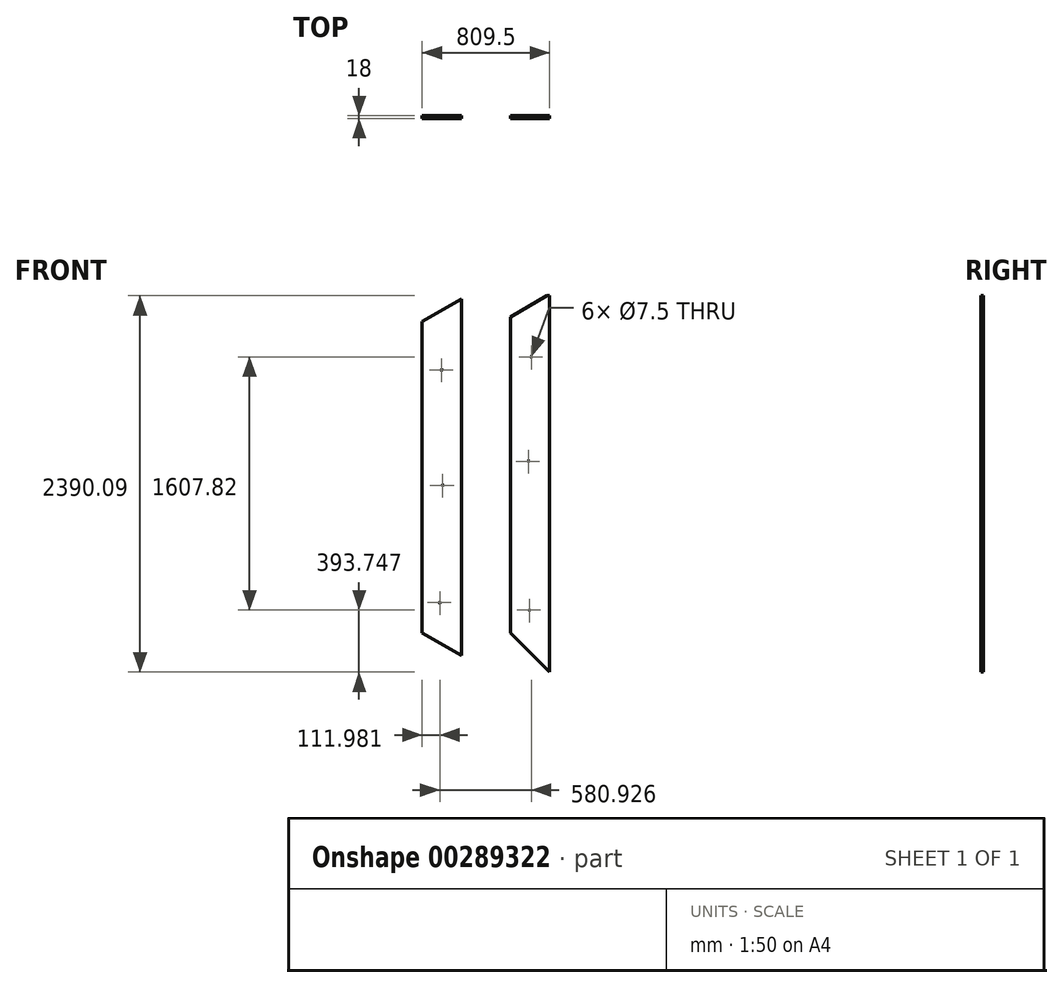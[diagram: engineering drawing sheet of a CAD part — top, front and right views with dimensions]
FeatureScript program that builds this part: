
annotation { "Feature Type Name" : "Feature", "Feature Type Description" : "" }
export const myFeature = defineFeature(function(context is Context, id is Id, definition is map)
    precondition{}
    {
        {
            var Q0;
            Q0=qCreatedBy(makeId("Front.planeOp"),FACE);
            var sketch = newSketch(context, id + "F0", { "sketchPlane" : qUnion([Q0])});
            skLineSegment(sketch, "E0", {"start": v(-600, -1204.44) * mm, "end": v(600, -1204.44) * mm});
            skLineSegment(sketch, "E1", {"start": v(600, -1204.44) * mm, "end": v(600, 1195.56) * mm});
            skLineSegment(sketch, "E2", {"start": v(600, 1195.56) * mm, "end": v(-600, 1195.56) * mm});
            skLineSegment(sketch, "E3", {"start": v(-600, 1195.56) * mm, "end": v(-600, -1204.44) * mm});
            skLineSegment(sketch, "E4", {"start": v(547.42, 1204.44) * mm, "end": v(297.92, 954.93) * mm});
            skLineSegment(sketch, "E5", {"start": v(297.92, 954.93) * mm, "end": v(297.92, -1050.48) * mm});
            skLineSegment(sketch, "E6", {"start": v(297.92, -1050.48) * mm, "end": v(547.41, -1194.53) * mm});
            skLineSegment(sketch, "E7", {"start": v(547.41, -1194.53) * mm, "end": v(547.42, 1204.44) * mm});
            skLineSegment(sketch, "E8", {"start": v(17.92, 1060.4) * mm, "end": v(17.92, -945.02) * mm});
            skLineSegment(sketch, "E9", {"start": v(17.92, -945.02) * mm, "end": v(267.42, -1194.53) * mm});
            skLineSegment(sketch, "E10", {"start": v(267.42, -1194.53) * mm, "end": v(267.41, 1204.44) * mm});
            skLineSegment(sketch, "E11", {"start": v(267.41, 1204.44) * mm, "end": v(17.92, 1060.4) * mm});
            skLineSegment(sketch, "E12", {"start": v(-262.08, -945.11) * mm, "end": v(-12.58, -1089.16) * mm});
            skLineSegment(sketch, "E13", {"start": v(-12.58, -1089.16) * mm, "end": v(-12.58, 1174.44) * mm});
            skLineSegment(sketch, "E14", {"start": v(-12.58, 1174.44) * mm, "end": v(-262.07, 1030.39) * mm});
            skLineSegment(sketch, "E15", {"start": v(-262.07, 1030.39) * mm, "end": v(-262.08, -945.11) * mm});
            skLineSegment(sketch, "E16", {"start": v(-292.58, 1174.44) * mm, "end": v(-542.07, 1030.39) * mm});
            skLineSegment(sketch, "E17", {"start": v(-542.07, 1030.39) * mm, "end": v(-542.08, -945.11) * mm});
            skLineSegment(sketch, "E18", {"start": v(-542.08, -945.11) * mm, "end": v(-292.58, -1089.16) * mm});
            skLineSegment(sketch, "E19", {"start": v(-292.58, -1089.16) * mm, "end": v(-292.58, 1174.44) * mm});
            skLineSegment(sketch, "E20", {"start": v(479.4, 17.48) * mm, "end": v(479.24, 17.93) * mm});
            skLineSegment(sketch, "E21", {"start": v(479.24, 17.93) * mm, "end": v(479.08, 18.37) * mm});
            skLineSegment(sketch, "E22", {"start": v(479.08, 18.37) * mm, "end": v(478.9, 18.8) * mm});
            skLineSegment(sketch, "E23", {"start": v(478.9, 18.8) * mm, "end": v(478.7, 19.24) * mm});
            skLineSegment(sketch, "E24", {"start": v(478.7, 19.24) * mm, "end": v(478.5, 19.66) * mm});
            skLineSegment(sketch, "E25", {"start": v(478.5, 19.66) * mm, "end": v(478.29, 20.08) * mm});
            skLineSegment(sketch, "E26", {"start": v(478.29, 20.08) * mm, "end": v(478.05, 20.49) * mm});
            skLineSegment(sketch, "E27", {"start": v(478.05, 20.49) * mm, "end": v(477.8, 20.9) * mm});
            skLineSegment(sketch, "E28", {"start": v(477.8, 20.9) * mm, "end": v(477.55, 21.28) * mm});
            skLineSegment(sketch, "E29", {"start": v(477.55, 21.28) * mm, "end": v(477.28, 21.67) * mm});
            skLineSegment(sketch, "E30", {"start": v(477.28, 21.67) * mm, "end": v(477, 22.05) * mm});
            skLineSegment(sketch, "E31", {"start": v(477, 22.05) * mm, "end": v(476.7, 22.42) * mm});
            skLineSegment(sketch, "E32", {"start": v(476.7, 22.42) * mm, "end": v(476.4, 22.78) * mm});
            skLineSegment(sketch, "E33", {"start": v(476.4, 22.78) * mm, "end": v(476.09, 23.13) * mm});
            skLineSegment(sketch, "E34", {"start": v(476.09, 23.13) * mm, "end": v(475.76, 23.47) * mm});
            skLineSegment(sketch, "E35", {"start": v(475.76, 23.47) * mm, "end": v(475.42, 23.8) * mm});
            skLineSegment(sketch, "E36", {"start": v(475.42, 23.8) * mm, "end": v(475.14, 24.06) * mm});
            skLineSegment(sketch, "E37", {"start": v(475.14, 24.06) * mm, "end": v(474.85, 24.31) * mm});
            skLineSegment(sketch, "E38", {"start": v(474.85, 24.31) * mm, "end": v(474.56, 24.56) * mm});
            skLineSegment(sketch, "E39", {"start": v(474.56, 24.56) * mm, "end": v(474.26, 24.8) * mm});
            skLineSegment(sketch, "E40", {"start": v(474.26, 24.8) * mm, "end": v(473.95, 25.03) * mm});
            skLineSegment(sketch, "E41", {"start": v(473.95, 25.03) * mm, "end": v(473.64, 25.25) * mm});
            skLineSegment(sketch, "E42", {"start": v(473.64, 25.25) * mm, "end": v(473.33, 25.47) * mm});
            skLineSegment(sketch, "E43", {"start": v(473.33, 25.47) * mm, "end": v(473, 25.67) * mm});
            skLineSegment(sketch, "E44", {"start": v(473, 25.67) * mm, "end": v(472.68, 25.87) * mm});
            skLineSegment(sketch, "E45", {"start": v(472.68, 25.87) * mm, "end": v(472.35, 26.06) * mm});
            skLineSegment(sketch, "E46", {"start": v(472.35, 26.06) * mm, "end": v(472.01, 26.24) * mm});
            skLineSegment(sketch, "E47", {"start": v(472.01, 26.24) * mm, "end": v(471.68, 26.4) * mm});
            skLineSegment(sketch, "E48", {"start": v(471.68, 26.4) * mm, "end": v(471.33, 26.57) * mm});
            skLineSegment(sketch, "E49", {"start": v(471.33, 26.57) * mm, "end": v(470.99, 26.72) * mm});
            skLineSegment(sketch, "E50", {"start": v(470.99, 26.72) * mm, "end": v(470.63, 26.87) * mm});
            skLineSegment(sketch, "E51", {"start": v(470.63, 26.87) * mm, "end": v(470.28, 27) * mm});
            skLineSegment(sketch, "E52", {"start": v(470.28, 27) * mm, "end": v(469.92, 27.13) * mm});
            skLineSegment(sketch, "E53", {"start": v(469.92, 27.13) * mm, "end": v(469.56, 27.25) * mm});
            skLineSegment(sketch, "E54", {"start": v(469.56, 27.25) * mm, "end": v(469.2, 27.36) * mm});
            skLineSegment(sketch, "E55", {"start": v(469.2, 27.36) * mm, "end": v(468.83, 27.45) * mm});
            skLineSegment(sketch, "E56", {"start": v(468.83, 27.45) * mm, "end": v(468.46, 27.54) * mm});
            skLineSegment(sketch, "E57", {"start": v(468.46, 27.54) * mm, "end": v(468.1, 27.62) * mm});
            skLineSegment(sketch, "E58", {"start": v(468.1, 27.62) * mm, "end": v(467.72, 27.7) * mm});
            skLineSegment(sketch, "E59", {"start": v(467.72, 27.7) * mm, "end": v(467.34, 27.76) * mm});
            skLineSegment(sketch, "E60", {"start": v(467.34, 27.76) * mm, "end": v(466.97, 27.8) * mm});
            skLineSegment(sketch, "E61", {"start": v(466.97, 27.8) * mm, "end": v(466.59, 27.85) * mm});
            skLineSegment(sketch, "E62", {"start": v(466.59, 27.85) * mm, "end": v(466.2, 27.88) * mm});
            skLineSegment(sketch, "E63", {"start": v(466.2, 27.88) * mm, "end": v(465.83, 27.9) * mm});
            skLineSegment(sketch, "E64", {"start": v(465.83, 27.9) * mm, "end": v(465.44, 27.92) * mm});
            skLineSegment(sketch, "E65", {"start": v(465.44, 27.92) * mm, "end": v(465.06, 27.92) * mm});
            skLineSegment(sketch, "E66", {"start": v(465.06, 27.92) * mm, "end": v(464.67, 27.92) * mm});
            skLineSegment(sketch, "E67", {"start": v(464.67, 27.92) * mm, "end": v(464.29, 27.9) * mm});
            skLineSegment(sketch, "E68", {"start": v(464.29, 27.9) * mm, "end": v(463.94, 27.9) * mm});
            skLineSegment(sketch, "E69", {"start": v(463.94, 27.9) * mm, "end": v(463.58, 27.91) * mm});
            skLineSegment(sketch, "E70", {"start": v(463.58, 27.91) * mm, "end": v(463.23, 27.9) * mm});
            skLineSegment(sketch, "E71", {"start": v(463.23, 27.9) * mm, "end": v(462.88, 27.89) * mm});
            skLineSegment(sketch, "E72", {"start": v(462.88, 27.89) * mm, "end": v(462.53, 27.86) * mm});
            skLineSegment(sketch, "E73", {"start": v(462.53, 27.86) * mm, "end": v(462.18, 27.82) * mm});
            skLineSegment(sketch, "E74", {"start": v(462.18, 27.82) * mm, "end": v(461.83, 27.78) * mm});
            skLineSegment(sketch, "E75", {"start": v(461.83, 27.78) * mm, "end": v(461.48, 27.73) * mm});
            skLineSegment(sketch, "E76", {"start": v(461.48, 27.73) * mm, "end": v(461.14, 27.67) * mm});
            skLineSegment(sketch, "E77", {"start": v(461.14, 27.67) * mm, "end": v(460.8, 27.6) * mm});
            skLineSegment(sketch, "E78", {"start": v(460.8, 27.6) * mm, "end": v(460.46, 27.52) * mm});
            skLineSegment(sketch, "E79", {"start": v(460.46, 27.52) * mm, "end": v(460.12, 27.43) * mm});
            skLineSegment(sketch, "E80", {"start": v(460.12, 27.43) * mm, "end": v(459.79, 27.33) * mm});
            skLineSegment(sketch, "E81", {"start": v(459.79, 27.33) * mm, "end": v(459.45, 27.23) * mm});
            skLineSegment(sketch, "E82", {"start": v(459.45, 27.23) * mm, "end": v(459.12, 27.12) * mm});
            skLineSegment(sketch, "E83", {"start": v(459.12, 27.12) * mm, "end": v(458.8, 27) * mm});
            skLineSegment(sketch, "E84", {"start": v(458.8, 27) * mm, "end": v(458.47, 26.86) * mm});
            skLineSegment(sketch, "E85", {"start": v(458.47, 26.86) * mm, "end": v(458.15, 26.73) * mm});
            skLineSegment(sketch, "E86", {"start": v(458.15, 26.73) * mm, "end": v(457.84, 26.58) * mm});
            skLineSegment(sketch, "E87", {"start": v(457.84, 26.58) * mm, "end": v(457.52, 26.43) * mm});
            skLineSegment(sketch, "E88", {"start": v(457.52, 26.43) * mm, "end": v(457.21, 26.26) * mm});
            skLineSegment(sketch, "E89", {"start": v(457.21, 26.26) * mm, "end": v(456.9, 26.1) * mm});
            skLineSegment(sketch, "E90", {"start": v(456.9, 26.1) * mm, "end": v(456.6, 25.92) * mm});
            skLineSegment(sketch, "E91", {"start": v(456.6, 25.92) * mm, "end": v(456.31, 25.73) * mm});
            skLineSegment(sketch, "E92", {"start": v(456.31, 25.73) * mm, "end": v(456.02, 25.54) * mm});
            skLineSegment(sketch, "E93", {"start": v(456.02, 25.54) * mm, "end": v(455.73, 25.34) * mm});
            skLineSegment(sketch, "E94", {"start": v(455.73, 25.34) * mm, "end": v(455.45, 25.13) * mm});
            skLineSegment(sketch, "E95", {"start": v(455.45, 25.13) * mm, "end": v(455.18, 24.91) * mm});
            skLineSegment(sketch, "E96", {"start": v(455.18, 24.91) * mm, "end": v(454.9, 24.69) * mm});
            skLineSegment(sketch, "E97", {"start": v(454.9, 24.69) * mm, "end": v(454.64, 24.46) * mm});
            skLineSegment(sketch, "E98", {"start": v(454.64, 24.46) * mm, "end": v(454.38, 24.22) * mm});
            skLineSegment(sketch, "E99", {"start": v(454.38, 24.22) * mm, "end": v(454.12, 23.97) * mm});
            skLineSegment(sketch, "E100", {"start": v(454.12, 23.97) * mm, "end": v(453.78, 23.63) * mm});
            skLineSegment(sketch, "E101", {"start": v(453.78, 23.63) * mm, "end": v(453.45, 23.28) * mm});
            skLineSegment(sketch, "E102", {"start": v(453.45, 23.28) * mm, "end": v(453.14, 22.9) * mm});
            skLineSegment(sketch, "E103", {"start": v(453.14, 22.9) * mm, "end": v(452.86, 22.53) * mm});
            skLineSegment(sketch, "E104", {"start": v(452.86, 22.53) * mm, "end": v(452.6, 22.14) * mm});
            skLineSegment(sketch, "E105", {"start": v(452.6, 22.14) * mm, "end": v(452.34, 21.74) * mm});
            skLineSegment(sketch, "E106", {"start": v(452.34, 21.74) * mm, "end": v(452.12, 21.34) * mm});
            skLineSegment(sketch, "E107", {"start": v(452.12, 21.34) * mm, "end": v(451.91, 20.92) * mm});
            skLineSegment(sketch, "E108", {"start": v(451.91, 20.92) * mm, "end": v(451.73, 20.5) * mm});
            skLineSegment(sketch, "E109", {"start": v(451.73, 20.5) * mm, "end": v(451.56, 20.06) * mm});
            skLineSegment(sketch, "E110", {"start": v(451.56, 20.06) * mm, "end": v(451.41, 19.63) * mm});
            skLineSegment(sketch, "E111", {"start": v(451.41, 19.63) * mm, "end": v(451.29, 19.18) * mm});
            skLineSegment(sketch, "E112", {"start": v(451.29, 19.18) * mm, "end": v(451.18, 18.74) * mm});
            skLineSegment(sketch, "E113", {"start": v(451.18, 18.74) * mm, "end": v(451.1, 18.29) * mm});
            skLineSegment(sketch, "E114", {"start": v(451.1, 18.29) * mm, "end": v(451.04, 17.83) * mm});
            skLineSegment(sketch, "E115", {"start": v(451.04, 17.83) * mm, "end": v(451, 17.38) * mm});
            skLineSegment(sketch, "E116", {"start": v(451, 17.38) * mm, "end": v(450.97, 16.92) * mm});
            skLineSegment(sketch, "E117", {"start": v(450.97, 16.92) * mm, "end": v(450.97, 16.46) * mm});
            skLineSegment(sketch, "E118", {"start": v(450.97, 16.46) * mm, "end": v(450.99, 16) * mm});
            skLineSegment(sketch, "E119", {"start": v(450.99, 16) * mm, "end": v(451.03, 15.55) * mm});
            skLineSegment(sketch, "E120", {"start": v(451.03, 15.55) * mm, "end": v(451.09, 15.1) * mm});
            skLineSegment(sketch, "E121", {"start": v(451.09, 15.1) * mm, "end": v(451.17, 14.64) * mm});
            skLineSegment(sketch, "E122", {"start": v(451.17, 14.64) * mm, "end": v(451.27, 14.19) * mm});
            skLineSegment(sketch, "E123", {"start": v(451.27, 14.19) * mm, "end": v(451.4, 13.74) * mm});
            skLineSegment(sketch, "E124", {"start": v(451.4, 13.74) * mm, "end": v(451.54, 13.3) * mm});
            skLineSegment(sketch, "E125", {"start": v(451.54, 13.3) * mm, "end": v(451.7, 12.86) * mm});
            skLineSegment(sketch, "E126", {"start": v(451.7, 12.86) * mm, "end": v(451.89, 12.43) * mm});
            skLineSegment(sketch, "E127", {"start": v(451.89, 12.43) * mm, "end": v(452.1, 12) * mm});
            skLineSegment(sketch, "E128", {"start": v(452.1, 12) * mm, "end": v(452.32, 11.6) * mm});
            skLineSegment(sketch, "E129", {"start": v(452.32, 11.6) * mm, "end": v(452.57, 11.19) * mm});
            skLineSegment(sketch, "E130", {"start": v(452.57, 11.19) * mm, "end": v(452.84, 10.79) * mm});
            skLineSegment(sketch, "E131", {"start": v(452.84, 10.79) * mm, "end": v(453.14, 10.4) * mm});
            skLineSegment(sketch, "E132", {"start": v(453.14, 10.4) * mm, "end": v(453.43, 10.1) * mm});
            skLineSegment(sketch, "E133", {"start": v(453.43, 10.1) * mm, "end": v(453.74, 9.8) * mm});
            skLineSegment(sketch, "E134", {"start": v(453.74, 9.8) * mm, "end": v(454.04, 9.53) * mm});
            skLineSegment(sketch, "E135", {"start": v(454.04, 9.53) * mm, "end": v(454.36, 9.25) * mm});
            skLineSegment(sketch, "E136", {"start": v(454.36, 9.25) * mm, "end": v(454.69, 8.99) * mm});
            skLineSegment(sketch, "E137", {"start": v(454.69, 8.99) * mm, "end": v(455.01, 8.73) * mm});
            skLineSegment(sketch, "E138", {"start": v(455.01, 8.73) * mm, "end": v(455.35, 8.49) * mm});
            skLineSegment(sketch, "E139", {"start": v(455.35, 8.49) * mm, "end": v(455.7, 8.25) * mm});
            skLineSegment(sketch, "E140", {"start": v(455.7, 8.25) * mm, "end": v(456.04, 8.03) * mm});
            skLineSegment(sketch, "E141", {"start": v(456.04, 8.03) * mm, "end": v(456.4, 7.8) * mm});
            skLineSegment(sketch, "E142", {"start": v(456.4, 7.8) * mm, "end": v(456.75, 7.6) * mm});
            skLineSegment(sketch, "E143", {"start": v(456.75, 7.6) * mm, "end": v(457.12, 7.4) * mm});
            skLineSegment(sketch, "E144", {"start": v(457.12, 7.4) * mm, "end": v(457.49, 7.22) * mm});
            skLineSegment(sketch, "E145", {"start": v(457.49, 7.22) * mm, "end": v(457.86, 7.04) * mm});
            skLineSegment(sketch, "E146", {"start": v(457.86, 7.04) * mm, "end": v(458.24, 6.87) * mm});
            skLineSegment(sketch, "E147", {"start": v(458.24, 6.87) * mm, "end": v(458.62, 6.72) * mm});
            skLineSegment(sketch, "E148", {"start": v(458.62, 6.72) * mm, "end": v(459, 6.57) * mm});
            skLineSegment(sketch, "E149", {"start": v(459, 6.57) * mm, "end": v(459.4, 6.43) * mm});
            skLineSegment(sketch, "E150", {"start": v(459.4, 6.43) * mm, "end": v(459.8, 6.3) * mm});
            skLineSegment(sketch, "E151", {"start": v(459.8, 6.3) * mm, "end": v(460.19, 6.19) * mm});
            skLineSegment(sketch, "E152", {"start": v(460.19, 6.19) * mm, "end": v(460.59, 6.08) * mm});
            skLineSegment(sketch, "E153", {"start": v(460.59, 6.08) * mm, "end": v(461, 5.99) * mm});
            skLineSegment(sketch, "E154", {"start": v(461, 5.99) * mm, "end": v(461.4, 5.9) * mm});
            skLineSegment(sketch, "E155", {"start": v(461.4, 5.9) * mm, "end": v(461.8, 5.83) * mm});
            skLineSegment(sketch, "E156", {"start": v(461.8, 5.83) * mm, "end": v(462.22, 5.77) * mm});
            skLineSegment(sketch, "E157", {"start": v(462.22, 5.77) * mm, "end": v(462.63, 5.72) * mm});
            skLineSegment(sketch, "E158", {"start": v(462.63, 5.72) * mm, "end": v(463.05, 5.68) * mm});
            skLineSegment(sketch, "E159", {"start": v(463.05, 5.68) * mm, "end": v(463.46, 5.65) * mm});
            skLineSegment(sketch, "E160", {"start": v(463.46, 5.65) * mm, "end": v(463.88, 5.63) * mm});
            skLineSegment(sketch, "E161", {"start": v(463.88, 5.63) * mm, "end": v(464.3, 5.63) * mm});
            skLineSegment(sketch, "E162", {"start": v(464.3, 5.63) * mm, "end": v(464.72, 5.63) * mm});
            skLineSegment(sketch, "E163", {"start": v(464.72, 5.63) * mm, "end": v(465.14, 5.65) * mm});
            skLineSegment(sketch, "E164", {"start": v(465.14, 5.65) * mm, "end": v(465.7, 5.71) * mm});
            skLineSegment(sketch, "E165", {"start": v(465.7, 5.71) * mm, "end": v(466.26, 5.75) * mm});
            skLineSegment(sketch, "E166", {"start": v(466.26, 5.75) * mm, "end": v(466.81, 5.76) * mm});
            skLineSegment(sketch, "E167", {"start": v(466.81, 5.76) * mm, "end": v(467.36, 5.74) * mm});
            skLineSegment(sketch, "E168", {"start": v(467.36, 5.74) * mm, "end": v(467.9, 5.7) * mm});
            skLineSegment(sketch, "E169", {"start": v(467.9, 5.7) * mm, "end": v(468.45, 5.62) * mm});
            skLineSegment(sketch, "E170", {"start": v(468.45, 5.62) * mm, "end": v(468.98, 5.53) * mm});
            skLineSegment(sketch, "E171", {"start": v(468.98, 5.53) * mm, "end": v(469.5, 5.4) * mm});
            skLineSegment(sketch, "E172", {"start": v(469.5, 5.4) * mm, "end": v(470.02, 5.26) * mm});
            skLineSegment(sketch, "E173", {"start": v(470.02, 5.26) * mm, "end": v(470.53, 5.1) * mm});
            skLineSegment(sketch, "E174", {"start": v(470.53, 5.1) * mm, "end": v(471.03, 4.9) * mm});
            skLineSegment(sketch, "E175", {"start": v(471.03, 4.9) * mm, "end": v(471.52, 4.69) * mm});
            skLineSegment(sketch, "E176", {"start": v(471.52, 4.69) * mm, "end": v(472, 4.45) * mm});
            skLineSegment(sketch, "E177", {"start": v(472, 4.45) * mm, "end": v(472.46, 4.2) * mm});
            skLineSegment(sketch, "E178", {"start": v(472.46, 4.2) * mm, "end": v(472.91, 3.91) * mm});
            skLineSegment(sketch, "E179", {"start": v(472.91, 3.91) * mm, "end": v(473.35, 3.61) * mm});
            skLineSegment(sketch, "E180", {"start": v(473.35, 3.61) * mm, "end": v(473.77, 3.3) * mm});
            skLineSegment(sketch, "E181", {"start": v(473.77, 3.3) * mm, "end": v(474.18, 2.96) * mm});
            skLineSegment(sketch, "E182", {"start": v(474.18, 2.96) * mm, "end": v(474.58, 2.6) * mm});
            skLineSegment(sketch, "E183", {"start": v(474.58, 2.6) * mm, "end": v(474.95, 2.22) * mm});
            skLineSegment(sketch, "E184", {"start": v(474.95, 2.22) * mm, "end": v(475.31, 1.83) * mm});
            skLineSegment(sketch, "E185", {"start": v(475.31, 1.83) * mm, "end": v(475.66, 1.42) * mm});
            skLineSegment(sketch, "E186", {"start": v(475.66, 1.42) * mm, "end": v(475.98, 1) * mm});
            skLineSegment(sketch, "E187", {"start": v(475.98, 1) * mm, "end": v(476.28, 0.55) * mm});
            skLineSegment(sketch, "E188", {"start": v(476.28, 0.55) * mm, "end": v(476.57, 0.1) * mm});
            skLineSegment(sketch, "E189", {"start": v(476.57, 0.1) * mm, "end": v(476.83, -0.38) * mm});
            skLineSegment(sketch, "E190", {"start": v(476.83, -0.38) * mm, "end": v(477.07, -0.87) * mm});
            skLineSegment(sketch, "E191", {"start": v(477.07, -0.87) * mm, "end": v(477.29, -1.37) * mm});
            skLineSegment(sketch, "E192", {"start": v(477.29, -1.37) * mm, "end": v(477.48, -1.88) * mm});
            skLineSegment(sketch, "E193", {"start": v(477.48, -1.88) * mm, "end": v(477.65, -2.41) * mm});
            skLineSegment(sketch, "E194", {"start": v(477.65, -2.41) * mm, "end": v(477.8, -2.95) * mm});
            skLineSegment(sketch, "E195", {"start": v(477.8, -2.95) * mm, "end": v(477.92, -3.5) * mm});
            skLineSegment(sketch, "E196", {"start": v(477.92, -3.5) * mm, "end": v(477.92, -3.96) * mm});
            skLineSegment(sketch, "E197", {"start": v(477.92, -3.96) * mm, "end": v(477.9, -4.41) * mm});
            skLineSegment(sketch, "E198", {"start": v(477.9, -4.41) * mm, "end": v(477.84, -4.86) * mm});
            skLineSegment(sketch, "E199", {"start": v(477.84, -4.86) * mm, "end": v(477.76, -5.3) * mm});
            skLineSegment(sketch, "E200", {"start": v(477.76, -5.3) * mm, "end": v(477.66, -5.75) * mm});
            skLineSegment(sketch, "E201", {"start": v(477.66, -5.75) * mm, "end": v(477.54, -6.18) * mm});
            skLineSegment(sketch, "E202", {"start": v(477.54, -6.18) * mm, "end": v(477.39, -6.6) * mm});
            skLineSegment(sketch, "E203", {"start": v(477.39, -6.6) * mm, "end": v(477.22, -7.02) * mm});
            skLineSegment(sketch, "E204", {"start": v(477.22, -7.02) * mm, "end": v(477.02, -7.42) * mm});
            skLineSegment(sketch, "E205", {"start": v(477.02, -7.42) * mm, "end": v(476.8, -7.81) * mm});
            skLineSegment(sketch, "E206", {"start": v(476.8, -7.81) * mm, "end": v(476.57, -8.2) * mm});
            skLineSegment(sketch, "E207", {"start": v(476.57, -8.2) * mm, "end": v(476.3, -8.56) * mm});
            skLineSegment(sketch, "E208", {"start": v(476.3, -8.56) * mm, "end": v(476.03, -8.91) * mm});
            skLineSegment(sketch, "E209", {"start": v(476.03, -8.91) * mm, "end": v(475.72, -9.25) * mm});
            skLineSegment(sketch, "E210", {"start": v(475.72, -9.25) * mm, "end": v(475.4, -9.57) * mm});
            skLineSegment(sketch, "E211", {"start": v(475.4, -9.57) * mm, "end": v(475.06, -9.88) * mm});
            skLineSegment(sketch, "E212", {"start": v(475.06, -9.88) * mm, "end": v(474.78, -10.13) * mm});
            skLineSegment(sketch, "E213", {"start": v(474.78, -10.13) * mm, "end": v(474.5, -10.37) * mm});
            skLineSegment(sketch, "E214", {"start": v(474.5, -10.37) * mm, "end": v(474.2, -10.6) * mm});
            skLineSegment(sketch, "E215", {"start": v(474.2, -10.6) * mm, "end": v(473.91, -10.82) * mm});
            skLineSegment(sketch, "E216", {"start": v(473.91, -10.82) * mm, "end": v(473.61, -11.04) * mm});
            skLineSegment(sketch, "E217", {"start": v(473.61, -11.04) * mm, "end": v(473.3, -11.25) * mm});
            skLineSegment(sketch, "E218", {"start": v(473.3, -11.25) * mm, "end": v(473, -11.45) * mm});
            skLineSegment(sketch, "E219", {"start": v(473, -11.45) * mm, "end": v(472.68, -11.65) * mm});
            skLineSegment(sketch, "E220", {"start": v(472.68, -11.65) * mm, "end": v(472.36, -11.83) * mm});
            skLineSegment(sketch, "E221", {"start": v(472.36, -11.83) * mm, "end": v(472.04, -12) * mm});
            skLineSegment(sketch, "E222", {"start": v(472.04, -12) * mm, "end": v(471.7, -12.18) * mm});
            skLineSegment(sketch, "E223", {"start": v(471.7, -12.18) * mm, "end": v(471.38, -12.34) * mm});
            skLineSegment(sketch, "E224", {"start": v(471.38, -12.34) * mm, "end": v(471.04, -12.49) * mm});
            skLineSegment(sketch, "E225", {"start": v(471.04, -12.49) * mm, "end": v(470.7, -12.63) * mm});
            skLineSegment(sketch, "E226", {"start": v(470.7, -12.63) * mm, "end": v(470.36, -12.77) * mm});
            skLineSegment(sketch, "E227", {"start": v(470.36, -12.77) * mm, "end": v(470.01, -12.9) * mm});
            skLineSegment(sketch, "E228", {"start": v(470.01, -12.9) * mm, "end": v(469.67, -13) * mm});
            skLineSegment(sketch, "E229", {"start": v(469.67, -13) * mm, "end": v(469.31, -13.12) * mm});
            skLineSegment(sketch, "E230", {"start": v(469.31, -13.12) * mm, "end": v(468.96, -13.22) * mm});
            skLineSegment(sketch, "E231", {"start": v(468.96, -13.22) * mm, "end": v(468.6, -13.3) * mm});
            skLineSegment(sketch, "E232", {"start": v(468.6, -13.3) * mm, "end": v(468.24, -13.4) * mm});
            skLineSegment(sketch, "E233", {"start": v(468.24, -13.4) * mm, "end": v(467.88, -13.46) * mm});
            skLineSegment(sketch, "E234", {"start": v(467.88, -13.46) * mm, "end": v(467.52, -13.53) * mm});
            skLineSegment(sketch, "E235", {"start": v(467.52, -13.53) * mm, "end": v(467.15, -13.58) * mm});
            skLineSegment(sketch, "E236", {"start": v(467.15, -13.58) * mm, "end": v(466.79, -13.63) * mm});
            skLineSegment(sketch, "E237", {"start": v(466.79, -13.63) * mm, "end": v(466.42, -13.67) * mm});
            skLineSegment(sketch, "E238", {"start": v(466.42, -13.67) * mm, "end": v(466.05, -13.7) * mm});
            skLineSegment(sketch, "E239", {"start": v(466.05, -13.7) * mm, "end": v(465.68, -13.71) * mm});
            skLineSegment(sketch, "E240", {"start": v(465.68, -13.71) * mm, "end": v(465.3, -13.72) * mm});
            skLineSegment(sketch, "E241", {"start": v(465.3, -13.72) * mm, "end": v(464.94, -13.72) * mm});
            skLineSegment(sketch, "E242", {"start": v(464.94, -13.72) * mm, "end": v(464.56, -13.71) * mm});
            skLineSegment(sketch, "E243", {"start": v(464.56, -13.71) * mm, "end": v(464.2, -13.7) * mm});
            skLineSegment(sketch, "E244", {"start": v(464.2, -13.7) * mm, "end": v(463.86, -13.7) * mm});
            skLineSegment(sketch, "E245", {"start": v(463.86, -13.7) * mm, "end": v(463.53, -13.7) * mm});
            skLineSegment(sketch, "E246", {"start": v(463.53, -13.7) * mm, "end": v(463.2, -13.68) * mm});
            skLineSegment(sketch, "E247", {"start": v(463.2, -13.68) * mm, "end": v(462.88, -13.66) * mm});
            skLineSegment(sketch, "E248", {"start": v(462.88, -13.66) * mm, "end": v(462.56, -13.63) * mm});
            skLineSegment(sketch, "E249", {"start": v(462.56, -13.63) * mm, "end": v(462.23, -13.6) * mm});
            skLineSegment(sketch, "E250", {"start": v(462.23, -13.6) * mm, "end": v(461.9, -13.56) * mm});
            skLineSegment(sketch, "E251", {"start": v(461.9, -13.56) * mm, "end": v(461.59, -13.5) * mm});
            skLineSegment(sketch, "E252", {"start": v(461.59, -13.5) * mm, "end": v(461.27, -13.45) * mm});
            skLineSegment(sketch, "E253", {"start": v(461.27, -13.45) * mm, "end": v(460.95, -13.38) * mm});
            skLineSegment(sketch, "E254", {"start": v(460.95, -13.38) * mm, "end": v(460.63, -13.3) * mm});
            skLineSegment(sketch, "E255", {"start": v(460.63, -13.3) * mm, "end": v(460.32, -13.22) * mm});
            skLineSegment(sketch, "E256", {"start": v(460.32, -13.22) * mm, "end": v(460, -13.14) * mm});
            skLineSegment(sketch, "E257", {"start": v(460, -13.14) * mm, "end": v(459.7, -13.04) * mm});
            skLineSegment(sketch, "E258", {"start": v(459.7, -13.04) * mm, "end": v(459.4, -12.94) * mm});
            skLineSegment(sketch, "E259", {"start": v(459.4, -12.94) * mm, "end": v(459.09, -12.82) * mm});
            skLineSegment(sketch, "E260", {"start": v(459.09, -12.82) * mm, "end": v(458.78, -12.7) * mm});
            skLineSegment(sketch, "E261", {"start": v(458.78, -12.7) * mm, "end": v(458.49, -12.58) * mm});
            skLineSegment(sketch, "E262", {"start": v(458.49, -12.58) * mm, "end": v(458.19, -12.45) * mm});
            skLineSegment(sketch, "E263", {"start": v(458.19, -12.45) * mm, "end": v(457.9, -12.3) * mm});
            skLineSegment(sketch, "E264", {"start": v(457.9, -12.3) * mm, "end": v(457.6, -12.16) * mm});
            skLineSegment(sketch, "E265", {"start": v(457.6, -12.16) * mm, "end": v(457.32, -12) * mm});
            skLineSegment(sketch, "E266", {"start": v(457.32, -12) * mm, "end": v(457.04, -11.85) * mm});
            skLineSegment(sketch, "E267", {"start": v(457.04, -11.85) * mm, "end": v(456.76, -11.68) * mm});
            skLineSegment(sketch, "E268", {"start": v(456.76, -11.68) * mm, "end": v(456.48, -11.5) * mm});
            skLineSegment(sketch, "E269", {"start": v(456.48, -11.5) * mm, "end": v(456.21, -11.33) * mm});
            skLineSegment(sketch, "E270", {"start": v(456.21, -11.33) * mm, "end": v(455.95, -11.14) * mm});
            skLineSegment(sketch, "E271", {"start": v(455.95, -11.14) * mm, "end": v(455.68, -10.94) * mm});
            skLineSegment(sketch, "E272", {"start": v(455.68, -10.94) * mm, "end": v(455.43, -10.74) * mm});
            skLineSegment(sketch, "E273", {"start": v(455.43, -10.74) * mm, "end": v(455.17, -10.54) * mm});
            skLineSegment(sketch, "E274", {"start": v(455.17, -10.54) * mm, "end": v(454.93, -10.32) * mm});
            skLineSegment(sketch, "E275", {"start": v(454.93, -10.32) * mm, "end": v(454.68, -10.1) * mm});
            skLineSegment(sketch, "E276", {"start": v(454.68, -10.1) * mm, "end": v(454.38, -9.77) * mm});
            skLineSegment(sketch, "E277", {"start": v(454.38, -9.77) * mm, "end": v(454.1, -9.44) * mm});
            skLineSegment(sketch, "E278", {"start": v(454.1, -9.44) * mm, "end": v(453.82, -9.1) * mm});
            skLineSegment(sketch, "E279", {"start": v(453.82, -9.1) * mm, "end": v(453.56, -8.74) * mm});
            skLineSegment(sketch, "E280", {"start": v(453.56, -8.74) * mm, "end": v(453.31, -8.37) * mm});
            skLineSegment(sketch, "E281", {"start": v(453.31, -8.37) * mm, "end": v(453.08, -8) * mm});
            skLineSegment(sketch, "E282", {"start": v(453.08, -8) * mm, "end": v(452.85, -7.62) * mm});
            skLineSegment(sketch, "E283", {"start": v(452.85, -7.62) * mm, "end": v(452.64, -7.23) * mm});
            skLineSegment(sketch, "E284", {"start": v(452.64, -7.23) * mm, "end": v(452.45, -6.84) * mm});
            skLineSegment(sketch, "E285", {"start": v(452.45, -6.84) * mm, "end": v(452.26, -6.44) * mm});
            skLineSegment(sketch, "E286", {"start": v(452.26, -6.44) * mm, "end": v(452.1, -6.03) * mm});
            skLineSegment(sketch, "E287", {"start": v(452.1, -6.03) * mm, "end": v(451.94, -5.62) * mm});
            skLineSegment(sketch, "E288", {"start": v(451.94, -5.62) * mm, "end": v(451.8, -5.2) * mm});
            skLineSegment(sketch, "E289", {"start": v(451.8, -5.2) * mm, "end": v(451.68, -4.78) * mm});
            skLineSegment(sketch, "E290", {"start": v(451.68, -4.78) * mm, "end": v(451.56, -4.35) * mm});
            skLineSegment(sketch, "E291", {"start": v(451.56, -4.35) * mm, "end": v(451.47, -3.92) * mm});
            skLineSegment(sketch, "E292", {"start": v(442, 27.07) * mm, "end": v(442, -12.88) * mm});
            skLineSegment(sketch, "E293", {"start": v(433.2, 27.07) * mm, "end": v(433.2, -12.9) * mm});
            skLineSegment(sketch, "E294", {"start": v(433.2, -12.9) * mm, "end": v(418.54, -12.9) * mm});
            skLineSegment(sketch, "E295", {"start": v(418.54, -12.9) * mm, "end": v(418.2, -12.88) * mm});
            skLineSegment(sketch, "E296", {"start": v(418.2, -12.88) * mm, "end": v(417.85, -12.86) * mm});
            skLineSegment(sketch, "E297", {"start": v(417.85, -12.86) * mm, "end": v(417.5, -12.83) * mm});
            skLineSegment(sketch, "E298", {"start": v(417.5, -12.83) * mm, "end": v(417.16, -12.78) * mm});
            skLineSegment(sketch, "E299", {"start": v(417.16, -12.78) * mm, "end": v(416.82, -12.73) * mm});
            skLineSegment(sketch, "E300", {"start": v(416.82, -12.73) * mm, "end": v(416.48, -12.67) * mm});
            skLineSegment(sketch, "E301", {"start": v(416.48, -12.67) * mm, "end": v(416.14, -12.6) * mm});
            skLineSegment(sketch, "E302", {"start": v(416.14, -12.6) * mm, "end": v(415.8, -12.53) * mm});
            skLineSegment(sketch, "E303", {"start": v(415.8, -12.53) * mm, "end": v(415.47, -12.44) * mm});
            skLineSegment(sketch, "E304", {"start": v(415.47, -12.44) * mm, "end": v(415.14, -12.35) * mm});
            skLineSegment(sketch, "E305", {"start": v(415.14, -12.35) * mm, "end": v(414.82, -12.25) * mm});
            skLineSegment(sketch, "E306", {"start": v(414.82, -12.25) * mm, "end": v(414.5, -12.14) * mm});
            skLineSegment(sketch, "E307", {"start": v(414.5, -12.14) * mm, "end": v(414.17, -12.02) * mm});
            skLineSegment(sketch, "E308", {"start": v(414.17, -12.02) * mm, "end": v(413.85, -11.9) * mm});
            skLineSegment(sketch, "E309", {"start": v(413.85, -11.9) * mm, "end": v(413.54, -11.76) * mm});
            skLineSegment(sketch, "E310", {"start": v(413.54, -11.76) * mm, "end": v(413.22, -11.62) * mm});
            skLineSegment(sketch, "E311", {"start": v(413.22, -11.62) * mm, "end": v(412.92, -11.47) * mm});
            skLineSegment(sketch, "E312", {"start": v(412.92, -11.47) * mm, "end": v(412.61, -11.31) * mm});
            skLineSegment(sketch, "E313", {"start": v(412.61, -11.31) * mm, "end": v(412.31, -11.15) * mm});
            skLineSegment(sketch, "E314", {"start": v(412.31, -11.15) * mm, "end": v(412.01, -10.98) * mm});
            skLineSegment(sketch, "E315", {"start": v(412.01, -10.98) * mm, "end": v(411.72, -10.8) * mm});
            skLineSegment(sketch, "E316", {"start": v(411.72, -10.8) * mm, "end": v(411.43, -10.61) * mm});
            skLineSegment(sketch, "E317", {"start": v(411.43, -10.61) * mm, "end": v(411.15, -10.42) * mm});
            skLineSegment(sketch, "E318", {"start": v(411.15, -10.42) * mm, "end": v(410.87, -10.21) * mm});
            skLineSegment(sketch, "E319", {"start": v(410.87, -10.21) * mm, "end": v(410.6, -10) * mm});
            skLineSegment(sketch, "E320", {"start": v(410.6, -10) * mm, "end": v(410.33, -9.8) * mm});
            skLineSegment(sketch, "E321", {"start": v(410.33, -9.8) * mm, "end": v(410.07, -9.57) * mm});
            skLineSegment(sketch, "E322", {"start": v(410.07, -9.57) * mm, "end": v(409.8, -9.34) * mm});
            skLineSegment(sketch, "E323", {"start": v(409.8, -9.34) * mm, "end": v(409.56, -9.1) * mm});
            skLineSegment(sketch, "E324", {"start": v(409.56, -9.1) * mm, "end": v(409.3, -8.86) * mm});
            skLineSegment(sketch, "E325", {"start": v(409.3, -8.86) * mm, "end": v(409.07, -8.61) * mm});
            skLineSegment(sketch, "E326", {"start": v(409.07, -8.61) * mm, "end": v(408.83, -8.35) * mm});
            skLineSegment(sketch, "E327", {"start": v(408.83, -8.35) * mm, "end": v(408.43, -7.94) * mm});
            skLineSegment(sketch, "E328", {"start": v(408.43, -7.94) * mm, "end": v(408.04, -7.52) * mm});
            skLineSegment(sketch, "E329", {"start": v(408.04, -7.52) * mm, "end": v(407.67, -7.1) * mm});
            skLineSegment(sketch, "E330", {"start": v(407.67, -7.1) * mm, "end": v(407.3, -6.65) * mm});
            skLineSegment(sketch, "E331", {"start": v(407.3, -6.65) * mm, "end": v(406.94, -6.2) * mm});
            skLineSegment(sketch, "E332", {"start": v(406.94, -6.2) * mm, "end": v(406.6, -5.75) * mm});
            skLineSegment(sketch, "E333", {"start": v(406.6, -5.75) * mm, "end": v(406.27, -5.28) * mm});
            skLineSegment(sketch, "E334", {"start": v(406.27, -5.28) * mm, "end": v(405.95, -4.81) * mm});
            skLineSegment(sketch, "E335", {"start": v(405.95, -4.81) * mm, "end": v(405.65, -4.33) * mm});
            skLineSegment(sketch, "E336", {"start": v(405.65, -4.33) * mm, "end": v(405.35, -3.85) * mm});
            skLineSegment(sketch, "E337", {"start": v(405.35, -3.85) * mm, "end": v(405.07, -3.36) * mm});
            skLineSegment(sketch, "E338", {"start": v(405.07, -3.36) * mm, "end": v(404.8, -2.86) * mm});
            skLineSegment(sketch, "E339", {"start": v(404.8, -2.86) * mm, "end": v(404.55, -2.35) * mm});
            skLineSegment(sketch, "E340", {"start": v(404.55, -2.35) * mm, "end": v(404.3, -1.84) * mm});
            skLineSegment(sketch, "E341", {"start": v(404.3, -1.84) * mm, "end": v(404.07, -1.32) * mm});
            skLineSegment(sketch, "E342", {"start": v(404.07, -1.32) * mm, "end": v(403.85, -0.8) * mm});
            skLineSegment(sketch, "E343", {"start": v(403.85, -0.8) * mm, "end": v(403.65, -0.27) * mm});
            skLineSegment(sketch, "E344", {"start": v(403.65, -0.27) * mm, "end": v(403.46, 0.26) * mm});
            skLineSegment(sketch, "E345", {"start": v(403.46, 0.26) * mm, "end": v(403.28, 0.8) * mm});
            skLineSegment(sketch, "E346", {"start": v(403.28, 0.8) * mm, "end": v(403.11, 1.34) * mm});
            skLineSegment(sketch, "E347", {"start": v(403.11, 1.34) * mm, "end": v(402.96, 1.89) * mm});
            skLineSegment(sketch, "E348", {"start": v(402.96, 1.89) * mm, "end": v(402.83, 2.44) * mm});
            skLineSegment(sketch, "E349", {"start": v(402.83, 2.44) * mm, "end": v(402.7, 3) * mm});
            skLineSegment(sketch, "E350", {"start": v(402.7, 3) * mm, "end": v(402.6, 3.55) * mm});
            skLineSegment(sketch, "E351", {"start": v(402.6, 3.55) * mm, "end": v(402.5, 4.11) * mm});
            skLineSegment(sketch, "E352", {"start": v(402.5, 4.11) * mm, "end": v(402.41, 4.67) * mm});
            skLineSegment(sketch, "E353", {"start": v(402.41, 4.67) * mm, "end": v(402.34, 5.24) * mm});
            skLineSegment(sketch, "E354", {"start": v(402.34, 5.24) * mm, "end": v(402.29, 5.8) * mm});
            skLineSegment(sketch, "E355", {"start": v(402.29, 5.8) * mm, "end": v(402.25, 6.38) * mm});
            skLineSegment(sketch, "E356", {"start": v(402.25, 6.38) * mm, "end": v(402.22, 6.95) * mm});
            skLineSegment(sketch, "E357", {"start": v(402.22, 6.95) * mm, "end": v(402.21, 7.53) * mm});
            skLineSegment(sketch, "E358", {"start": v(402.21, 7.53) * mm, "end": v(402.22, 8.1) * mm});
            skLineSegment(sketch, "E359", {"start": v(402.22, 8.1) * mm, "end": v(402.2, 8.58) * mm});
            skLineSegment(sketch, "E360", {"start": v(402.2, 8.58) * mm, "end": v(402.2, 9.06) * mm});
            skLineSegment(sketch, "E361", {"start": v(402.2, 9.06) * mm, "end": v(402.22, 9.54) * mm});
            skLineSegment(sketch, "E362", {"start": v(402.22, 9.54) * mm, "end": v(402.24, 10.02) * mm});
            skLineSegment(sketch, "E363", {"start": v(402.24, 10.02) * mm, "end": v(402.28, 10.5) * mm});
            skLineSegment(sketch, "E364", {"start": v(402.28, 10.5) * mm, "end": v(402.33, 10.98) * mm});
            skLineSegment(sketch, "E365", {"start": v(402.33, 10.98) * mm, "end": v(402.39, 11.45) * mm});
            skLineSegment(sketch, "E366", {"start": v(402.39, 11.45) * mm, "end": v(402.46, 11.92) * mm});
            skLineSegment(sketch, "E367", {"start": v(402.46, 11.92) * mm, "end": v(402.54, 12.4) * mm});
            skLineSegment(sketch, "E368", {"start": v(402.54, 12.4) * mm, "end": v(402.63, 12.86) * mm});
            skLineSegment(sketch, "E369", {"start": v(402.63, 12.86) * mm, "end": v(402.74, 13.32) * mm});
            skLineSegment(sketch, "E370", {"start": v(402.74, 13.32) * mm, "end": v(402.86, 13.78) * mm});
            skLineSegment(sketch, "E371", {"start": v(402.86, 13.78) * mm, "end": v(402.98, 14.24) * mm});
            skLineSegment(sketch, "E372", {"start": v(402.98, 14.24) * mm, "end": v(403.12, 14.7) * mm});
            skLineSegment(sketch, "E373", {"start": v(403.12, 14.7) * mm, "end": v(403.27, 15.15) * mm});
            skLineSegment(sketch, "E374", {"start": v(403.27, 15.15) * mm, "end": v(403.43, 15.6) * mm});
            skLineSegment(sketch, "E375", {"start": v(403.43, 15.6) * mm, "end": v(403.6, 16.04) * mm});
            skLineSegment(sketch, "E376", {"start": v(403.6, 16.04) * mm, "end": v(403.79, 16.48) * mm});
            skLineSegment(sketch, "E377", {"start": v(403.79, 16.48) * mm, "end": v(403.98, 16.9) * mm});
            skLineSegment(sketch, "E378", {"start": v(403.98, 16.9) * mm, "end": v(404.18, 17.34) * mm});
            skLineSegment(sketch, "E379", {"start": v(404.18, 17.34) * mm, "end": v(404.4, 17.76) * mm});
            skLineSegment(sketch, "E380", {"start": v(404.4, 17.76) * mm, "end": v(404.62, 18.18) * mm});
            skLineSegment(sketch, "E381", {"start": v(404.62, 18.18) * mm, "end": v(404.86, 18.6) * mm});
            skLineSegment(sketch, "E382", {"start": v(404.86, 18.6) * mm, "end": v(405.1, 19) * mm});
            skLineSegment(sketch, "E383", {"start": v(405.1, 19) * mm, "end": v(405.36, 19.4) * mm});
            skLineSegment(sketch, "E384", {"start": v(405.36, 19.4) * mm, "end": v(405.62, 19.8) * mm});
            skLineSegment(sketch, "E385", {"start": v(405.62, 19.8) * mm, "end": v(405.9, 20.2) * mm});
            skLineSegment(sketch, "E386", {"start": v(405.9, 20.2) * mm, "end": v(406.19, 20.58) * mm});
            skLineSegment(sketch, "E387", {"start": v(406.19, 20.58) * mm, "end": v(406.48, 20.96) * mm});
            skLineSegment(sketch, "E388", {"start": v(406.48, 20.96) * mm, "end": v(406.79, 21.33) * mm});
            skLineSegment(sketch, "E389", {"start": v(406.79, 21.33) * mm, "end": v(407.1, 21.7) * mm});
            skLineSegment(sketch, "E390", {"start": v(407.1, 21.7) * mm, "end": v(407.43, 22.05) * mm});
            skLineSegment(sketch, "E391", {"start": v(407.43, 22.05) * mm, "end": v(407.7, 22.33) * mm});
            skLineSegment(sketch, "E392", {"start": v(407.7, 22.33) * mm, "end": v(407.98, 22.6) * mm});
            skLineSegment(sketch, "E393", {"start": v(407.98, 22.6) * mm, "end": v(408.27, 22.88) * mm});
            skLineSegment(sketch, "E394", {"start": v(408.27, 22.88) * mm, "end": v(408.56, 23.14) * mm});
            skLineSegment(sketch, "E395", {"start": v(408.56, 23.14) * mm, "end": v(408.86, 23.4) * mm});
            skLineSegment(sketch, "E396", {"start": v(408.86, 23.4) * mm, "end": v(409.16, 23.64) * mm});
            skLineSegment(sketch, "E397", {"start": v(409.16, 23.64) * mm, "end": v(409.47, 23.88) * mm});
            skLineSegment(sketch, "E398", {"start": v(409.47, 23.88) * mm, "end": v(409.79, 24.1) * mm});
            skLineSegment(sketch, "E399", {"start": v(409.79, 24.1) * mm, "end": v(410.11, 24.33) * mm});
            skLineSegment(sketch, "E400", {"start": v(410.11, 24.33) * mm, "end": v(410.44, 24.55) * mm});
            skLineSegment(sketch, "E401", {"start": v(410.44, 24.55) * mm, "end": v(410.77, 24.75) * mm});
            skLineSegment(sketch, "E402", {"start": v(410.77, 24.75) * mm, "end": v(411.1, 24.95) * mm});
            skLineSegment(sketch, "E403", {"start": v(411.1, 24.95) * mm, "end": v(411.44, 25.14) * mm});
            skLineSegment(sketch, "E404", {"start": v(411.44, 25.14) * mm, "end": v(411.79, 25.32) * mm});
            skLineSegment(sketch, "E405", {"start": v(411.79, 25.32) * mm, "end": v(412.13, 25.5) * mm});
            skLineSegment(sketch, "E406", {"start": v(412.13, 25.5) * mm, "end": v(412.49, 25.66) * mm});
            skLineSegment(sketch, "E407", {"start": v(412.49, 25.66) * mm, "end": v(412.84, 25.82) * mm});
            skLineSegment(sketch, "E408", {"start": v(412.84, 25.82) * mm, "end": v(413.2, 25.96) * mm});
            skLineSegment(sketch, "E409", {"start": v(413.2, 25.96) * mm, "end": v(413.57, 26.1) * mm});
            skLineSegment(sketch, "E410", {"start": v(413.57, 26.1) * mm, "end": v(413.94, 26.23) * mm});
            skLineSegment(sketch, "E411", {"start": v(413.94, 26.23) * mm, "end": v(414.3, 26.35) * mm});
            skLineSegment(sketch, "E412", {"start": v(414.3, 26.35) * mm, "end": v(414.68, 26.47) * mm});
            skLineSegment(sketch, "E413", {"start": v(414.68, 26.47) * mm, "end": v(415.06, 26.57) * mm});
            skLineSegment(sketch, "E414", {"start": v(415.06, 26.57) * mm, "end": v(415.43, 26.66) * mm});
            skLineSegment(sketch, "E415", {"start": v(415.43, 26.66) * mm, "end": v(415.82, 26.75) * mm});
            skLineSegment(sketch, "E416", {"start": v(415.82, 26.75) * mm, "end": v(416.2, 26.82) * mm});
            skLineSegment(sketch, "E417", {"start": v(416.2, 26.82) * mm, "end": v(416.59, 26.89) * mm});
            skLineSegment(sketch, "E418", {"start": v(416.59, 26.89) * mm, "end": v(416.97, 26.94) * mm});
            skLineSegment(sketch, "E419", {"start": v(416.97, 26.94) * mm, "end": v(417.36, 27) * mm});
            skLineSegment(sketch, "E420", {"start": v(417.36, 27) * mm, "end": v(417.76, 27.03) * mm});
            skLineSegment(sketch, "E421", {"start": v(417.76, 27.03) * mm, "end": v(418.15, 27.06) * mm});
            skLineSegment(sketch, "E422", {"start": v(418.15, 27.06) * mm, "end": v(418.54, 27.07) * mm});
            skLineSegment(sketch, "E423", {"start": v(418.54, 27.07) * mm, "end": v(433.2, 27.07) * mm});
            skLineSegment(sketch, "E424", {"start": v(366.88, 27.07) * mm, "end": v(393.2, 27.07) * mm});
            skLineSegment(sketch, "E425", {"start": v(393.2, 27.07) * mm, "end": v(393.2, -12.89) * mm});
            skLineSegment(sketch, "E426", {"start": v(393.2, -12.89) * mm, "end": v(366.88, -12.89) * mm});
            skLineSegment(sketch, "E427", {"start": v(393.2, 6.37) * mm, "end": v(370.18, 6.37) * mm});
            skLineSegment(sketch, "E428", {"start": v(85.97, -7.57) * mm, "end": v(86.12, -8.02) * mm});
            skLineSegment(sketch, "E429", {"start": v(86.12, -8.02) * mm, "end": v(86.28, -8.46) * mm});
            skLineSegment(sketch, "E430", {"start": v(86.28, -8.46) * mm, "end": v(86.46, -8.9) * mm});
            skLineSegment(sketch, "E431", {"start": v(86.46, -8.9) * mm, "end": v(86.65, -9.33) * mm});
            skLineSegment(sketch, "E432", {"start": v(86.65, -9.33) * mm, "end": v(86.86, -9.75) * mm});
            skLineSegment(sketch, "E433", {"start": v(86.86, -9.75) * mm, "end": v(87.08, -10.17) * mm});
            skLineSegment(sketch, "E434", {"start": v(87.08, -10.17) * mm, "end": v(87.3, -10.58) * mm});
            skLineSegment(sketch, "E435", {"start": v(87.3, -10.58) * mm, "end": v(87.55, -10.98) * mm});
            skLineSegment(sketch, "E436", {"start": v(87.55, -10.98) * mm, "end": v(87.8, -11.38) * mm});
            skLineSegment(sketch, "E437", {"start": v(87.8, -11.38) * mm, "end": v(88.08, -11.76) * mm});
            skLineSegment(sketch, "E438", {"start": v(88.08, -11.76) * mm, "end": v(88.36, -12.14) * mm});
            skLineSegment(sketch, "E439", {"start": v(88.36, -12.14) * mm, "end": v(88.65, -12.5) * mm});
            skLineSegment(sketch, "E440", {"start": v(88.65, -12.5) * mm, "end": v(88.96, -12.87) * mm});
            skLineSegment(sketch, "E441", {"start": v(88.96, -12.87) * mm, "end": v(89.27, -13.22) * mm});
            skLineSegment(sketch, "E442", {"start": v(89.27, -13.22) * mm, "end": v(89.6, -13.56) * mm});
            skLineSegment(sketch, "E443", {"start": v(89.6, -13.56) * mm, "end": v(89.94, -13.89) * mm});
            skLineSegment(sketch, "E444", {"start": v(89.94, -13.89) * mm, "end": v(90.22, -14.15) * mm});
            skLineSegment(sketch, "E445", {"start": v(90.22, -14.15) * mm, "end": v(90.51, -14.4) * mm});
            skLineSegment(sketch, "E446", {"start": v(90.51, -14.4) * mm, "end": v(90.8, -14.65) * mm});
            skLineSegment(sketch, "E447", {"start": v(90.8, -14.65) * mm, "end": v(91.1, -14.9) * mm});
            skLineSegment(sketch, "E448", {"start": v(91.1, -14.9) * mm, "end": v(91.4, -15.12) * mm});
            skLineSegment(sketch, "E449", {"start": v(91.4, -15.12) * mm, "end": v(91.72, -15.34) * mm});
            skLineSegment(sketch, "E450", {"start": v(91.72, -15.34) * mm, "end": v(92.04, -15.56) * mm});
            skLineSegment(sketch, "E451", {"start": v(92.04, -15.56) * mm, "end": v(92.36, -15.76) * mm});
            skLineSegment(sketch, "E452", {"start": v(92.36, -15.76) * mm, "end": v(92.68, -15.96) * mm});
            skLineSegment(sketch, "E453", {"start": v(92.68, -15.96) * mm, "end": v(93.01, -16.15) * mm});
            skLineSegment(sketch, "E454", {"start": v(93.01, -16.15) * mm, "end": v(93.35, -16.33) * mm});
            skLineSegment(sketch, "E455", {"start": v(93.35, -16.33) * mm, "end": v(93.69, -16.5) * mm});
            skLineSegment(sketch, "E456", {"start": v(93.69, -16.5) * mm, "end": v(94.03, -16.66) * mm});
            skLineSegment(sketch, "E457", {"start": v(94.03, -16.66) * mm, "end": v(94.38, -16.81) * mm});
            skLineSegment(sketch, "E458", {"start": v(94.38, -16.81) * mm, "end": v(94.73, -16.96) * mm});
            skLineSegment(sketch, "E459", {"start": v(94.73, -16.96) * mm, "end": v(95.08, -17.1) * mm});
            skLineSegment(sketch, "E460", {"start": v(95.08, -17.1) * mm, "end": v(95.44, -17.22) * mm});
            skLineSegment(sketch, "E461", {"start": v(95.44, -17.22) * mm, "end": v(95.8, -17.34) * mm});
            skLineSegment(sketch, "E462", {"start": v(95.8, -17.34) * mm, "end": v(96.16, -17.45) * mm});
            skLineSegment(sketch, "E463", {"start": v(96.16, -17.45) * mm, "end": v(96.53, -17.54) * mm});
            skLineSegment(sketch, "E464", {"start": v(96.53, -17.54) * mm, "end": v(96.9, -17.63) * mm});
            skLineSegment(sketch, "E465", {"start": v(96.9, -17.63) * mm, "end": v(97.27, -17.71) * mm});
            skLineSegment(sketch, "E466", {"start": v(97.27, -17.71) * mm, "end": v(97.64, -17.79) * mm});
            skLineSegment(sketch, "E467", {"start": v(97.64, -17.79) * mm, "end": v(98.02, -17.85) * mm});
            skLineSegment(sketch, "E468", {"start": v(98.02, -17.85) * mm, "end": v(98.4, -17.9) * mm});
            skLineSegment(sketch, "E469", {"start": v(98.4, -17.9) * mm, "end": v(98.77, -17.94) * mm});
            skLineSegment(sketch, "E470", {"start": v(98.77, -17.94) * mm, "end": v(99.15, -17.97) * mm});
            skLineSegment(sketch, "E471", {"start": v(99.15, -17.97) * mm, "end": v(99.54, -18) * mm});
            skLineSegment(sketch, "E472", {"start": v(99.54, -18) * mm, "end": v(99.92, -18) * mm});
            skLineSegment(sketch, "E473", {"start": v(99.92, -18) * mm, "end": v(100.3, -18.01) * mm});
            skLineSegment(sketch, "E474", {"start": v(100.3, -18.01) * mm, "end": v(100.69, -18) * mm});
            skLineSegment(sketch, "E475", {"start": v(100.69, -18) * mm, "end": v(101.07, -17.99) * mm});
            skLineSegment(sketch, "E476", {"start": v(101.07, -17.99) * mm, "end": v(101.43, -18) * mm});
            skLineSegment(sketch, "E477", {"start": v(101.43, -18) * mm, "end": v(101.78, -18) * mm});
            skLineSegment(sketch, "E478", {"start": v(101.78, -18) * mm, "end": v(102.13, -18) * mm});
            skLineSegment(sketch, "E479", {"start": v(102.13, -18) * mm, "end": v(102.48, -17.98) * mm});
            skLineSegment(sketch, "E480", {"start": v(102.48, -17.98) * mm, "end": v(102.83, -17.95) * mm});
            skLineSegment(sketch, "E481", {"start": v(102.83, -17.95) * mm, "end": v(103.18, -17.91) * mm});
            skLineSegment(sketch, "E482", {"start": v(103.18, -17.91) * mm, "end": v(103.53, -17.87) * mm});
            skLineSegment(sketch, "E483", {"start": v(103.53, -17.87) * mm, "end": v(103.88, -17.82) * mm});
            skLineSegment(sketch, "E484", {"start": v(103.88, -17.82) * mm, "end": v(104.22, -17.76) * mm});
            skLineSegment(sketch, "E485", {"start": v(104.22, -17.76) * mm, "end": v(104.56, -17.69) * mm});
            skLineSegment(sketch, "E486", {"start": v(104.56, -17.69) * mm, "end": v(104.9, -17.6) * mm});
            skLineSegment(sketch, "E487", {"start": v(104.9, -17.6) * mm, "end": v(105.24, -17.52) * mm});
            skLineSegment(sketch, "E488", {"start": v(105.24, -17.52) * mm, "end": v(105.58, -17.42) * mm});
            skLineSegment(sketch, "E489", {"start": v(105.58, -17.42) * mm, "end": v(105.9, -17.32) * mm});
            skLineSegment(sketch, "E490", {"start": v(105.9, -17.32) * mm, "end": v(106.24, -17.2) * mm});
            skLineSegment(sketch, "E491", {"start": v(106.24, -17.2) * mm, "end": v(106.56, -17.08) * mm});
            skLineSegment(sketch, "E492", {"start": v(106.56, -17.08) * mm, "end": v(106.89, -16.95) * mm});
            skLineSegment(sketch, "E493", {"start": v(106.89, -16.95) * mm, "end": v(107.2, -16.82) * mm});
            skLineSegment(sketch, "E494", {"start": v(107.2, -16.82) * mm, "end": v(107.52, -16.67) * mm});
            skLineSegment(sketch, "E495", {"start": v(107.52, -16.67) * mm, "end": v(107.84, -16.52) * mm});
            skLineSegment(sketch, "E496", {"start": v(107.84, -16.52) * mm, "end": v(108.15, -16.35) * mm});
            skLineSegment(sketch, "E497", {"start": v(108.15, -16.35) * mm, "end": v(108.45, -16.18) * mm});
            skLineSegment(sketch, "E498", {"start": v(108.45, -16.18) * mm, "end": v(108.75, -16) * mm});
            skLineSegment(sketch, "E499", {"start": v(108.75, -16) * mm, "end": v(109.05, -15.82) * mm});
            skLineSegment(sketch, "E500", {"start": v(109.05, -15.82) * mm, "end": v(109.34, -15.63) * mm});
            skLineSegment(sketch, "E501", {"start": v(109.34, -15.63) * mm, "end": v(109.63, -15.43) * mm});
            skLineSegment(sketch, "E502", {"start": v(109.63, -15.43) * mm, "end": v(109.9, -15.22) * mm});
            skLineSegment(sketch, "E503", {"start": v(109.9, -15.22) * mm, "end": v(110.19, -15) * mm});
            skLineSegment(sketch, "E504", {"start": v(110.19, -15) * mm, "end": v(110.46, -14.78) * mm});
            skLineSegment(sketch, "E505", {"start": v(110.46, -14.78) * mm, "end": v(110.72, -14.55) * mm});
            skLineSegment(sketch, "E506", {"start": v(110.72, -14.55) * mm, "end": v(110.98, -14.3) * mm});
            skLineSegment(sketch, "E507", {"start": v(110.98, -14.3) * mm, "end": v(111.24, -14.06) * mm});
            skLineSegment(sketch, "E508", {"start": v(111.24, -14.06) * mm, "end": v(111.59, -13.72) * mm});
            skLineSegment(sketch, "E509", {"start": v(111.59, -13.72) * mm, "end": v(111.91, -13.37) * mm});
            skLineSegment(sketch, "E510", {"start": v(111.91, -13.37) * mm, "end": v(112.22, -13) * mm});
            skLineSegment(sketch, "E511", {"start": v(112.22, -13) * mm, "end": v(112.5, -12.62) * mm});
            skLineSegment(sketch, "E512", {"start": v(112.5, -12.62) * mm, "end": v(112.77, -12.23) * mm});
            skLineSegment(sketch, "E513", {"start": v(112.77, -12.23) * mm, "end": v(113.02, -11.83) * mm});
            skLineSegment(sketch, "E514", {"start": v(113.02, -11.83) * mm, "end": v(113.24, -11.43) * mm});
            skLineSegment(sketch, "E515", {"start": v(113.24, -11.43) * mm, "end": v(113.45, -11) * mm});
            skLineSegment(sketch, "E516", {"start": v(113.45, -11) * mm, "end": v(113.64, -10.59) * mm});
            skLineSegment(sketch, "E517", {"start": v(113.64, -10.59) * mm, "end": v(113.8, -10.15) * mm});
            skLineSegment(sketch, "E518", {"start": v(113.8, -10.15) * mm, "end": v(113.95, -9.72) * mm});
            skLineSegment(sketch, "E519", {"start": v(113.95, -9.72) * mm, "end": v(114.07, -9.27) * mm});
            skLineSegment(sketch, "E520", {"start": v(114.07, -9.27) * mm, "end": v(114.18, -8.83) * mm});
            skLineSegment(sketch, "E521", {"start": v(114.18, -8.83) * mm, "end": v(114.26, -8.38) * mm});
            skLineSegment(sketch, "E522", {"start": v(114.26, -8.38) * mm, "end": v(114.33, -7.92) * mm});
            skLineSegment(sketch, "E523", {"start": v(114.33, -7.92) * mm, "end": v(114.37, -7.47) * mm});
            skLineSegment(sketch, "E524", {"start": v(114.37, -7.47) * mm, "end": v(114.4, -7.01) * mm});
            skLineSegment(sketch, "E525", {"start": v(114.4, -7.01) * mm, "end": v(114.4, -6.55) * mm});
            skLineSegment(sketch, "E526", {"start": v(114.4, -6.55) * mm, "end": v(114.37, -6.1) * mm});
            skLineSegment(sketch, "E527", {"start": v(114.37, -6.1) * mm, "end": v(114.34, -5.64) * mm});
            skLineSegment(sketch, "E528", {"start": v(114.34, -5.64) * mm, "end": v(114.28, -5.18) * mm});
            skLineSegment(sketch, "E529", {"start": v(114.28, -5.18) * mm, "end": v(114.2, -4.73) * mm});
            skLineSegment(sketch, "E530", {"start": v(114.2, -4.73) * mm, "end": v(114.1, -4.28) * mm});
            skLineSegment(sketch, "E531", {"start": v(114.1, -4.28) * mm, "end": v(113.97, -3.83) * mm});
            skLineSegment(sketch, "E532", {"start": v(113.97, -3.83) * mm, "end": v(113.83, -3.39) * mm});
            skLineSegment(sketch, "E533", {"start": v(113.83, -3.39) * mm, "end": v(113.66, -2.95) * mm});
            skLineSegment(sketch, "E534", {"start": v(113.66, -2.95) * mm, "end": v(113.47, -2.52) * mm});
            skLineSegment(sketch, "E535", {"start": v(113.47, -2.52) * mm, "end": v(113.27, -2.1) * mm});
            skLineSegment(sketch, "E536", {"start": v(113.27, -2.1) * mm, "end": v(113.04, -1.68) * mm});
            skLineSegment(sketch, "E537", {"start": v(113.04, -1.68) * mm, "end": v(112.79, -1.28) * mm});
            skLineSegment(sketch, "E538", {"start": v(112.79, -1.28) * mm, "end": v(112.52, -0.88) * mm});
            skLineSegment(sketch, "E539", {"start": v(112.52, -0.88) * mm, "end": v(112.22, -0.5) * mm});
            skLineSegment(sketch, "E540", {"start": v(112.22, -0.5) * mm, "end": v(111.93, -0.19) * mm});
            skLineSegment(sketch, "E541", {"start": v(111.93, -0.19) * mm, "end": v(111.63, 0.1) * mm});
            skLineSegment(sketch, "E542", {"start": v(111.63, 0.1) * mm, "end": v(111.32, 0.38) * mm});
            skLineSegment(sketch, "E543", {"start": v(111.32, 0.38) * mm, "end": v(111, 0.66) * mm});
            skLineSegment(sketch, "E544", {"start": v(111, 0.66) * mm, "end": v(110.68, 0.92) * mm});
            skLineSegment(sketch, "E545", {"start": v(110.68, 0.92) * mm, "end": v(110.35, 1.18) * mm});
            skLineSegment(sketch, "E546", {"start": v(110.35, 1.18) * mm, "end": v(110, 1.42) * mm});
            skLineSegment(sketch, "E547", {"start": v(110, 1.42) * mm, "end": v(109.67, 1.66) * mm});
            skLineSegment(sketch, "E548", {"start": v(109.67, 1.66) * mm, "end": v(109.32, 1.88) * mm});
            skLineSegment(sketch, "E549", {"start": v(109.32, 1.88) * mm, "end": v(108.97, 2.1) * mm});
            skLineSegment(sketch, "E550", {"start": v(108.97, 2.1) * mm, "end": v(108.6, 2.3) * mm});
            skLineSegment(sketch, "E551", {"start": v(108.6, 2.3) * mm, "end": v(108.24, 2.5) * mm});
            skLineSegment(sketch, "E552", {"start": v(108.24, 2.5) * mm, "end": v(107.87, 2.7) * mm});
            skLineSegment(sketch, "E553", {"start": v(107.87, 2.7) * mm, "end": v(107.5, 2.87) * mm});
            skLineSegment(sketch, "E554", {"start": v(107.5, 2.87) * mm, "end": v(107.12, 3.04) * mm});
            skLineSegment(sketch, "E555", {"start": v(107.12, 3.04) * mm, "end": v(106.74, 3.2) * mm});
            skLineSegment(sketch, "E556", {"start": v(106.74, 3.2) * mm, "end": v(106.35, 3.34) * mm});
            skLineSegment(sketch, "E557", {"start": v(106.35, 3.34) * mm, "end": v(105.96, 3.48) * mm});
            skLineSegment(sketch, "E558", {"start": v(105.96, 3.48) * mm, "end": v(105.57, 3.6) * mm});
            skLineSegment(sketch, "E559", {"start": v(105.57, 3.6) * mm, "end": v(105.17, 3.72) * mm});
            skLineSegment(sketch, "E560", {"start": v(105.17, 3.72) * mm, "end": v(104.77, 3.83) * mm});
            skLineSegment(sketch, "E561", {"start": v(104.77, 3.83) * mm, "end": v(104.37, 3.92) * mm});
            skLineSegment(sketch, "E562", {"start": v(104.37, 3.92) * mm, "end": v(103.96, 4) * mm});
            skLineSegment(sketch, "E563", {"start": v(103.96, 4) * mm, "end": v(103.55, 4.08) * mm});
            skLineSegment(sketch, "E564", {"start": v(103.55, 4.08) * mm, "end": v(103.14, 4.14) * mm});
            skLineSegment(sketch, "E565", {"start": v(103.14, 4.14) * mm, "end": v(102.73, 4.19) * mm});
            skLineSegment(sketch, "E566", {"start": v(102.73, 4.19) * mm, "end": v(102.31, 4.23) * mm});
            skLineSegment(sketch, "E567", {"start": v(102.31, 4.23) * mm, "end": v(101.9, 4.26) * mm});
            skLineSegment(sketch, "E568", {"start": v(101.9, 4.26) * mm, "end": v(101.48, 4.28) * mm});
            skLineSegment(sketch, "E569", {"start": v(101.48, 4.28) * mm, "end": v(101.06, 4.28) * mm});
            skLineSegment(sketch, "E570", {"start": v(101.06, 4.28) * mm, "end": v(100.64, 4.28) * mm});
            skLineSegment(sketch, "E571", {"start": v(100.64, 4.28) * mm, "end": v(100.22, 4.26) * mm});
            skLineSegment(sketch, "E572", {"start": v(100.22, 4.26) * mm, "end": v(99.66, 4.2) * mm});
            skLineSegment(sketch, "E573", {"start": v(99.66, 4.2) * mm, "end": v(99.1, 4.16) * mm});
            skLineSegment(sketch, "E574", {"start": v(99.1, 4.16) * mm, "end": v(98.55, 4.15) * mm});
            skLineSegment(sketch, "E575", {"start": v(98.55, 4.15) * mm, "end": v(98, 4.17) * mm});
            skLineSegment(sketch, "E576", {"start": v(98, 4.17) * mm, "end": v(97.45, 4.22) * mm});
            skLineSegment(sketch, "E577", {"start": v(97.45, 4.22) * mm, "end": v(96.91, 4.29) * mm});
            skLineSegment(sketch, "E578", {"start": v(96.91, 4.29) * mm, "end": v(96.38, 4.38) * mm});
            skLineSegment(sketch, "E579", {"start": v(96.38, 4.38) * mm, "end": v(95.85, 4.5) * mm});
            skLineSegment(sketch, "E580", {"start": v(95.85, 4.5) * mm, "end": v(95.34, 4.65) * mm});
            skLineSegment(sketch, "E581", {"start": v(95.34, 4.65) * mm, "end": v(94.83, 4.82) * mm});
            skLineSegment(sketch, "E582", {"start": v(94.83, 4.82) * mm, "end": v(94.33, 5.01) * mm});
            skLineSegment(sketch, "E583", {"start": v(94.33, 5.01) * mm, "end": v(93.84, 5.22) * mm});
            skLineSegment(sketch, "E584", {"start": v(93.84, 5.22) * mm, "end": v(93.37, 5.46) * mm});
            skLineSegment(sketch, "E585", {"start": v(93.37, 5.46) * mm, "end": v(92.9, 5.72) * mm});
            skLineSegment(sketch, "E586", {"start": v(92.9, 5.72) * mm, "end": v(92.45, 6) * mm});
            skLineSegment(sketch, "E587", {"start": v(92.45, 6) * mm, "end": v(92.01, 6.3) * mm});
            skLineSegment(sketch, "E588", {"start": v(92.01, 6.3) * mm, "end": v(91.59, 6.62) * mm});
            skLineSegment(sketch, "E589", {"start": v(91.59, 6.62) * mm, "end": v(91.18, 6.95) * mm});
            skLineSegment(sketch, "E590", {"start": v(91.18, 6.95) * mm, "end": v(90.78, 7.31) * mm});
            skLineSegment(sketch, "E591", {"start": v(90.78, 7.31) * mm, "end": v(90.4, 7.69) * mm});
            skLineSegment(sketch, "E592", {"start": v(90.4, 7.69) * mm, "end": v(90.05, 8.08) * mm});
            skLineSegment(sketch, "E593", {"start": v(90.05, 8.08) * mm, "end": v(89.7, 8.49) * mm});
            skLineSegment(sketch, "E594", {"start": v(89.7, 8.49) * mm, "end": v(89.38, 8.92) * mm});
            skLineSegment(sketch, "E595", {"start": v(89.38, 8.92) * mm, "end": v(89.08, 9.36) * mm});
            skLineSegment(sketch, "E596", {"start": v(89.08, 9.36) * mm, "end": v(88.8, 9.82) * mm});
            skLineSegment(sketch, "E597", {"start": v(88.8, 9.82) * mm, "end": v(88.53, 10.29) * mm});
            skLineSegment(sketch, "E598", {"start": v(88.53, 10.29) * mm, "end": v(88.3, 10.78) * mm});
            skLineSegment(sketch, "E599", {"start": v(88.3, 10.78) * mm, "end": v(88.07, 11.28) * mm});
            skLineSegment(sketch, "E600", {"start": v(88.07, 11.28) * mm, "end": v(87.88, 11.8) * mm});
            skLineSegment(sketch, "E601", {"start": v(87.88, 11.8) * mm, "end": v(87.7, 12.32) * mm});
            skLineSegment(sketch, "E602", {"start": v(87.7, 12.32) * mm, "end": v(87.56, 12.86) * mm});
            skLineSegment(sketch, "E603", {"start": v(87.56, 12.86) * mm, "end": v(87.44, 13.41) * mm});
            skLineSegment(sketch, "E604", {"start": v(87.44, 13.41) * mm, "end": v(87.44, 13.87) * mm});
            skLineSegment(sketch, "E605", {"start": v(87.44, 13.87) * mm, "end": v(87.47, 14.32) * mm});
            skLineSegment(sketch, "E606", {"start": v(87.47, 14.32) * mm, "end": v(87.52, 14.77) * mm});
            skLineSegment(sketch, "E607", {"start": v(87.52, 14.77) * mm, "end": v(87.6, 15.22) * mm});
            skLineSegment(sketch, "E608", {"start": v(87.6, 15.22) * mm, "end": v(87.7, 15.66) * mm});
            skLineSegment(sketch, "E609", {"start": v(87.7, 15.66) * mm, "end": v(87.82, 16.09) * mm});
            skLineSegment(sketch, "E610", {"start": v(87.82, 16.09) * mm, "end": v(87.97, 16.51) * mm});
            skLineSegment(sketch, "E611", {"start": v(87.97, 16.51) * mm, "end": v(88.14, 16.93) * mm});
            skLineSegment(sketch, "E612", {"start": v(88.14, 16.93) * mm, "end": v(88.34, 17.33) * mm});
            skLineSegment(sketch, "E613", {"start": v(88.34, 17.33) * mm, "end": v(88.56, 17.72) * mm});
            skLineSegment(sketch, "E614", {"start": v(88.56, 17.72) * mm, "end": v(88.8, 18.1) * mm});
            skLineSegment(sketch, "E615", {"start": v(88.8, 18.1) * mm, "end": v(89.05, 18.47) * mm});
            skLineSegment(sketch, "E616", {"start": v(89.05, 18.47) * mm, "end": v(89.34, 18.82) * mm});
            skLineSegment(sketch, "E617", {"start": v(89.34, 18.82) * mm, "end": v(89.64, 19.16) * mm});
            skLineSegment(sketch, "E618", {"start": v(89.64, 19.16) * mm, "end": v(89.96, 19.48) * mm});
            skLineSegment(sketch, "E619", {"start": v(89.96, 19.48) * mm, "end": v(90.3, 19.79) * mm});
            skLineSegment(sketch, "E620", {"start": v(90.3, 19.79) * mm, "end": v(90.58, 20.04) * mm});
            skLineSegment(sketch, "E621", {"start": v(90.58, 20.04) * mm, "end": v(90.86, 20.28) * mm});
            skLineSegment(sketch, "E622", {"start": v(90.86, 20.28) * mm, "end": v(91.15, 20.5) * mm});
            skLineSegment(sketch, "E623", {"start": v(91.15, 20.5) * mm, "end": v(91.45, 20.73) * mm});
            skLineSegment(sketch, "E624", {"start": v(91.45, 20.73) * mm, "end": v(91.75, 20.95) * mm});
            skLineSegment(sketch, "E625", {"start": v(91.75, 20.95) * mm, "end": v(92.05, 21.16) * mm});
            skLineSegment(sketch, "E626", {"start": v(92.05, 21.16) * mm, "end": v(92.36, 21.36) * mm});
            skLineSegment(sketch, "E627", {"start": v(92.36, 21.36) * mm, "end": v(92.68, 21.55) * mm});
            skLineSegment(sketch, "E628", {"start": v(92.68, 21.55) * mm, "end": v(93, 21.74) * mm});
            skLineSegment(sketch, "E629", {"start": v(93, 21.74) * mm, "end": v(93.32, 21.92) * mm});
            skLineSegment(sketch, "E630", {"start": v(93.32, 21.92) * mm, "end": v(93.65, 22.09) * mm});
            skLineSegment(sketch, "E631", {"start": v(93.65, 22.09) * mm, "end": v(93.98, 22.25) * mm});
            skLineSegment(sketch, "E632", {"start": v(93.98, 22.25) * mm, "end": v(94.32, 22.4) * mm});
            skLineSegment(sketch, "E633", {"start": v(94.32, 22.4) * mm, "end": v(94.66, 22.54) * mm});
            skLineSegment(sketch, "E634", {"start": v(94.66, 22.54) * mm, "end": v(95, 22.68) * mm});
            skLineSegment(sketch, "E635", {"start": v(95, 22.68) * mm, "end": v(95.35, 22.8) * mm});
            skLineSegment(sketch, "E636", {"start": v(95.35, 22.8) * mm, "end": v(95.7, 22.92) * mm});
            skLineSegment(sketch, "E637", {"start": v(95.7, 22.92) * mm, "end": v(96.05, 23.03) * mm});
            skLineSegment(sketch, "E638", {"start": v(96.05, 23.03) * mm, "end": v(96.4, 23.13) * mm});
            skLineSegment(sketch, "E639", {"start": v(96.4, 23.13) * mm, "end": v(96.76, 23.22) * mm});
            skLineSegment(sketch, "E640", {"start": v(96.76, 23.22) * mm, "end": v(97.12, 23.3) * mm});
            skLineSegment(sketch, "E641", {"start": v(97.12, 23.3) * mm, "end": v(97.48, 23.37) * mm});
            skLineSegment(sketch, "E642", {"start": v(97.48, 23.37) * mm, "end": v(97.84, 23.44) * mm});
            skLineSegment(sketch, "E643", {"start": v(97.84, 23.44) * mm, "end": v(98.2, 23.5) * mm});
            skLineSegment(sketch, "E644", {"start": v(98.2, 23.5) * mm, "end": v(98.57, 23.54) * mm});
            skLineSegment(sketch, "E645", {"start": v(98.57, 23.54) * mm, "end": v(98.94, 23.58) * mm});
            skLineSegment(sketch, "E646", {"start": v(98.94, 23.58) * mm, "end": v(99.31, 23.6) * mm});
            skLineSegment(sketch, "E647", {"start": v(99.31, 23.6) * mm, "end": v(99.68, 23.62) * mm});
            skLineSegment(sketch, "E648", {"start": v(99.68, 23.62) * mm, "end": v(100.05, 23.63) * mm});
            skLineSegment(sketch, "E649", {"start": v(100.05, 23.63) * mm, "end": v(100.42, 23.63) * mm});
            skLineSegment(sketch, "E650", {"start": v(100.42, 23.63) * mm, "end": v(100.8, 23.62) * mm});
            skLineSegment(sketch, "E651", {"start": v(100.8, 23.62) * mm, "end": v(101.17, 23.6) * mm});
            skLineSegment(sketch, "E652", {"start": v(101.17, 23.6) * mm, "end": v(101.5, 23.6) * mm});
            skLineSegment(sketch, "E653", {"start": v(101.5, 23.6) * mm, "end": v(101.83, 23.6) * mm});
            skLineSegment(sketch, "E654", {"start": v(101.83, 23.6) * mm, "end": v(102.15, 23.6) * mm});
            skLineSegment(sketch, "E655", {"start": v(102.15, 23.6) * mm, "end": v(102.48, 23.57) * mm});
            skLineSegment(sketch, "E656", {"start": v(102.48, 23.57) * mm, "end": v(102.8, 23.54) * mm});
            skLineSegment(sketch, "E657", {"start": v(102.8, 23.54) * mm, "end": v(103.13, 23.5) * mm});
            skLineSegment(sketch, "E658", {"start": v(103.13, 23.5) * mm, "end": v(103.45, 23.47) * mm});
            skLineSegment(sketch, "E659", {"start": v(103.45, 23.47) * mm, "end": v(103.77, 23.41) * mm});
            skLineSegment(sketch, "E660", {"start": v(103.77, 23.41) * mm, "end": v(104.1, 23.36) * mm});
            skLineSegment(sketch, "E661", {"start": v(104.1, 23.36) * mm, "end": v(104.41, 23.29) * mm});
            skLineSegment(sketch, "E662", {"start": v(104.41, 23.29) * mm, "end": v(104.73, 23.22) * mm});
            skLineSegment(sketch, "E663", {"start": v(104.73, 23.22) * mm, "end": v(105.04, 23.13) * mm});
            skLineSegment(sketch, "E664", {"start": v(105.04, 23.13) * mm, "end": v(105.35, 23.05) * mm});
            skLineSegment(sketch, "E665", {"start": v(105.35, 23.05) * mm, "end": v(105.66, 22.95) * mm});
            skLineSegment(sketch, "E666", {"start": v(105.66, 22.95) * mm, "end": v(105.97, 22.85) * mm});
            skLineSegment(sketch, "E667", {"start": v(105.97, 22.85) * mm, "end": v(106.27, 22.73) * mm});
            skLineSegment(sketch, "E668", {"start": v(106.27, 22.73) * mm, "end": v(106.58, 22.62) * mm});
            skLineSegment(sketch, "E669", {"start": v(106.58, 22.62) * mm, "end": v(106.88, 22.5) * mm});
            skLineSegment(sketch, "E670", {"start": v(106.88, 22.5) * mm, "end": v(107.17, 22.36) * mm});
            skLineSegment(sketch, "E671", {"start": v(107.17, 22.36) * mm, "end": v(107.46, 22.22) * mm});
            skLineSegment(sketch, "E672", {"start": v(107.46, 22.22) * mm, "end": v(107.75, 22.07) * mm});
            skLineSegment(sketch, "E673", {"start": v(107.75, 22.07) * mm, "end": v(108.04, 21.92) * mm});
            skLineSegment(sketch, "E674", {"start": v(108.04, 21.92) * mm, "end": v(108.32, 21.76) * mm});
            skLineSegment(sketch, "E675", {"start": v(108.32, 21.76) * mm, "end": v(108.6, 21.6) * mm});
            skLineSegment(sketch, "E676", {"start": v(108.6, 21.6) * mm, "end": v(108.88, 21.42) * mm});
            skLineSegment(sketch, "E677", {"start": v(108.88, 21.42) * mm, "end": v(109.15, 21.24) * mm});
            skLineSegment(sketch, "E678", {"start": v(109.15, 21.24) * mm, "end": v(109.41, 21.05) * mm});
            skLineSegment(sketch, "E679", {"start": v(109.41, 21.05) * mm, "end": v(109.68, 20.85) * mm});
            skLineSegment(sketch, "E680", {"start": v(109.68, 20.85) * mm, "end": v(109.93, 20.65) * mm});
            skLineSegment(sketch, "E681", {"start": v(109.93, 20.65) * mm, "end": v(110.19, 20.45) * mm});
            skLineSegment(sketch, "E682", {"start": v(110.19, 20.45) * mm, "end": v(110.44, 20.23) * mm});
            skLineSegment(sketch, "E683", {"start": v(110.44, 20.23) * mm, "end": v(110.68, 20.01) * mm});
            skLineSegment(sketch, "E684", {"start": v(110.68, 20.01) * mm, "end": v(110.98, 19.68) * mm});
            skLineSegment(sketch, "E685", {"start": v(110.98, 19.68) * mm, "end": v(111.26, 19.35) * mm});
            skLineSegment(sketch, "E686", {"start": v(111.26, 19.35) * mm, "end": v(111.54, 19) * mm});
            skLineSegment(sketch, "E687", {"start": v(111.54, 19) * mm, "end": v(111.8, 18.65) * mm});
            skLineSegment(sketch, "E688", {"start": v(111.8, 18.65) * mm, "end": v(112.05, 18.28) * mm});
            skLineSegment(sketch, "E689", {"start": v(112.05, 18.28) * mm, "end": v(112.29, 17.91) * mm});
            skLineSegment(sketch, "E690", {"start": v(112.29, 17.91) * mm, "end": v(112.5, 17.53) * mm});
            skLineSegment(sketch, "E691", {"start": v(112.5, 17.53) * mm, "end": v(112.72, 17.14) * mm});
            skLineSegment(sketch, "E692", {"start": v(112.72, 17.14) * mm, "end": v(112.91, 16.75) * mm});
            skLineSegment(sketch, "E693", {"start": v(112.91, 16.75) * mm, "end": v(113.1, 16.35) * mm});
            skLineSegment(sketch, "E694", {"start": v(113.1, 16.35) * mm, "end": v(113.27, 15.94) * mm});
            skLineSegment(sketch, "E695", {"start": v(113.27, 15.94) * mm, "end": v(113.42, 15.53) * mm});
            skLineSegment(sketch, "E696", {"start": v(113.42, 15.53) * mm, "end": v(113.56, 15.11) * mm});
            skLineSegment(sketch, "E697", {"start": v(113.56, 15.11) * mm, "end": v(113.69, 14.69) * mm});
            skLineSegment(sketch, "E698", {"start": v(113.69, 14.69) * mm, "end": v(113.8, 14.26) * mm});
            skLineSegment(sketch, "E699", {"start": v(113.8, 14.26) * mm, "end": v(113.9, 13.83) * mm});
            skLineSegment(sketch, "E700", {"start": v(123.36, -17.16) * mm, "end": v(123.36, 22.79) * mm});
            skLineSegment(sketch, "E701", {"start": v(132.16, -17.16) * mm, "end": v(132.16, 22.81) * mm});
            skLineSegment(sketch, "E702", {"start": v(132.16, 22.81) * mm, "end": v(146.82, 22.81) * mm});
            skLineSegment(sketch, "E703", {"start": v(146.82, 22.81) * mm, "end": v(147.17, 22.8) * mm});
            skLineSegment(sketch, "E704", {"start": v(147.17, 22.8) * mm, "end": v(147.51, 22.77) * mm});
            skLineSegment(sketch, "E705", {"start": v(147.51, 22.77) * mm, "end": v(147.86, 22.74) * mm});
            skLineSegment(sketch, "E706", {"start": v(147.86, 22.74) * mm, "end": v(148.2, 22.7) * mm});
            skLineSegment(sketch, "E707", {"start": v(148.2, 22.7) * mm, "end": v(148.54, 22.64) * mm});
            skLineSegment(sketch, "E708", {"start": v(148.54, 22.64) * mm, "end": v(148.88, 22.58) * mm});
            skLineSegment(sketch, "E709", {"start": v(148.88, 22.58) * mm, "end": v(149.22, 22.51) * mm});
            skLineSegment(sketch, "E710", {"start": v(149.22, 22.51) * mm, "end": v(149.55, 22.44) * mm});
            skLineSegment(sketch, "E711", {"start": v(149.55, 22.44) * mm, "end": v(149.89, 22.35) * mm});
            skLineSegment(sketch, "E712", {"start": v(149.89, 22.35) * mm, "end": v(150.22, 22.26) * mm});
            skLineSegment(sketch, "E713", {"start": v(150.22, 22.26) * mm, "end": v(150.54, 22.16) * mm});
            skLineSegment(sketch, "E714", {"start": v(150.54, 22.16) * mm, "end": v(150.87, 22.05) * mm});
            skLineSegment(sketch, "E715", {"start": v(150.87, 22.05) * mm, "end": v(151.2, 21.93) * mm});
            skLineSegment(sketch, "E716", {"start": v(151.2, 21.93) * mm, "end": v(151.5, 21.8) * mm});
            skLineSegment(sketch, "E717", {"start": v(151.5, 21.8) * mm, "end": v(151.82, 21.67) * mm});
            skLineSegment(sketch, "E718", {"start": v(151.82, 21.67) * mm, "end": v(152.14, 21.53) * mm});
            skLineSegment(sketch, "E719", {"start": v(152.14, 21.53) * mm, "end": v(152.45, 21.38) * mm});
            skLineSegment(sketch, "E720", {"start": v(152.45, 21.38) * mm, "end": v(152.75, 21.22) * mm});
            skLineSegment(sketch, "E721", {"start": v(152.75, 21.22) * mm, "end": v(153.05, 21.06) * mm});
            skLineSegment(sketch, "E722", {"start": v(153.05, 21.06) * mm, "end": v(153.35, 20.89) * mm});
            skLineSegment(sketch, "E723", {"start": v(153.35, 20.89) * mm, "end": v(153.64, 20.7) * mm});
            skLineSegment(sketch, "E724", {"start": v(153.64, 20.7) * mm, "end": v(153.93, 20.52) * mm});
            skLineSegment(sketch, "E725", {"start": v(153.93, 20.52) * mm, "end": v(154.2, 20.33) * mm});
            skLineSegment(sketch, "E726", {"start": v(154.2, 20.33) * mm, "end": v(154.49, 20.12) * mm});
            skLineSegment(sketch, "E727", {"start": v(154.49, 20.12) * mm, "end": v(154.76, 19.92) * mm});
            skLineSegment(sketch, "E728", {"start": v(154.76, 19.92) * mm, "end": v(155.03, 19.7) * mm});
            skLineSegment(sketch, "E729", {"start": v(155.03, 19.7) * mm, "end": v(155.3, 19.48) * mm});
            skLineSegment(sketch, "E730", {"start": v(155.3, 19.48) * mm, "end": v(155.55, 19.25) * mm});
            skLineSegment(sketch, "E731", {"start": v(155.55, 19.25) * mm, "end": v(155.8, 19.01) * mm});
            skLineSegment(sketch, "E732", {"start": v(155.8, 19.01) * mm, "end": v(156.05, 18.77) * mm});
            skLineSegment(sketch, "E733", {"start": v(156.05, 18.77) * mm, "end": v(156.3, 18.52) * mm});
            skLineSegment(sketch, "E734", {"start": v(156.3, 18.52) * mm, "end": v(156.53, 18.26) * mm});
            skLineSegment(sketch, "E735", {"start": v(156.53, 18.26) * mm, "end": v(156.93, 17.85) * mm});
            skLineSegment(sketch, "E736", {"start": v(156.93, 17.85) * mm, "end": v(157.32, 17.43) * mm});
            skLineSegment(sketch, "E737", {"start": v(157.32, 17.43) * mm, "end": v(157.7, 17) * mm});
            skLineSegment(sketch, "E738", {"start": v(157.7, 17) * mm, "end": v(158.06, 16.56) * mm});
            skLineSegment(sketch, "E739", {"start": v(158.06, 16.56) * mm, "end": v(158.42, 16.11) * mm});
            skLineSegment(sketch, "E740", {"start": v(158.42, 16.11) * mm, "end": v(158.76, 15.66) * mm});
            skLineSegment(sketch, "E741", {"start": v(158.76, 15.66) * mm, "end": v(159.09, 15.2) * mm});
            skLineSegment(sketch, "E742", {"start": v(159.09, 15.2) * mm, "end": v(159.4, 14.72) * mm});
            skLineSegment(sketch, "E743", {"start": v(159.4, 14.72) * mm, "end": v(159.71, 14.24) * mm});
            skLineSegment(sketch, "E744", {"start": v(159.71, 14.24) * mm, "end": v(160, 13.76) * mm});
            skLineSegment(sketch, "E745", {"start": v(160, 13.76) * mm, "end": v(160.29, 13.26) * mm});
            skLineSegment(sketch, "E746", {"start": v(160.29, 13.26) * mm, "end": v(160.56, 12.77) * mm});
            skLineSegment(sketch, "E747", {"start": v(160.56, 12.77) * mm, "end": v(160.81, 12.26) * mm});
            skLineSegment(sketch, "E748", {"start": v(160.81, 12.26) * mm, "end": v(161.06, 11.75) * mm});
            skLineSegment(sketch, "E749", {"start": v(161.06, 11.75) * mm, "end": v(161.29, 11.23) * mm});
            skLineSegment(sketch, "E750", {"start": v(161.29, 11.23) * mm, "end": v(161.5, 10.7) * mm});
            skLineSegment(sketch, "E751", {"start": v(161.5, 10.7) * mm, "end": v(161.71, 10.18) * mm});
            skLineSegment(sketch, "E752", {"start": v(161.71, 10.18) * mm, "end": v(161.9, 9.65) * mm});
            skLineSegment(sketch, "E753", {"start": v(161.9, 9.65) * mm, "end": v(162.08, 9.1) * mm});
            skLineSegment(sketch, "E754", {"start": v(162.08, 9.1) * mm, "end": v(162.25, 8.57) * mm});
            skLineSegment(sketch, "E755", {"start": v(162.25, 8.57) * mm, "end": v(162.4, 8.02) * mm});
            skLineSegment(sketch, "E756", {"start": v(162.4, 8.02) * mm, "end": v(162.54, 7.47) * mm});
            skLineSegment(sketch, "E757", {"start": v(162.54, 7.47) * mm, "end": v(162.66, 6.92) * mm});
            skLineSegment(sketch, "E758", {"start": v(162.66, 6.92) * mm, "end": v(162.77, 6.36) * mm});
            skLineSegment(sketch, "E759", {"start": v(162.77, 6.36) * mm, "end": v(162.87, 5.8) * mm});
            skLineSegment(sketch, "E760", {"start": v(162.87, 5.8) * mm, "end": v(162.95, 5.23) * mm});
            skLineSegment(sketch, "E761", {"start": v(162.95, 5.23) * mm, "end": v(163.02, 4.67) * mm});
            skLineSegment(sketch, "E762", {"start": v(163.02, 4.67) * mm, "end": v(163.07, 4.1) * mm});
            skLineSegment(sketch, "E763", {"start": v(163.07, 4.1) * mm, "end": v(163.11, 3.53) * mm});
            skLineSegment(sketch, "E764", {"start": v(163.11, 3.53) * mm, "end": v(163.14, 2.96) * mm});
            skLineSegment(sketch, "E765", {"start": v(163.14, 2.96) * mm, "end": v(163.15, 2.38) * mm});
            skLineSegment(sketch, "E766", {"start": v(163.15, 2.38) * mm, "end": v(163.14, 1.8) * mm});
            skLineSegment(sketch, "E767", {"start": v(163.14, 1.8) * mm, "end": v(163.16, 1.33) * mm});
            skLineSegment(sketch, "E768", {"start": v(163.16, 1.33) * mm, "end": v(163.15, 0.85) * mm});
            skLineSegment(sketch, "E769", {"start": v(163.15, 0.85) * mm, "end": v(163.14, 0.37) * mm});
            skLineSegment(sketch, "E770", {"start": v(163.14, 0.37) * mm, "end": v(163.12, -0.11) * mm});
            skLineSegment(sketch, "E771", {"start": v(163.12, -0.11) * mm, "end": v(163.08, -0.6) * mm});
            skLineSegment(sketch, "E772", {"start": v(163.08, -0.6) * mm, "end": v(163.03, -1.07) * mm});
            skLineSegment(sketch, "E773", {"start": v(163.03, -1.07) * mm, "end": v(162.97, -1.54) * mm});
            skLineSegment(sketch, "E774", {"start": v(162.97, -1.54) * mm, "end": v(162.9, -2.01) * mm});
            skLineSegment(sketch, "E775", {"start": v(162.9, -2.01) * mm, "end": v(162.82, -2.48) * mm});
            skLineSegment(sketch, "E776", {"start": v(162.82, -2.48) * mm, "end": v(162.73, -2.95) * mm});
            skLineSegment(sketch, "E777", {"start": v(162.73, -2.95) * mm, "end": v(162.62, -3.41) * mm});
            skLineSegment(sketch, "E778", {"start": v(162.62, -3.41) * mm, "end": v(162.5, -3.87) * mm});
            skLineSegment(sketch, "E779", {"start": v(162.5, -3.87) * mm, "end": v(162.38, -4.33) * mm});
            skLineSegment(sketch, "E780", {"start": v(162.38, -4.33) * mm, "end": v(162.24, -4.79) * mm});
            skLineSegment(sketch, "E781", {"start": v(162.24, -4.79) * mm, "end": v(162.09, -5.24) * mm});
            skLineSegment(sketch, "E782", {"start": v(162.09, -5.24) * mm, "end": v(161.93, -5.68) * mm});
            skLineSegment(sketch, "E783", {"start": v(161.93, -5.68) * mm, "end": v(161.76, -6.13) * mm});
            skLineSegment(sketch, "E784", {"start": v(161.76, -6.13) * mm, "end": v(161.57, -6.57) * mm});
            skLineSegment(sketch, "E785", {"start": v(161.57, -6.57) * mm, "end": v(161.38, -7) * mm});
            skLineSegment(sketch, "E786", {"start": v(161.38, -7) * mm, "end": v(161.18, -7.43) * mm});
            skLineSegment(sketch, "E787", {"start": v(161.18, -7.43) * mm, "end": v(160.96, -7.85) * mm});
            skLineSegment(sketch, "E788", {"start": v(160.96, -7.85) * mm, "end": v(160.74, -8.27) * mm});
            skLineSegment(sketch, "E789", {"start": v(160.74, -8.27) * mm, "end": v(160.5, -8.69) * mm});
            skLineSegment(sketch, "E790", {"start": v(160.5, -8.69) * mm, "end": v(160.26, -9.1) * mm});
            skLineSegment(sketch, "E791", {"start": v(160.26, -9.1) * mm, "end": v(160, -9.5) * mm});
            skLineSegment(sketch, "E792", {"start": v(160, -9.5) * mm, "end": v(159.74, -9.9) * mm});
            skLineSegment(sketch, "E793", {"start": v(159.74, -9.9) * mm, "end": v(159.46, -10.29) * mm});
            skLineSegment(sketch, "E794", {"start": v(159.46, -10.29) * mm, "end": v(159.17, -10.67) * mm});
            skLineSegment(sketch, "E795", {"start": v(159.17, -10.67) * mm, "end": v(158.88, -11.05) * mm});
            skLineSegment(sketch, "E796", {"start": v(158.88, -11.05) * mm, "end": v(158.57, -11.42) * mm});
            skLineSegment(sketch, "E797", {"start": v(158.57, -11.42) * mm, "end": v(158.26, -11.78) * mm});
            skLineSegment(sketch, "E798", {"start": v(158.26, -11.78) * mm, "end": v(157.93, -12.14) * mm});
            skLineSegment(sketch, "E799", {"start": v(157.93, -12.14) * mm, "end": v(157.66, -12.42) * mm});
            skLineSegment(sketch, "E800", {"start": v(157.66, -12.42) * mm, "end": v(157.38, -12.7) * mm});
            skLineSegment(sketch, "E801", {"start": v(157.38, -12.7) * mm, "end": v(157.1, -12.97) * mm});
            skLineSegment(sketch, "E802", {"start": v(157.1, -12.97) * mm, "end": v(156.8, -13.23) * mm});
            skLineSegment(sketch, "E803", {"start": v(156.8, -13.23) * mm, "end": v(156.5, -13.48) * mm});
            skLineSegment(sketch, "E804", {"start": v(156.5, -13.48) * mm, "end": v(156.2, -13.73) * mm});
            skLineSegment(sketch, "E805", {"start": v(156.2, -13.73) * mm, "end": v(155.89, -13.97) * mm});
            skLineSegment(sketch, "E806", {"start": v(155.89, -13.97) * mm, "end": v(155.57, -14.2) * mm});
            skLineSegment(sketch, "E807", {"start": v(155.57, -14.2) * mm, "end": v(155.25, -14.42) * mm});
            skLineSegment(sketch, "E808", {"start": v(155.25, -14.42) * mm, "end": v(154.92, -14.64) * mm});
            skLineSegment(sketch, "E809", {"start": v(154.92, -14.64) * mm, "end": v(154.6, -14.84) * mm});
            skLineSegment(sketch, "E810", {"start": v(154.6, -14.84) * mm, "end": v(154.26, -15.04) * mm});
            skLineSegment(sketch, "E811", {"start": v(154.26, -15.04) * mm, "end": v(153.92, -15.23) * mm});
            skLineSegment(sketch, "E812", {"start": v(153.92, -15.23) * mm, "end": v(153.57, -15.41) * mm});
            skLineSegment(sketch, "E813", {"start": v(153.57, -15.41) * mm, "end": v(153.23, -15.59) * mm});
            skLineSegment(sketch, "E814", {"start": v(153.23, -15.59) * mm, "end": v(152.87, -15.75) * mm});
            skLineSegment(sketch, "E815", {"start": v(152.87, -15.75) * mm, "end": v(152.52, -15.9) * mm});
            skLineSegment(sketch, "E816", {"start": v(152.52, -15.9) * mm, "end": v(152.16, -16.05) * mm});
            skLineSegment(sketch, "E817", {"start": v(152.16, -16.05) * mm, "end": v(151.8, -16.2) * mm});
            skLineSegment(sketch, "E818", {"start": v(151.8, -16.2) * mm, "end": v(151.43, -16.32) * mm});
            skLineSegment(sketch, "E819", {"start": v(151.43, -16.32) * mm, "end": v(151.06, -16.44) * mm});
            skLineSegment(sketch, "E820", {"start": v(151.06, -16.44) * mm, "end": v(150.68, -16.56) * mm});
            skLineSegment(sketch, "E821", {"start": v(150.68, -16.56) * mm, "end": v(150.3, -16.66) * mm});
            skLineSegment(sketch, "E822", {"start": v(150.3, -16.66) * mm, "end": v(149.93, -16.75) * mm});
            skLineSegment(sketch, "E823", {"start": v(149.93, -16.75) * mm, "end": v(149.54, -16.84) * mm});
            skLineSegment(sketch, "E824", {"start": v(149.54, -16.84) * mm, "end": v(149.16, -16.91) * mm});
            skLineSegment(sketch, "E825", {"start": v(149.16, -16.91) * mm, "end": v(148.78, -16.98) * mm});
            skLineSegment(sketch, "E826", {"start": v(148.78, -16.98) * mm, "end": v(148.39, -17.03) * mm});
            skLineSegment(sketch, "E827", {"start": v(148.39, -17.03) * mm, "end": v(148, -17.08) * mm});
            skLineSegment(sketch, "E828", {"start": v(148, -17.08) * mm, "end": v(147.6, -17.12) * mm});
            skLineSegment(sketch, "E829", {"start": v(147.6, -17.12) * mm, "end": v(147.21, -17.15) * mm});
            skLineSegment(sketch, "E830", {"start": v(147.21, -17.15) * mm, "end": v(146.82, -17.16) * mm});
            skLineSegment(sketch, "E831", {"start": v(146.82, -17.16) * mm, "end": v(132.16, -17.16) * mm});
            skLineSegment(sketch, "E832", {"start": v(198.48, -17.16) * mm, "end": v(172.17, -17.16) * mm});
            skLineSegment(sketch, "E833", {"start": v(172.17, -17.16) * mm, "end": v(172.17, 22.8) * mm});
            skLineSegment(sketch, "E834", {"start": v(172.17, 22.8) * mm, "end": v(198.48, 22.8) * mm});
            skLineSegment(sketch, "E835", {"start": v(172.17, 3.54) * mm, "end": v(195.18, 3.54) * mm});
            skLineSegment(sketch, "E836", {"start": v(-148.27, 190.25) * mm, "end": v(-108.3, 190.25) * mm});
            skLineSegment(sketch, "E837", {"start": v(-108.3, 190.25) * mm, "end": v(-108.3, 172.7) * mm});
            skLineSegment(sketch, "E838", {"start": v(-108.3, 172.7) * mm, "end": v(-108.3, 172.2) * mm});
            skLineSegment(sketch, "E839", {"start": v(-108.3, 172.2) * mm, "end": v(-108.34, 171.71) * mm});
            skLineSegment(sketch, "E840", {"start": v(-108.34, 171.71) * mm, "end": v(-108.4, 171.22) * mm});
            skLineSegment(sketch, "E841", {"start": v(-108.4, 171.22) * mm, "end": v(-108.47, 170.74) * mm});
            skLineSegment(sketch, "E842", {"start": v(-108.47, 170.74) * mm, "end": v(-108.57, 170.26) * mm});
            skLineSegment(sketch, "E843", {"start": v(-108.57, 170.26) * mm, "end": v(-108.7, 169.8) * mm});
            skLineSegment(sketch, "E844", {"start": v(-108.7, 169.8) * mm, "end": v(-108.85, 169.33) * mm});
            skLineSegment(sketch, "E845", {"start": v(-108.85, 169.33) * mm, "end": v(-109.03, 168.87) * mm});
            skLineSegment(sketch, "E846", {"start": v(-109.03, 168.87) * mm, "end": v(-109.22, 168.43) * mm});
            skLineSegment(sketch, "E847", {"start": v(-109.22, 168.43) * mm, "end": v(-109.44, 168) * mm});
            skLineSegment(sketch, "E848", {"start": v(-109.44, 168) * mm, "end": v(-109.68, 167.57) * mm});
            skLineSegment(sketch, "E849", {"start": v(-109.68, 167.57) * mm, "end": v(-109.95, 167.16) * mm});
            skLineSegment(sketch, "E850", {"start": v(-109.95, 167.16) * mm, "end": v(-110.23, 166.76) * mm});
            skLineSegment(sketch, "E851", {"start": v(-110.23, 166.76) * mm, "end": v(-110.54, 166.38) * mm});
            skLineSegment(sketch, "E852", {"start": v(-110.54, 166.38) * mm, "end": v(-110.86, 166) * mm});
            skLineSegment(sketch, "E853", {"start": v(-110.86, 166) * mm, "end": v(-111.2, 165.65) * mm});
            skLineSegment(sketch, "E854", {"start": v(-111.2, 165.65) * mm, "end": v(-111.56, 165.31) * mm});
            skLineSegment(sketch, "E855", {"start": v(-111.56, 165.31) * mm, "end": v(-111.93, 165) * mm});
            skLineSegment(sketch, "E856", {"start": v(-111.93, 165) * mm, "end": v(-112.3, 164.7) * mm});
            skLineSegment(sketch, "E857", {"start": v(-112.3, 164.7) * mm, "end": v(-112.7, 164.41) * mm});
            skLineSegment(sketch, "E858", {"start": v(-112.7, 164.41) * mm, "end": v(-113.11, 164.15) * mm});
            skLineSegment(sketch, "E859", {"start": v(-113.11, 164.15) * mm, "end": v(-113.53, 163.9) * mm});
            skLineSegment(sketch, "E860", {"start": v(-113.53, 163.9) * mm, "end": v(-113.96, 163.7) * mm});
            skLineSegment(sketch, "E861", {"start": v(-113.96, 163.7) * mm, "end": v(-114.4, 163.5) * mm});
            skLineSegment(sketch, "E862", {"start": v(-114.4, 163.5) * mm, "end": v(-114.85, 163.32) * mm});
            skLineSegment(sketch, "E863", {"start": v(-114.85, 163.32) * mm, "end": v(-115.3, 163.17) * mm});
            skLineSegment(sketch, "E864", {"start": v(-115.3, 163.17) * mm, "end": v(-115.78, 163.04) * mm});
            skLineSegment(sketch, "E865", {"start": v(-115.78, 163.04) * mm, "end": v(-116.25, 162.93) * mm});
            skLineSegment(sketch, "E866", {"start": v(-116.25, 162.93) * mm, "end": v(-116.73, 162.84) * mm});
            skLineSegment(sketch, "E867", {"start": v(-116.73, 162.84) * mm, "end": v(-117.2, 162.78) * mm});
            skLineSegment(sketch, "E868", {"start": v(-117.2, 162.78) * mm, "end": v(-117.7, 162.75) * mm});
            skLineSegment(sketch, "E869", {"start": v(-117.7, 162.75) * mm, "end": v(-118.18, 162.74) * mm});
            skLineSegment(sketch, "E870", {"start": v(-118.18, 162.74) * mm, "end": v(-118.69, 162.73) * mm});
            skLineSegment(sketch, "E871", {"start": v(-118.69, 162.73) * mm, "end": v(-119.18, 162.76) * mm});
            skLineSegment(sketch, "E872", {"start": v(-119.18, 162.76) * mm, "end": v(-119.68, 162.8) * mm});
            skLineSegment(sketch, "E873", {"start": v(-119.68, 162.8) * mm, "end": v(-120.17, 162.88) * mm});
            skLineSegment(sketch, "E874", {"start": v(-120.17, 162.88) * mm, "end": v(-120.66, 162.98) * mm});
            skLineSegment(sketch, "E875", {"start": v(-120.66, 162.98) * mm, "end": v(-121.14, 163.1) * mm});
            skLineSegment(sketch, "E876", {"start": v(-121.14, 163.1) * mm, "end": v(-121.6, 163.24) * mm});
            skLineSegment(sketch, "E877", {"start": v(-121.6, 163.24) * mm, "end": v(-122.07, 163.41) * mm});
            skLineSegment(sketch, "E878", {"start": v(-122.07, 163.41) * mm, "end": v(-122.53, 163.6) * mm});
            skLineSegment(sketch, "E879", {"start": v(-122.53, 163.6) * mm, "end": v(-122.97, 163.82) * mm});
            skLineSegment(sketch, "E880", {"start": v(-122.97, 163.82) * mm, "end": v(-123.4, 164.06) * mm});
            skLineSegment(sketch, "E881", {"start": v(-123.4, 164.06) * mm, "end": v(-123.83, 164.32) * mm});
            skLineSegment(sketch, "E882", {"start": v(-123.83, 164.32) * mm, "end": v(-124.24, 164.6) * mm});
            skLineSegment(sketch, "E883", {"start": v(-124.24, 164.6) * mm, "end": v(-124.63, 164.9) * mm});
            skLineSegment(sketch, "E884", {"start": v(-124.63, 164.9) * mm, "end": v(-125.01, 165.23) * mm});
            skLineSegment(sketch, "E885", {"start": v(-125.01, 165.23) * mm, "end": v(-125.38, 165.57) * mm});
            skLineSegment(sketch, "E886", {"start": v(-125.38, 165.57) * mm, "end": v(-125.72, 165.93) * mm});
            skLineSegment(sketch, "E887", {"start": v(-125.72, 165.93) * mm, "end": v(-126.05, 166.31) * mm});
            skLineSegment(sketch, "E888", {"start": v(-126.05, 166.31) * mm, "end": v(-126.35, 166.7) * mm});
            skLineSegment(sketch, "E889", {"start": v(-126.35, 166.7) * mm, "end": v(-126.63, 167.1) * mm});
            skLineSegment(sketch, "E890", {"start": v(-126.63, 167.1) * mm, "end": v(-126.9, 167.52) * mm});
            skLineSegment(sketch, "E891", {"start": v(-126.9, 167.52) * mm, "end": v(-127.14, 167.95) * mm});
            skLineSegment(sketch, "E892", {"start": v(-127.14, 167.95) * mm, "end": v(-127.35, 168.4) * mm});
            skLineSegment(sketch, "E893", {"start": v(-127.35, 168.4) * mm, "end": v(-127.55, 168.84) * mm});
            skLineSegment(sketch, "E894", {"start": v(-127.55, 168.84) * mm, "end": v(-127.72, 169.3) * mm});
            skLineSegment(sketch, "E895", {"start": v(-127.72, 169.3) * mm, "end": v(-127.88, 169.77) * mm});
            skLineSegment(sketch, "E896", {"start": v(-127.88, 169.77) * mm, "end": v(-128, 170.24) * mm});
            skLineSegment(sketch, "E897", {"start": v(-128, 170.24) * mm, "end": v(-128.1, 170.73) * mm});
            skLineSegment(sketch, "E898", {"start": v(-128.1, 170.73) * mm, "end": v(-128.19, 171.21) * mm});
            skLineSegment(sketch, "E899", {"start": v(-128.19, 171.21) * mm, "end": v(-128.24, 171.7) * mm});
            skLineSegment(sketch, "E900", {"start": v(-128.24, 171.7) * mm, "end": v(-128.27, 172.2) * mm});
            skLineSegment(sketch, "E901", {"start": v(-128.27, 172.2) * mm, "end": v(-128.28, 172.7) * mm});
            skLineSegment(sketch, "E902", {"start": v(-128.28, 172.7) * mm, "end": v(-128.28, 190.25) * mm});
            skLineSegment(sketch, "E903", {"start": v(-128.28, 172.7) * mm, "end": v(-128.28, 172.29) * mm});
            skLineSegment(sketch, "E904", {"start": v(-128.28, 172.29) * mm, "end": v(-128.3, 171.88) * mm});
            skLineSegment(sketch, "E905", {"start": v(-128.3, 171.88) * mm, "end": v(-128.35, 171.48) * mm});
            skLineSegment(sketch, "E906", {"start": v(-128.35, 171.48) * mm, "end": v(-128.4, 171.07) * mm});
            skLineSegment(sketch, "E907", {"start": v(-128.4, 171.07) * mm, "end": v(-128.5, 170.68) * mm});
            skLineSegment(sketch, "E908", {"start": v(-128.5, 170.68) * mm, "end": v(-128.6, 170.29) * mm});
            skLineSegment(sketch, "E909", {"start": v(-128.6, 170.29) * mm, "end": v(-128.72, 169.9) * mm});
            skLineSegment(sketch, "E910", {"start": v(-128.72, 169.9) * mm, "end": v(-128.86, 169.53) * mm});
            skLineSegment(sketch, "E911", {"start": v(-128.86, 169.53) * mm, "end": v(-129.03, 169.16) * mm});
            skLineSegment(sketch, "E912", {"start": v(-129.03, 169.16) * mm, "end": v(-129.2, 168.8) * mm});
            skLineSegment(sketch, "E913", {"start": v(-129.2, 168.8) * mm, "end": v(-129.4, 168.44) * mm});
            skLineSegment(sketch, "E914", {"start": v(-129.4, 168.44) * mm, "end": v(-129.62, 168.1) * mm});
            skLineSegment(sketch, "E915", {"start": v(-129.62, 168.1) * mm, "end": v(-129.86, 167.77) * mm});
            skLineSegment(sketch, "E916", {"start": v(-129.86, 167.77) * mm, "end": v(-130.1, 167.45) * mm});
            skLineSegment(sketch, "E917", {"start": v(-130.1, 167.45) * mm, "end": v(-130.38, 167.14) * mm});
            skLineSegment(sketch, "E918", {"start": v(-130.38, 167.14) * mm, "end": v(-130.66, 166.85) * mm});
            skLineSegment(sketch, "E919", {"start": v(-130.66, 166.85) * mm, "end": v(-131.16, 166.5) * mm});
            skLineSegment(sketch, "E920", {"start": v(-131.16, 166.5) * mm, "end": v(-131.67, 166.19) * mm});
            skLineSegment(sketch, "E921", {"start": v(-131.67, 166.19) * mm, "end": v(-132.2, 165.9) * mm});
            skLineSegment(sketch, "E922", {"start": v(-132.2, 165.9) * mm, "end": v(-132.74, 165.63) * mm});
            skLineSegment(sketch, "E923", {"start": v(-132.74, 165.63) * mm, "end": v(-133.28, 165.38) * mm});
            skLineSegment(sketch, "E924", {"start": v(-133.28, 165.38) * mm, "end": v(-133.84, 165.16) * mm});
            skLineSegment(sketch, "E925", {"start": v(-133.84, 165.16) * mm, "end": v(-134.4, 164.97) * mm});
            skLineSegment(sketch, "E926", {"start": v(-134.4, 164.97) * mm, "end": v(-134.98, 164.8) * mm});
            skLineSegment(sketch, "E927", {"start": v(-134.98, 164.8) * mm, "end": v(-135.56, 164.65) * mm});
            skLineSegment(sketch, "E928", {"start": v(-135.56, 164.65) * mm, "end": v(-136.15, 164.54) * mm});
            skLineSegment(sketch, "E929", {"start": v(-136.15, 164.54) * mm, "end": v(-136.74, 164.44) * mm});
            skLineSegment(sketch, "E930", {"start": v(-136.74, 164.44) * mm, "end": v(-137.34, 164.38) * mm});
            skLineSegment(sketch, "E931", {"start": v(-137.34, 164.38) * mm, "end": v(-137.94, 164.34) * mm});
            skLineSegment(sketch, "E932", {"start": v(-137.94, 164.34) * mm, "end": v(-138.54, 164.33) * mm});
            skLineSegment(sketch, "E933", {"start": v(-138.54, 164.33) * mm, "end": v(-139.14, 164.34) * mm});
            skLineSegment(sketch, "E934", {"start": v(-139.14, 164.34) * mm, "end": v(-139.75, 164.38) * mm});
            skLineSegment(sketch, "E935", {"start": v(-139.75, 164.38) * mm, "end": v(-140.28, 164.4) * mm});
            skLineSegment(sketch, "E936", {"start": v(-140.28, 164.4) * mm, "end": v(-140.82, 164.4) * mm});
            skLineSegment(sketch, "E937", {"start": v(-140.82, 164.4) * mm, "end": v(-141.36, 164.38) * mm});
            skLineSegment(sketch, "E938", {"start": v(-141.36, 164.38) * mm, "end": v(-141.9, 164.36) * mm});
            skLineSegment(sketch, "E939", {"start": v(-141.9, 164.36) * mm, "end": v(-142.44, 164.33) * mm});
            skLineSegment(sketch, "E940", {"start": v(-142.44, 164.33) * mm, "end": v(-142.97, 164.29) * mm});
            skLineSegment(sketch, "E941", {"start": v(-142.97, 164.29) * mm, "end": v(-143.5, 164.24) * mm});
            skLineSegment(sketch, "E942", {"start": v(-143.5, 164.24) * mm, "end": v(-144.04, 164.18) * mm});
            skLineSegment(sketch, "E943", {"start": v(-144.04, 164.18) * mm, "end": v(-144.58, 164.1) * mm});
            skLineSegment(sketch, "E944", {"start": v(-144.58, 164.1) * mm, "end": v(-145.11, 164.03) * mm});
            skLineSegment(sketch, "E945", {"start": v(-145.11, 164.03) * mm, "end": v(-145.64, 163.94) * mm});
            skLineSegment(sketch, "E946", {"start": v(-145.64, 163.94) * mm, "end": v(-146.17, 163.84) * mm});
            skLineSegment(sketch, "E947", {"start": v(-146.17, 163.84) * mm, "end": v(-146.7, 163.73) * mm});
            skLineSegment(sketch, "E948", {"start": v(-146.7, 163.73) * mm, "end": v(-147.22, 163.62) * mm});
            skLineSegment(sketch, "E949", {"start": v(-147.22, 163.62) * mm, "end": v(-147.75, 163.49) * mm});
            skLineSegment(sketch, "E950", {"start": v(-147.75, 163.49) * mm, "end": v(-148.27, 163.35) * mm});
            skLineSegment(sketch, "E951", {"start": v(-148.83, 137.45) * mm, "end": v(-148.83, 137.87) * mm});
            skLineSegment(sketch, "E952", {"start": v(-148.83, 137.87) * mm, "end": v(-148.82, 138.29) * mm});
            skLineSegment(sketch, "E953", {"start": v(-148.82, 138.29) * mm, "end": v(-148.8, 138.7) * mm});
            skLineSegment(sketch, "E954", {"start": v(-148.8, 138.7) * mm, "end": v(-148.78, 139.12) * mm});
            skLineSegment(sketch, "E955", {"start": v(-148.78, 139.12) * mm, "end": v(-148.74, 139.54) * mm});
            skLineSegment(sketch, "E956", {"start": v(-148.74, 139.54) * mm, "end": v(-148.69, 139.95) * mm});
            skLineSegment(sketch, "E957", {"start": v(-148.69, 139.95) * mm, "end": v(-148.63, 140.36) * mm});
            skLineSegment(sketch, "E958", {"start": v(-148.63, 140.36) * mm, "end": v(-148.56, 140.77) * mm});
            skLineSegment(sketch, "E959", {"start": v(-148.56, 140.77) * mm, "end": v(-148.48, 141.18) * mm});
            skLineSegment(sketch, "E960", {"start": v(-148.48, 141.18) * mm, "end": v(-148.4, 141.58) * mm});
            skLineSegment(sketch, "E961", {"start": v(-148.4, 141.58) * mm, "end": v(-148.3, 141.99) * mm});
            skLineSegment(sketch, "E962", {"start": v(-148.3, 141.99) * mm, "end": v(-148.18, 142.39) * mm});
            skLineSegment(sketch, "E963", {"start": v(-148.18, 142.39) * mm, "end": v(-148.06, 142.78) * mm});
            skLineSegment(sketch, "E964", {"start": v(-148.06, 142.78) * mm, "end": v(-147.93, 143.18) * mm});
            skLineSegment(sketch, "E965", {"start": v(-147.93, 143.18) * mm, "end": v(-147.8, 143.57) * mm});
            skLineSegment(sketch, "E966", {"start": v(-147.8, 143.57) * mm, "end": v(-147.65, 143.95) * mm});
            skLineSegment(sketch, "E967", {"start": v(-147.65, 143.95) * mm, "end": v(-147.49, 144.33) * mm});
            skLineSegment(sketch, "E968", {"start": v(-147.49, 144.33) * mm, "end": v(-147.32, 144.71) * mm});
            skLineSegment(sketch, "E969", {"start": v(-147.32, 144.71) * mm, "end": v(-147.14, 145.09) * mm});
            skLineSegment(sketch, "E970", {"start": v(-147.14, 145.09) * mm, "end": v(-146.96, 145.46) * mm});
            skLineSegment(sketch, "E971", {"start": v(-146.96, 145.46) * mm, "end": v(-146.76, 145.82) * mm});
            skLineSegment(sketch, "E972", {"start": v(-146.76, 145.82) * mm, "end": v(-146.56, 146.18) * mm});
            skLineSegment(sketch, "E973", {"start": v(-146.56, 146.18) * mm, "end": v(-146.35, 146.54) * mm});
            skLineSegment(sketch, "E974", {"start": v(-146.35, 146.54) * mm, "end": v(-146.12, 146.89) * mm});
            skLineSegment(sketch, "E975", {"start": v(-146.12, 146.89) * mm, "end": v(-145.9, 147.23) * mm});
            skLineSegment(sketch, "E976", {"start": v(-145.9, 147.23) * mm, "end": v(-145.65, 147.57) * mm});
            skLineSegment(sketch, "E977", {"start": v(-145.65, 147.57) * mm, "end": v(-145.4, 147.9) * mm});
            skLineSegment(sketch, "E978", {"start": v(-145.4, 147.9) * mm, "end": v(-145.15, 148.23) * mm});
            skLineSegment(sketch, "E979", {"start": v(-145.15, 148.23) * mm, "end": v(-144.88, 148.56) * mm});
            skLineSegment(sketch, "E980", {"start": v(-144.88, 148.56) * mm, "end": v(-144.6, 148.87) * mm});
            skLineSegment(sketch, "E981", {"start": v(-144.6, 148.87) * mm, "end": v(-144.32, 149.18) * mm});
            skLineSegment(sketch, "E982", {"start": v(-144.32, 149.18) * mm, "end": v(-144.03, 149.48) * mm});
            skLineSegment(sketch, "E983", {"start": v(-144.03, 149.48) * mm, "end": v(-143.65, 149.83) * mm});
            skLineSegment(sketch, "E984", {"start": v(-143.65, 149.83) * mm, "end": v(-143.26, 150.17) * mm});
            skLineSegment(sketch, "E985", {"start": v(-143.26, 150.17) * mm, "end": v(-142.87, 150.5) * mm});
            skLineSegment(sketch, "E986", {"start": v(-142.87, 150.5) * mm, "end": v(-142.46, 150.82) * mm});
            skLineSegment(sketch, "E987", {"start": v(-142.46, 150.82) * mm, "end": v(-142.05, 151.13) * mm});
            skLineSegment(sketch, "E988", {"start": v(-142.05, 151.13) * mm, "end": v(-141.64, 151.43) * mm});
            skLineSegment(sketch, "E989", {"start": v(-141.64, 151.43) * mm, "end": v(-141.21, 151.71) * mm});
            skLineSegment(sketch, "E990", {"start": v(-141.21, 151.71) * mm, "end": v(-140.78, 151.99) * mm});
            skLineSegment(sketch, "E991", {"start": v(-140.78, 151.99) * mm, "end": v(-140.34, 152.25) * mm});
            skLineSegment(sketch, "E992", {"start": v(-140.34, 152.25) * mm, "end": v(-139.9, 152.5) * mm});
            skLineSegment(sketch, "E993", {"start": v(-139.9, 152.5) * mm, "end": v(-139.45, 152.75) * mm});
            skLineSegment(sketch, "E994", {"start": v(-139.45, 152.75) * mm, "end": v(-139, 152.98) * mm});
            skLineSegment(sketch, "E995", {"start": v(-139, 152.98) * mm, "end": v(-138.54, 153.2) * mm});
            skLineSegment(sketch, "E996", {"start": v(-138.54, 153.2) * mm, "end": v(-138.07, 153.4) * mm});
            skLineSegment(sketch, "E997", {"start": v(-138.07, 153.4) * mm, "end": v(-137.6, 153.6) * mm});
            skLineSegment(sketch, "E998", {"start": v(-137.6, 153.6) * mm, "end": v(-137.13, 153.8) * mm});
            skLineSegment(sketch, "E999", {"start": v(-137.13, 153.8) * mm, "end": v(-136.65, 153.96) * mm});
            skLineSegment(sketch, "E1000", {"start": v(-136.65, 153.96) * mm, "end": v(-136.17, 154.13) * mm});
            skLineSegment(sketch, "E1001", {"start": v(-136.17, 154.13) * mm, "end": v(-135.68, 154.28) * mm});
            skLineSegment(sketch, "E1002", {"start": v(-135.68, 154.28) * mm, "end": v(-135.2, 154.42) * mm});
            skLineSegment(sketch, "E1003", {"start": v(-135.2, 154.42) * mm, "end": v(-134.7, 154.54) * mm});
            skLineSegment(sketch, "E1004", {"start": v(-134.7, 154.54) * mm, "end": v(-134.2, 154.66) * mm});
            skLineSegment(sketch, "E1005", {"start": v(-134.2, 154.66) * mm, "end": v(-133.7, 154.76) * mm});
            skLineSegment(sketch, "E1006", {"start": v(-133.7, 154.76) * mm, "end": v(-133.2, 154.85) * mm});
            skLineSegment(sketch, "E1007", {"start": v(-133.2, 154.85) * mm, "end": v(-132.7, 154.92) * mm});
            skLineSegment(sketch, "E1008", {"start": v(-132.7, 154.92) * mm, "end": v(-132.18, 154.99) * mm});
            skLineSegment(sketch, "E1009", {"start": v(-132.18, 154.99) * mm, "end": v(-131.67, 155.04) * mm});
            skLineSegment(sketch, "E1010", {"start": v(-131.67, 155.04) * mm, "end": v(-131.16, 155.08) * mm});
            skLineSegment(sketch, "E1011", {"start": v(-131.16, 155.08) * mm, "end": v(-130.65, 155.1) * mm});
            skLineSegment(sketch, "E1012", {"start": v(-130.65, 155.1) * mm, "end": v(-130.13, 155.12) * mm});
            skLineSegment(sketch, "E1013", {"start": v(-130.13, 155.12) * mm, "end": v(-129.62, 155.12) * mm});
            skLineSegment(sketch, "E1014", {"start": v(-129.62, 155.12) * mm, "end": v(-129.1, 155.11) * mm});
            skLineSegment(sketch, "E1015", {"start": v(-129.1, 155.11) * mm, "end": v(-128.54, 155.13) * mm});
            skLineSegment(sketch, "E1016", {"start": v(-128.54, 155.13) * mm, "end": v(-127.98, 155.13) * mm});
            skLineSegment(sketch, "E1017", {"start": v(-127.98, 155.13) * mm, "end": v(-127.42, 155.12) * mm});
            skLineSegment(sketch, "E1018", {"start": v(-127.42, 155.12) * mm, "end": v(-126.86, 155.09) * mm});
            skLineSegment(sketch, "E1019", {"start": v(-126.86, 155.09) * mm, "end": v(-126.3, 155.05) * mm});
            skLineSegment(sketch, "E1020", {"start": v(-126.3, 155.05) * mm, "end": v(-125.75, 155) * mm});
            skLineSegment(sketch, "E1021", {"start": v(-125.75, 155) * mm, "end": v(-125.2, 154.93) * mm});
            skLineSegment(sketch, "E1022", {"start": v(-125.2, 154.93) * mm, "end": v(-124.65, 154.84) * mm});
            skLineSegment(sketch, "E1023", {"start": v(-124.65, 154.84) * mm, "end": v(-124.1, 154.75) * mm});
            skLineSegment(sketch, "E1024", {"start": v(-124.1, 154.75) * mm, "end": v(-123.56, 154.64) * mm});
            skLineSegment(sketch, "E1025", {"start": v(-123.56, 154.64) * mm, "end": v(-123.02, 154.52) * mm});
            skLineSegment(sketch, "E1026", {"start": v(-123.02, 154.52) * mm, "end": v(-122.49, 154.38) * mm});
            skLineSegment(sketch, "E1027", {"start": v(-122.49, 154.38) * mm, "end": v(-121.95, 154.23) * mm});
            skLineSegment(sketch, "E1028", {"start": v(-121.95, 154.23) * mm, "end": v(-121.42, 154.07) * mm});
            skLineSegment(sketch, "E1029", {"start": v(-121.42, 154.07) * mm, "end": v(-120.9, 153.9) * mm});
            skLineSegment(sketch, "E1030", {"start": v(-120.9, 153.9) * mm, "end": v(-120.38, 153.7) * mm});
            skLineSegment(sketch, "E1031", {"start": v(-120.38, 153.7) * mm, "end": v(-119.86, 153.5) * mm});
            skLineSegment(sketch, "E1032", {"start": v(-119.86, 153.5) * mm, "end": v(-119.35, 153.3) * mm});
            skLineSegment(sketch, "E1033", {"start": v(-119.35, 153.3) * mm, "end": v(-118.85, 153.07) * mm});
            skLineSegment(sketch, "E1034", {"start": v(-118.85, 153.07) * mm, "end": v(-118.35, 152.83) * mm});
            skLineSegment(sketch, "E1035", {"start": v(-118.35, 152.83) * mm, "end": v(-117.86, 152.58) * mm});
            skLineSegment(sketch, "E1036", {"start": v(-117.86, 152.58) * mm, "end": v(-117.37, 152.31) * mm});
            skLineSegment(sketch, "E1037", {"start": v(-117.37, 152.31) * mm, "end": v(-116.9, 152.04) * mm});
            skLineSegment(sketch, "E1038", {"start": v(-116.9, 152.04) * mm, "end": v(-116.42, 151.75) * mm});
            skLineSegment(sketch, "E1039", {"start": v(-116.42, 151.75) * mm, "end": v(-115.95, 151.45) * mm});
            skLineSegment(sketch, "E1040", {"start": v(-115.95, 151.45) * mm, "end": v(-115.49, 151.14) * mm});
            skLineSegment(sketch, "E1041", {"start": v(-115.49, 151.14) * mm, "end": v(-115.04, 150.81) * mm});
            skLineSegment(sketch, "E1042", {"start": v(-115.04, 150.81) * mm, "end": v(-114.6, 150.48) * mm});
            skLineSegment(sketch, "E1043", {"start": v(-114.6, 150.48) * mm, "end": v(-114.15, 150.13) * mm});
            skLineSegment(sketch, "E1044", {"start": v(-114.15, 150.13) * mm, "end": v(-113.73, 149.77) * mm});
            skLineSegment(sketch, "E1045", {"start": v(-113.73, 149.77) * mm, "end": v(-113.3, 149.4) * mm});
            skLineSegment(sketch, "E1046", {"start": v(-113.3, 149.4) * mm, "end": v(-112.9, 149.02) * mm});
            skLineSegment(sketch, "E1047", {"start": v(-112.9, 149.02) * mm, "end": v(-112.6, 148.73) * mm});
            skLineSegment(sketch, "E1048", {"start": v(-112.6, 148.73) * mm, "end": v(-112.32, 148.44) * mm});
            skLineSegment(sketch, "E1049", {"start": v(-112.32, 148.44) * mm, "end": v(-112.05, 148.14) * mm});
            skLineSegment(sketch, "E1050", {"start": v(-112.05, 148.14) * mm, "end": v(-111.78, 147.84) * mm});
            skLineSegment(sketch, "E1051", {"start": v(-111.78, 147.84) * mm, "end": v(-111.52, 147.52) * mm});
            skLineSegment(sketch, "E1052", {"start": v(-111.52, 147.52) * mm, "end": v(-111.27, 147.2) * mm});
            skLineSegment(sketch, "E1053", {"start": v(-111.27, 147.2) * mm, "end": v(-111.03, 146.88) * mm});
            skLineSegment(sketch, "E1054", {"start": v(-111.03, 146.88) * mm, "end": v(-110.8, 146.55) * mm});
            skLineSegment(sketch, "E1055", {"start": v(-110.8, 146.55) * mm, "end": v(-110.58, 146.22) * mm});
            skLineSegment(sketch, "E1056", {"start": v(-110.58, 146.22) * mm, "end": v(-110.37, 145.88) * mm});
            skLineSegment(sketch, "E1057", {"start": v(-110.37, 145.88) * mm, "end": v(-110.16, 145.53) * mm});
            skLineSegment(sketch, "E1058", {"start": v(-110.16, 145.53) * mm, "end": v(-109.96, 145.18) * mm});
            skLineSegment(sketch, "E1059", {"start": v(-109.96, 145.18) * mm, "end": v(-109.78, 144.83) * mm});
            skLineSegment(sketch, "E1060", {"start": v(-109.78, 144.83) * mm, "end": v(-109.6, 144.47) * mm});
            skLineSegment(sketch, "E1061", {"start": v(-109.6, 144.47) * mm, "end": v(-109.43, 144.1) * mm});
            skLineSegment(sketch, "E1062", {"start": v(-109.43, 144.1) * mm, "end": v(-109.27, 143.73) * mm});
            skLineSegment(sketch, "E1063", {"start": v(-109.27, 143.73) * mm, "end": v(-109.12, 143.36) * mm});
            skLineSegment(sketch, "E1064", {"start": v(-109.12, 143.36) * mm, "end": v(-108.98, 142.99) * mm});
            skLineSegment(sketch, "E1065", {"start": v(-108.98, 142.99) * mm, "end": v(-108.85, 142.6) * mm});
            skLineSegment(sketch, "E1066", {"start": v(-108.85, 142.6) * mm, "end": v(-108.73, 142.22) * mm});
            skLineSegment(sketch, "E1067", {"start": v(-108.73, 142.22) * mm, "end": v(-108.62, 141.84) * mm});
            skLineSegment(sketch, "E1068", {"start": v(-108.62, 141.84) * mm, "end": v(-108.52, 141.45) * mm});
            skLineSegment(sketch, "E1069", {"start": v(-108.52, 141.45) * mm, "end": v(-108.43, 141.06) * mm});
            skLineSegment(sketch, "E1070", {"start": v(-108.43, 141.06) * mm, "end": v(-108.35, 140.66) * mm});
            skLineSegment(sketch, "E1071", {"start": v(-108.35, 140.66) * mm, "end": v(-108.28, 140.27) * mm});
            skLineSegment(sketch, "E1072", {"start": v(-108.28, 140.27) * mm, "end": v(-108.21, 139.87) * mm});
            skLineSegment(sketch, "E1073", {"start": v(-108.21, 139.87) * mm, "end": v(-108.16, 139.47) * mm});
            skLineSegment(sketch, "E1074", {"start": v(-108.16, 139.47) * mm, "end": v(-108.12, 139.06) * mm});
            skLineSegment(sketch, "E1075", {"start": v(-108.12, 139.06) * mm, "end": v(-108.1, 138.66) * mm});
            skLineSegment(sketch, "E1076", {"start": v(-108.1, 138.66) * mm, "end": v(-108.07, 138.26) * mm});
            skLineSegment(sketch, "E1077", {"start": v(-108.07, 138.26) * mm, "end": v(-108.06, 137.85) * mm});
            skLineSegment(sketch, "E1078", {"start": v(-108.06, 137.85) * mm, "end": v(-108.07, 137.44) * mm});
            skLineSegment(sketch, "E1079", {"start": v(-108.07, 137.44) * mm, "end": v(-108.07, 137.03) * mm});
            skLineSegment(sketch, "E1080", {"start": v(-108.07, 137.03) * mm, "end": v(-108.08, 136.61) * mm});
            skLineSegment(sketch, "E1081", {"start": v(-108.08, 136.61) * mm, "end": v(-108.1, 136.2) * mm});
            skLineSegment(sketch, "E1082", {"start": v(-108.1, 136.2) * mm, "end": v(-108.15, 135.8) * mm});
            skLineSegment(sketch, "E1083", {"start": v(-108.15, 135.8) * mm, "end": v(-108.2, 135.38) * mm});
            skLineSegment(sketch, "E1084", {"start": v(-108.2, 135.38) * mm, "end": v(-108.25, 134.98) * mm});
            skLineSegment(sketch, "E1085", {"start": v(-108.25, 134.98) * mm, "end": v(-108.32, 134.57) * mm});
            skLineSegment(sketch, "E1086", {"start": v(-108.32, 134.57) * mm, "end": v(-108.4, 134.17) * mm});
            skLineSegment(sketch, "E1087", {"start": v(-108.4, 134.17) * mm, "end": v(-108.48, 133.77) * mm});
            skLineSegment(sketch, "E1088", {"start": v(-108.48, 133.77) * mm, "end": v(-108.58, 133.37) * mm});
            skLineSegment(sketch, "E1089", {"start": v(-108.58, 133.37) * mm, "end": v(-108.69, 132.98) * mm});
            skLineSegment(sketch, "E1090", {"start": v(-108.69, 132.98) * mm, "end": v(-108.8, 132.59) * mm});
            skLineSegment(sketch, "E1091", {"start": v(-108.8, 132.59) * mm, "end": v(-108.93, 132.2) * mm});
            skLineSegment(sketch, "E1092", {"start": v(-108.93, 132.2) * mm, "end": v(-109.07, 131.82) * mm});
            skLineSegment(sketch, "E1093", {"start": v(-109.07, 131.82) * mm, "end": v(-109.22, 131.44) * mm});
            skLineSegment(sketch, "E1094", {"start": v(-109.22, 131.44) * mm, "end": v(-109.37, 131.06) * mm});
            skLineSegment(sketch, "E1095", {"start": v(-109.37, 131.06) * mm, "end": v(-109.54, 130.69) * mm});
            skLineSegment(sketch, "E1096", {"start": v(-109.54, 130.69) * mm, "end": v(-109.71, 130.32) * mm});
            skLineSegment(sketch, "E1097", {"start": v(-109.71, 130.32) * mm, "end": v(-109.9, 129.96) * mm});
            skLineSegment(sketch, "E1098", {"start": v(-109.9, 129.96) * mm, "end": v(-110.1, 129.6) * mm});
            skLineSegment(sketch, "E1099", {"start": v(-110.1, 129.6) * mm, "end": v(-110.3, 129.24) * mm});
            skLineSegment(sketch, "E1100", {"start": v(-110.3, 129.24) * mm, "end": v(-110.5, 128.9) * mm});
            skLineSegment(sketch, "E1101", {"start": v(-110.5, 128.9) * mm, "end": v(-110.73, 128.55) * mm});
            skLineSegment(sketch, "E1102", {"start": v(-110.73, 128.55) * mm, "end": v(-110.96, 128.21) * mm});
            skLineSegment(sketch, "E1103", {"start": v(-110.96, 128.21) * mm, "end": v(-111.2, 127.88) * mm});
            skLineSegment(sketch, "E1104", {"start": v(-111.2, 127.88) * mm, "end": v(-111.45, 127.56) * mm});
            skLineSegment(sketch, "E1105", {"start": v(-111.45, 127.56) * mm, "end": v(-111.7, 127.23) * mm});
            skLineSegment(sketch, "E1106", {"start": v(-111.7, 127.23) * mm, "end": v(-111.97, 126.92) * mm});
            skLineSegment(sketch, "E1107", {"start": v(-111.97, 126.92) * mm, "end": v(-112.25, 126.61) * mm});
            skLineSegment(sketch, "E1108", {"start": v(-112.25, 126.61) * mm, "end": v(-112.53, 126.31) * mm});
            skLineSegment(sketch, "E1109", {"start": v(-112.53, 126.31) * mm, "end": v(-112.82, 126.02) * mm});
            skLineSegment(sketch, "E1110", {"start": v(-112.82, 126.02) * mm, "end": v(-113.12, 125.73) * mm});
            skLineSegment(sketch, "E1111", {"start": v(-113.12, 125.73) * mm, "end": v(-113.53, 125.36) * mm});
            skLineSegment(sketch, "E1112", {"start": v(-113.53, 125.36) * mm, "end": v(-113.94, 125) * mm});
            skLineSegment(sketch, "E1113", {"start": v(-113.94, 125) * mm, "end": v(-114.37, 124.65) * mm});
            skLineSegment(sketch, "E1114", {"start": v(-114.37, 124.65) * mm, "end": v(-114.8, 124.32) * mm});
            skLineSegment(sketch, "E1115", {"start": v(-114.8, 124.32) * mm, "end": v(-115.25, 124) * mm});
            skLineSegment(sketch, "E1116", {"start": v(-115.25, 124) * mm, "end": v(-115.7, 123.68) * mm});
            skLineSegment(sketch, "E1117", {"start": v(-115.7, 123.68) * mm, "end": v(-116.15, 123.38) * mm});
            skLineSegment(sketch, "E1118", {"start": v(-116.15, 123.38) * mm, "end": v(-116.61, 123.09) * mm});
            skLineSegment(sketch, "E1119", {"start": v(-116.61, 123.09) * mm, "end": v(-117.08, 122.81) * mm});
            skLineSegment(sketch, "E1120", {"start": v(-117.08, 122.81) * mm, "end": v(-117.56, 122.54) * mm});
            skLineSegment(sketch, "E1121", {"start": v(-117.56, 122.54) * mm, "end": v(-118.04, 122.3) * mm});
            skLineSegment(sketch, "E1122", {"start": v(-118.04, 122.3) * mm, "end": v(-118.53, 122.05) * mm});
            skLineSegment(sketch, "E1123", {"start": v(-118.53, 122.05) * mm, "end": v(-119.02, 121.82) * mm});
            skLineSegment(sketch, "E1124", {"start": v(-119.02, 121.82) * mm, "end": v(-119.52, 121.6) * mm});
            skLineSegment(sketch, "E1125", {"start": v(-119.52, 121.6) * mm, "end": v(-120.03, 121.4) * mm});
            skLineSegment(sketch, "E1126", {"start": v(-120.03, 121.4) * mm, "end": v(-120.53, 121.2) * mm});
            skLineSegment(sketch, "E1127", {"start": v(-120.53, 121.2) * mm, "end": v(-121.05, 121.02) * mm});
            skLineSegment(sketch, "E1128", {"start": v(-121.05, 121.02) * mm, "end": v(-121.57, 120.86) * mm});
            skLineSegment(sketch, "E1129", {"start": v(-121.57, 120.86) * mm, "end": v(-122.09, 120.7) * mm});
            skLineSegment(sketch, "E1130", {"start": v(-122.09, 120.7) * mm, "end": v(-122.61, 120.56) * mm});
            skLineSegment(sketch, "E1131", {"start": v(-122.61, 120.56) * mm, "end": v(-123.14, 120.43) * mm});
            skLineSegment(sketch, "E1132", {"start": v(-123.14, 120.43) * mm, "end": v(-123.67, 120.32) * mm});
            skLineSegment(sketch, "E1133", {"start": v(-123.67, 120.32) * mm, "end": v(-124.2, 120.21) * mm});
            skLineSegment(sketch, "E1134", {"start": v(-124.2, 120.21) * mm, "end": v(-124.75, 120.12) * mm});
            skLineSegment(sketch, "E1135", {"start": v(-124.75, 120.12) * mm, "end": v(-125.29, 120.05) * mm});
            skLineSegment(sketch, "E1136", {"start": v(-125.29, 120.05) * mm, "end": v(-125.83, 119.99) * mm});
            skLineSegment(sketch, "E1137", {"start": v(-125.83, 119.99) * mm, "end": v(-126.38, 119.94) * mm});
            skLineSegment(sketch, "E1138", {"start": v(-126.38, 119.94) * mm, "end": v(-126.92, 119.9) * mm});
            skLineSegment(sketch, "E1139", {"start": v(-126.92, 119.9) * mm, "end": v(-127.47, 119.88) * mm});
            skLineSegment(sketch, "E1140", {"start": v(-127.47, 119.88) * mm, "end": v(-128.02, 119.87) * mm});
            skLineSegment(sketch, "E1141", {"start": v(-128.02, 119.87) * mm, "end": v(-128.57, 119.88) * mm});
            skLineSegment(sketch, "E1142", {"start": v(-128.57, 119.88) * mm, "end": v(-129.13, 119.9) * mm});
            skLineSegment(sketch, "E1143", {"start": v(-129.13, 119.9) * mm, "end": v(-129.64, 119.89) * mm});
            skLineSegment(sketch, "E1144", {"start": v(-129.64, 119.89) * mm, "end": v(-130.15, 119.9) * mm});
            skLineSegment(sketch, "E1145", {"start": v(-130.15, 119.9) * mm, "end": v(-130.67, 119.91) * mm});
            skLineSegment(sketch, "E1146", {"start": v(-130.67, 119.91) * mm, "end": v(-131.18, 119.94) * mm});
            skLineSegment(sketch, "E1147", {"start": v(-131.18, 119.94) * mm, "end": v(-131.69, 119.98) * mm});
            skLineSegment(sketch, "E1148", {"start": v(-131.69, 119.98) * mm, "end": v(-132.2, 120.04) * mm});
            skLineSegment(sketch, "E1149", {"start": v(-132.2, 120.04) * mm, "end": v(-132.7, 120.1) * mm});
            skLineSegment(sketch, "E1150", {"start": v(-132.7, 120.1) * mm, "end": v(-133.2, 120.2) * mm});
            skLineSegment(sketch, "E1151", {"start": v(-133.2, 120.2) * mm, "end": v(-133.7, 120.28) * mm});
            skLineSegment(sketch, "E1152", {"start": v(-133.7, 120.28) * mm, "end": v(-134.2, 120.4) * mm});
            skLineSegment(sketch, "E1153", {"start": v(-134.2, 120.4) * mm, "end": v(-134.7, 120.5) * mm});
            skLineSegment(sketch, "E1154", {"start": v(-134.7, 120.5) * mm, "end": v(-135.18, 120.64) * mm});
            skLineSegment(sketch, "E1155", {"start": v(-135.18, 120.64) * mm, "end": v(-135.67, 120.78) * mm});
            skLineSegment(sketch, "E1156", {"start": v(-135.67, 120.78) * mm, "end": v(-136.16, 120.94) * mm});
            skLineSegment(sketch, "E1157", {"start": v(-136.16, 120.94) * mm, "end": v(-136.63, 121.1) * mm});
            skLineSegment(sketch, "E1158", {"start": v(-136.63, 121.1) * mm, "end": v(-137.1, 121.28) * mm});
            skLineSegment(sketch, "E1159", {"start": v(-137.1, 121.28) * mm, "end": v(-137.58, 121.47) * mm});
            skLineSegment(sketch, "E1160", {"start": v(-137.58, 121.47) * mm, "end": v(-138.05, 121.67) * mm});
            skLineSegment(sketch, "E1161", {"start": v(-138.05, 121.67) * mm, "end": v(-138.5, 121.88) * mm});
            skLineSegment(sketch, "E1162", {"start": v(-138.5, 121.88) * mm, "end": v(-138.96, 122.1) * mm});
            skLineSegment(sketch, "E1163", {"start": v(-138.96, 122.1) * mm, "end": v(-139.41, 122.34) * mm});
            skLineSegment(sketch, "E1164", {"start": v(-139.41, 122.34) * mm, "end": v(-139.86, 122.6) * mm});
            skLineSegment(sketch, "E1165", {"start": v(-139.86, 122.6) * mm, "end": v(-140.3, 122.85) * mm});
            skLineSegment(sketch, "E1166", {"start": v(-140.3, 122.85) * mm, "end": v(-140.72, 123.12) * mm});
            skLineSegment(sketch, "E1167", {"start": v(-140.72, 123.12) * mm, "end": v(-141.15, 123.4) * mm});
            skLineSegment(sketch, "E1168", {"start": v(-141.15, 123.4) * mm, "end": v(-141.57, 123.7) * mm});
            skLineSegment(sketch, "E1169", {"start": v(-141.57, 123.7) * mm, "end": v(-141.98, 124) * mm});
            skLineSegment(sketch, "E1170", {"start": v(-141.98, 124) * mm, "end": v(-142.39, 124.3) * mm});
            skLineSegment(sketch, "E1171", {"start": v(-142.39, 124.3) * mm, "end": v(-142.78, 124.63) * mm});
            skLineSegment(sketch, "E1172", {"start": v(-142.78, 124.63) * mm, "end": v(-143.17, 124.96) * mm});
            skLineSegment(sketch, "E1173", {"start": v(-143.17, 124.96) * mm, "end": v(-143.55, 125.3) * mm});
            skLineSegment(sketch, "E1174", {"start": v(-143.55, 125.3) * mm, "end": v(-143.93, 125.66) * mm});
            skLineSegment(sketch, "E1175", {"start": v(-143.93, 125.66) * mm, "end": v(-144.22, 125.95) * mm});
            skLineSegment(sketch, "E1176", {"start": v(-144.22, 125.95) * mm, "end": v(-144.5, 126.25) * mm});
            skLineSegment(sketch, "E1177", {"start": v(-144.5, 126.25) * mm, "end": v(-144.78, 126.56) * mm});
            skLineSegment(sketch, "E1178", {"start": v(-144.78, 126.56) * mm, "end": v(-145.04, 126.87) * mm});
            skLineSegment(sketch, "E1179", {"start": v(-145.04, 126.87) * mm, "end": v(-145.3, 127.2) * mm});
            skLineSegment(sketch, "E1180", {"start": v(-145.3, 127.2) * mm, "end": v(-145.55, 127.52) * mm});
            skLineSegment(sketch, "E1181", {"start": v(-145.55, 127.52) * mm, "end": v(-145.8, 127.85) * mm});
            skLineSegment(sketch, "E1182", {"start": v(-145.8, 127.85) * mm, "end": v(-146.03, 128.19) * mm});
            skLineSegment(sketch, "E1183", {"start": v(-146.03, 128.19) * mm, "end": v(-146.25, 128.53) * mm});
            skLineSegment(sketch, "E1184", {"start": v(-146.25, 128.53) * mm, "end": v(-146.46, 128.88) * mm});
            skLineSegment(sketch, "E1185", {"start": v(-146.46, 128.88) * mm, "end": v(-146.67, 129.23) * mm});
            skLineSegment(sketch, "E1186", {"start": v(-146.67, 129.23) * mm, "end": v(-146.87, 129.59) * mm});
            skLineSegment(sketch, "E1187", {"start": v(-146.87, 129.59) * mm, "end": v(-147.06, 129.95) * mm});
            skLineSegment(sketch, "E1188", {"start": v(-147.06, 129.95) * mm, "end": v(-147.24, 130.31) * mm});
            skLineSegment(sketch, "E1189", {"start": v(-147.24, 130.31) * mm, "end": v(-147.4, 130.68) * mm});
            skLineSegment(sketch, "E1190", {"start": v(-147.4, 130.68) * mm, "end": v(-147.57, 131.06) * mm});
            skLineSegment(sketch, "E1191", {"start": v(-147.57, 131.06) * mm, "end": v(-147.72, 131.44) * mm});
            skLineSegment(sketch, "E1192", {"start": v(-147.72, 131.44) * mm, "end": v(-147.86, 131.82) * mm});
            skLineSegment(sketch, "E1193", {"start": v(-147.86, 131.82) * mm, "end": v(-148, 132.2) * mm});
            skLineSegment(sketch, "E1194", {"start": v(-148, 132.2) * mm, "end": v(-148.12, 132.6) * mm});
            skLineSegment(sketch, "E1195", {"start": v(-148.12, 132.6) * mm, "end": v(-148.23, 132.99) * mm});
            skLineSegment(sketch, "E1196", {"start": v(-148.23, 132.99) * mm, "end": v(-148.34, 133.38) * mm});
            skLineSegment(sketch, "E1197", {"start": v(-148.34, 133.38) * mm, "end": v(-148.43, 133.78) * mm});
            skLineSegment(sketch, "E1198", {"start": v(-148.43, 133.78) * mm, "end": v(-148.52, 134.18) * mm});
            skLineSegment(sketch, "E1199", {"start": v(-148.52, 134.18) * mm, "end": v(-148.59, 134.58) * mm});
            skLineSegment(sketch, "E1200", {"start": v(-148.59, 134.58) * mm, "end": v(-148.65, 134.99) * mm});
            skLineSegment(sketch, "E1201", {"start": v(-148.65, 134.99) * mm, "end": v(-148.7, 135.4) * mm});
            skLineSegment(sketch, "E1202", {"start": v(-148.7, 135.4) * mm, "end": v(-148.75, 135.8) * mm});
            skLineSegment(sketch, "E1203", {"start": v(-148.75, 135.8) * mm, "end": v(-148.79, 136.21) * mm});
            skLineSegment(sketch, "E1204", {"start": v(-148.79, 136.21) * mm, "end": v(-148.81, 136.62) * mm});
            skLineSegment(sketch, "E1205", {"start": v(-148.81, 136.62) * mm, "end": v(-148.82, 137.04) * mm});
            skLineSegment(sketch, "E1206", {"start": v(-148.82, 137.04) * mm, "end": v(-148.83, 137.45) * mm});
            skLineSegment(sketch, "E1207", {"start": v(-148.83, 93.2) * mm, "end": v(-148.83, 93.62) * mm});
            skLineSegment(sketch, "E1208", {"start": v(-148.83, 93.62) * mm, "end": v(-148.82, 94.04) * mm});
            skLineSegment(sketch, "E1209", {"start": v(-148.82, 94.04) * mm, "end": v(-148.8, 94.46) * mm});
            skLineSegment(sketch, "E1210", {"start": v(-148.8, 94.46) * mm, "end": v(-148.78, 94.88) * mm});
            skLineSegment(sketch, "E1211", {"start": v(-148.78, 94.88) * mm, "end": v(-148.74, 95.3) * mm});
            skLineSegment(sketch, "E1212", {"start": v(-148.74, 95.3) * mm, "end": v(-148.69, 95.7) * mm});
            skLineSegment(sketch, "E1213", {"start": v(-148.69, 95.7) * mm, "end": v(-148.63, 96.12) * mm});
            skLineSegment(sketch, "E1214", {"start": v(-148.63, 96.12) * mm, "end": v(-148.56, 96.53) * mm});
            skLineSegment(sketch, "E1215", {"start": v(-148.56, 96.53) * mm, "end": v(-148.48, 96.93) * mm});
            skLineSegment(sketch, "E1216", {"start": v(-148.48, 96.93) * mm, "end": v(-148.4, 97.34) * mm});
            skLineSegment(sketch, "E1217", {"start": v(-148.4, 97.34) * mm, "end": v(-148.3, 97.74) * mm});
            skLineSegment(sketch, "E1218", {"start": v(-148.3, 97.74) * mm, "end": v(-148.18, 98.14) * mm});
            skLineSegment(sketch, "E1219", {"start": v(-148.18, 98.14) * mm, "end": v(-148.06, 98.54) * mm});
            skLineSegment(sketch, "E1220", {"start": v(-148.06, 98.54) * mm, "end": v(-147.93, 98.93) * mm});
            skLineSegment(sketch, "E1221", {"start": v(-147.93, 98.93) * mm, "end": v(-147.8, 99.32) * mm});
            skLineSegment(sketch, "E1222", {"start": v(-147.8, 99.32) * mm, "end": v(-147.65, 99.7) * mm});
            skLineSegment(sketch, "E1223", {"start": v(-147.65, 99.7) * mm, "end": v(-147.49, 100.09) * mm});
            skLineSegment(sketch, "E1224", {"start": v(-147.49, 100.09) * mm, "end": v(-147.32, 100.47) * mm});
            skLineSegment(sketch, "E1225", {"start": v(-147.32, 100.47) * mm, "end": v(-147.14, 100.84) * mm});
            skLineSegment(sketch, "E1226", {"start": v(-147.14, 100.84) * mm, "end": v(-146.96, 101.21) * mm});
            skLineSegment(sketch, "E1227", {"start": v(-146.96, 101.21) * mm, "end": v(-146.76, 101.58) * mm});
            skLineSegment(sketch, "E1228", {"start": v(-146.76, 101.58) * mm, "end": v(-146.56, 101.94) * mm});
            skLineSegment(sketch, "E1229", {"start": v(-146.56, 101.94) * mm, "end": v(-146.35, 102.3) * mm});
            skLineSegment(sketch, "E1230", {"start": v(-146.35, 102.3) * mm, "end": v(-146.12, 102.64) * mm});
            skLineSegment(sketch, "E1231", {"start": v(-146.12, 102.64) * mm, "end": v(-145.9, 102.99) * mm});
            skLineSegment(sketch, "E1232", {"start": v(-145.9, 102.99) * mm, "end": v(-145.65, 103.33) * mm});
            skLineSegment(sketch, "E1233", {"start": v(-145.65, 103.33) * mm, "end": v(-145.4, 103.66) * mm});
            skLineSegment(sketch, "E1234", {"start": v(-145.4, 103.66) * mm, "end": v(-145.15, 103.99) * mm});
            skLineSegment(sketch, "E1235", {"start": v(-145.15, 103.99) * mm, "end": v(-144.88, 104.31) * mm});
            skLineSegment(sketch, "E1236", {"start": v(-144.88, 104.31) * mm, "end": v(-144.6, 104.63) * mm});
            skLineSegment(sketch, "E1237", {"start": v(-144.6, 104.63) * mm, "end": v(-144.32, 104.94) * mm});
            skLineSegment(sketch, "E1238", {"start": v(-144.32, 104.94) * mm, "end": v(-144.03, 105.24) * mm});
            skLineSegment(sketch, "E1239", {"start": v(-144.03, 105.24) * mm, "end": v(-143.65, 105.59) * mm});
            skLineSegment(sketch, "E1240", {"start": v(-143.65, 105.59) * mm, "end": v(-143.26, 105.93) * mm});
            skLineSegment(sketch, "E1241", {"start": v(-143.26, 105.93) * mm, "end": v(-142.87, 106.26) * mm});
            skLineSegment(sketch, "E1242", {"start": v(-142.87, 106.26) * mm, "end": v(-142.46, 106.58) * mm});
            skLineSegment(sketch, "E1243", {"start": v(-142.46, 106.58) * mm, "end": v(-142.05, 106.88) * mm});
            skLineSegment(sketch, "E1244", {"start": v(-142.05, 106.88) * mm, "end": v(-141.64, 107.18) * mm});
            skLineSegment(sketch, "E1245", {"start": v(-141.64, 107.18) * mm, "end": v(-141.21, 107.47) * mm});
            skLineSegment(sketch, "E1246", {"start": v(-141.21, 107.47) * mm, "end": v(-140.78, 107.74) * mm});
            skLineSegment(sketch, "E1247", {"start": v(-140.78, 107.74) * mm, "end": v(-140.34, 108) * mm});
            skLineSegment(sketch, "E1248", {"start": v(-140.34, 108) * mm, "end": v(-139.9, 108.26) * mm});
            skLineSegment(sketch, "E1249", {"start": v(-139.9, 108.26) * mm, "end": v(-139.45, 108.5) * mm});
            skLineSegment(sketch, "E1250", {"start": v(-139.45, 108.5) * mm, "end": v(-139, 108.73) * mm});
            skLineSegment(sketch, "E1251", {"start": v(-139, 108.73) * mm, "end": v(-138.54, 108.95) * mm});
            skLineSegment(sketch, "E1252", {"start": v(-138.54, 108.95) * mm, "end": v(-138.07, 109.16) * mm});
            skLineSegment(sketch, "E1253", {"start": v(-138.07, 109.16) * mm, "end": v(-137.6, 109.36) * mm});
            skLineSegment(sketch, "E1254", {"start": v(-137.6, 109.36) * mm, "end": v(-137.13, 109.55) * mm});
            skLineSegment(sketch, "E1255", {"start": v(-137.13, 109.55) * mm, "end": v(-136.65, 109.72) * mm});
            skLineSegment(sketch, "E1256", {"start": v(-136.65, 109.72) * mm, "end": v(-136.17, 109.88) * mm});
            skLineSegment(sketch, "E1257", {"start": v(-136.17, 109.88) * mm, "end": v(-135.68, 110.03) * mm});
            skLineSegment(sketch, "E1258", {"start": v(-135.68, 110.03) * mm, "end": v(-135.2, 110.17) * mm});
            skLineSegment(sketch, "E1259", {"start": v(-135.2, 110.17) * mm, "end": v(-134.7, 110.3) * mm});
            skLineSegment(sketch, "E1260", {"start": v(-134.7, 110.3) * mm, "end": v(-134.2, 110.41) * mm});
            skLineSegment(sketch, "E1261", {"start": v(-134.2, 110.41) * mm, "end": v(-133.7, 110.51) * mm});
            skLineSegment(sketch, "E1262", {"start": v(-133.7, 110.51) * mm, "end": v(-133.2, 110.6) * mm});
            skLineSegment(sketch, "E1263", {"start": v(-133.2, 110.6) * mm, "end": v(-132.7, 110.68) * mm});
            skLineSegment(sketch, "E1264", {"start": v(-132.7, 110.68) * mm, "end": v(-132.18, 110.74) * mm});
            skLineSegment(sketch, "E1265", {"start": v(-132.18, 110.74) * mm, "end": v(-131.67, 110.8) * mm});
            skLineSegment(sketch, "E1266", {"start": v(-131.67, 110.8) * mm, "end": v(-131.16, 110.84) * mm});
            skLineSegment(sketch, "E1267", {"start": v(-131.16, 110.84) * mm, "end": v(-130.65, 110.86) * mm});
            skLineSegment(sketch, "E1268", {"start": v(-130.65, 110.86) * mm, "end": v(-130.13, 110.88) * mm});
            skLineSegment(sketch, "E1269", {"start": v(-130.13, 110.88) * mm, "end": v(-129.62, 110.88) * mm});
            skLineSegment(sketch, "E1270", {"start": v(-129.62, 110.88) * mm, "end": v(-129.1, 110.86) * mm});
            skLineSegment(sketch, "E1271", {"start": v(-129.1, 110.86) * mm, "end": v(-128.54, 110.88) * mm});
            skLineSegment(sketch, "E1272", {"start": v(-128.54, 110.88) * mm, "end": v(-127.98, 110.88) * mm});
            skLineSegment(sketch, "E1273", {"start": v(-127.98, 110.88) * mm, "end": v(-127.42, 110.87) * mm});
            skLineSegment(sketch, "E1274", {"start": v(-127.42, 110.87) * mm, "end": v(-126.86, 110.84) * mm});
            skLineSegment(sketch, "E1275", {"start": v(-126.86, 110.84) * mm, "end": v(-126.3, 110.8) * mm});
            skLineSegment(sketch, "E1276", {"start": v(-126.3, 110.8) * mm, "end": v(-125.75, 110.75) * mm});
            skLineSegment(sketch, "E1277", {"start": v(-125.75, 110.75) * mm, "end": v(-125.2, 110.68) * mm});
            skLineSegment(sketch, "E1278", {"start": v(-125.2, 110.68) * mm, "end": v(-124.65, 110.6) * mm});
            skLineSegment(sketch, "E1279", {"start": v(-124.65, 110.6) * mm, "end": v(-124.1, 110.5) * mm});
            skLineSegment(sketch, "E1280", {"start": v(-124.1, 110.5) * mm, "end": v(-123.56, 110.4) * mm});
            skLineSegment(sketch, "E1281", {"start": v(-123.56, 110.4) * mm, "end": v(-123.02, 110.27) * mm});
            skLineSegment(sketch, "E1282", {"start": v(-123.02, 110.27) * mm, "end": v(-122.49, 110.14) * mm});
            skLineSegment(sketch, "E1283", {"start": v(-122.49, 110.14) * mm, "end": v(-121.95, 109.99) * mm});
            skLineSegment(sketch, "E1284", {"start": v(-121.95, 109.99) * mm, "end": v(-121.42, 109.82) * mm});
            skLineSegment(sketch, "E1285", {"start": v(-121.42, 109.82) * mm, "end": v(-120.9, 109.65) * mm});
            skLineSegment(sketch, "E1286", {"start": v(-120.9, 109.65) * mm, "end": v(-120.38, 109.46) * mm});
            skLineSegment(sketch, "E1287", {"start": v(-120.38, 109.46) * mm, "end": v(-119.86, 109.26) * mm});
            skLineSegment(sketch, "E1288", {"start": v(-119.86, 109.26) * mm, "end": v(-119.35, 109.05) * mm});
            skLineSegment(sketch, "E1289", {"start": v(-119.35, 109.05) * mm, "end": v(-118.85, 108.82) * mm});
            skLineSegment(sketch, "E1290", {"start": v(-118.85, 108.82) * mm, "end": v(-118.35, 108.58) * mm});
            skLineSegment(sketch, "E1291", {"start": v(-118.35, 108.58) * mm, "end": v(-117.86, 108.33) * mm});
            skLineSegment(sketch, "E1292", {"start": v(-117.86, 108.33) * mm, "end": v(-117.37, 108.07) * mm});
            skLineSegment(sketch, "E1293", {"start": v(-117.37, 108.07) * mm, "end": v(-116.9, 107.8) * mm});
            skLineSegment(sketch, "E1294", {"start": v(-116.9, 107.8) * mm, "end": v(-116.42, 107.5) * mm});
            skLineSegment(sketch, "E1295", {"start": v(-116.42, 107.5) * mm, "end": v(-115.95, 107.2) * mm});
            skLineSegment(sketch, "E1296", {"start": v(-115.95, 107.2) * mm, "end": v(-115.49, 106.9) * mm});
            skLineSegment(sketch, "E1297", {"start": v(-115.49, 106.9) * mm, "end": v(-115.04, 106.57) * mm});
            skLineSegment(sketch, "E1298", {"start": v(-115.04, 106.57) * mm, "end": v(-114.6, 106.23) * mm});
            skLineSegment(sketch, "E1299", {"start": v(-114.6, 106.23) * mm, "end": v(-114.15, 105.88) * mm});
            skLineSegment(sketch, "E1300", {"start": v(-114.15, 105.88) * mm, "end": v(-113.73, 105.53) * mm});
            skLineSegment(sketch, "E1301", {"start": v(-113.73, 105.53) * mm, "end": v(-113.3, 105.16) * mm});
            skLineSegment(sketch, "E1302", {"start": v(-113.3, 105.16) * mm, "end": v(-112.9, 104.77) * mm});
            skLineSegment(sketch, "E1303", {"start": v(-112.9, 104.77) * mm, "end": v(-112.6, 104.49) * mm});
            skLineSegment(sketch, "E1304", {"start": v(-112.6, 104.49) * mm, "end": v(-112.32, 104.2) * mm});
            skLineSegment(sketch, "E1305", {"start": v(-112.32, 104.2) * mm, "end": v(-112.05, 103.9) * mm});
            skLineSegment(sketch, "E1306", {"start": v(-112.05, 103.9) * mm, "end": v(-111.78, 103.6) * mm});
            skLineSegment(sketch, "E1307", {"start": v(-111.78, 103.6) * mm, "end": v(-111.52, 103.28) * mm});
            skLineSegment(sketch, "E1308", {"start": v(-111.52, 103.28) * mm, "end": v(-111.27, 102.96) * mm});
            skLineSegment(sketch, "E1309", {"start": v(-111.27, 102.96) * mm, "end": v(-111.03, 102.64) * mm});
            skLineSegment(sketch, "E1310", {"start": v(-111.03, 102.64) * mm, "end": v(-110.8, 102.3) * mm});
            skLineSegment(sketch, "E1311", {"start": v(-110.8, 102.3) * mm, "end": v(-110.58, 101.97) * mm});
            skLineSegment(sketch, "E1312", {"start": v(-110.58, 101.97) * mm, "end": v(-110.37, 101.63) * mm});
            skLineSegment(sketch, "E1313", {"start": v(-110.37, 101.63) * mm, "end": v(-110.16, 101.29) * mm});
            skLineSegment(sketch, "E1314", {"start": v(-110.16, 101.29) * mm, "end": v(-109.96, 100.94) * mm});
            skLineSegment(sketch, "E1315", {"start": v(-109.96, 100.94) * mm, "end": v(-109.78, 100.58) * mm});
            skLineSegment(sketch, "E1316", {"start": v(-109.78, 100.58) * mm, "end": v(-109.6, 100.22) * mm});
            skLineSegment(sketch, "E1317", {"start": v(-109.6, 100.22) * mm, "end": v(-109.43, 99.86) * mm});
            skLineSegment(sketch, "E1318", {"start": v(-109.43, 99.86) * mm, "end": v(-109.27, 99.49) * mm});
            skLineSegment(sketch, "E1319", {"start": v(-109.27, 99.49) * mm, "end": v(-109.12, 99.12) * mm});
            skLineSegment(sketch, "E1320", {"start": v(-109.12, 99.12) * mm, "end": v(-108.98, 98.74) * mm});
            skLineSegment(sketch, "E1321", {"start": v(-108.98, 98.74) * mm, "end": v(-108.85, 98.36) * mm});
            skLineSegment(sketch, "E1322", {"start": v(-108.85, 98.36) * mm, "end": v(-108.73, 97.98) * mm});
            skLineSegment(sketch, "E1323", {"start": v(-108.73, 97.98) * mm, "end": v(-108.62, 97.6) * mm});
            skLineSegment(sketch, "E1324", {"start": v(-108.62, 97.6) * mm, "end": v(-108.52, 97.2) * mm});
            skLineSegment(sketch, "E1325", {"start": v(-108.52, 97.2) * mm, "end": v(-108.43, 96.81) * mm});
            skLineSegment(sketch, "E1326", {"start": v(-108.43, 96.81) * mm, "end": v(-108.35, 96.42) * mm});
            skLineSegment(sketch, "E1327", {"start": v(-108.35, 96.42) * mm, "end": v(-108.28, 96.02) * mm});
            skLineSegment(sketch, "E1328", {"start": v(-108.28, 96.02) * mm, "end": v(-108.21, 95.62) * mm});
            skLineSegment(sketch, "E1329", {"start": v(-108.21, 95.62) * mm, "end": v(-108.16, 95.22) * mm});
            skLineSegment(sketch, "E1330", {"start": v(-108.16, 95.22) * mm, "end": v(-108.12, 94.82) * mm});
            skLineSegment(sketch, "E1331", {"start": v(-108.12, 94.82) * mm, "end": v(-108.1, 94.42) * mm});
            skLineSegment(sketch, "E1332", {"start": v(-108.1, 94.42) * mm, "end": v(-108.07, 94) * mm});
            skLineSegment(sketch, "E1333", {"start": v(-108.07, 94) * mm, "end": v(-108.06, 93.6) * mm});
            skLineSegment(sketch, "E1334", {"start": v(-108.06, 93.6) * mm, "end": v(-108.07, 93.2) * mm});
            skLineSegment(sketch, "E1335", {"start": v(-108.07, 93.2) * mm, "end": v(-108.07, 92.78) * mm});
            skLineSegment(sketch, "E1336", {"start": v(-108.07, 92.78) * mm, "end": v(-108.08, 92.37) * mm});
            skLineSegment(sketch, "E1337", {"start": v(-108.08, 92.37) * mm, "end": v(-108.1, 91.96) * mm});
            skLineSegment(sketch, "E1338", {"start": v(-108.1, 91.96) * mm, "end": v(-108.15, 91.55) * mm});
            skLineSegment(sketch, "E1339", {"start": v(-108.15, 91.55) * mm, "end": v(-108.2, 91.14) * mm});
            skLineSegment(sketch, "E1340", {"start": v(-108.2, 91.14) * mm, "end": v(-108.25, 90.73) * mm});
            skLineSegment(sketch, "E1341", {"start": v(-108.25, 90.73) * mm, "end": v(-108.32, 90.33) * mm});
            skLineSegment(sketch, "E1342", {"start": v(-108.32, 90.33) * mm, "end": v(-108.4, 89.92) * mm});
            skLineSegment(sketch, "E1343", {"start": v(-108.4, 89.92) * mm, "end": v(-108.48, 89.52) * mm});
            skLineSegment(sketch, "E1344", {"start": v(-108.48, 89.52) * mm, "end": v(-108.58, 89.13) * mm});
            skLineSegment(sketch, "E1345", {"start": v(-108.58, 89.13) * mm, "end": v(-108.69, 88.73) * mm});
            skLineSegment(sketch, "E1346", {"start": v(-108.69, 88.73) * mm, "end": v(-108.8, 88.34) * mm});
            skLineSegment(sketch, "E1347", {"start": v(-108.8, 88.34) * mm, "end": v(-108.93, 87.96) * mm});
            skLineSegment(sketch, "E1348", {"start": v(-108.93, 87.96) * mm, "end": v(-109.07, 87.57) * mm});
            skLineSegment(sketch, "E1349", {"start": v(-109.07, 87.57) * mm, "end": v(-109.22, 87.2) * mm});
            skLineSegment(sketch, "E1350", {"start": v(-109.22, 87.2) * mm, "end": v(-109.37, 86.81) * mm});
            skLineSegment(sketch, "E1351", {"start": v(-109.37, 86.81) * mm, "end": v(-109.54, 86.44) * mm});
            skLineSegment(sketch, "E1352", {"start": v(-109.54, 86.44) * mm, "end": v(-109.71, 86.07) * mm});
            skLineSegment(sketch, "E1353", {"start": v(-109.71, 86.07) * mm, "end": v(-109.9, 85.71) * mm});
            skLineSegment(sketch, "E1354", {"start": v(-109.9, 85.71) * mm, "end": v(-110.1, 85.35) * mm});
            skLineSegment(sketch, "E1355", {"start": v(-110.1, 85.35) * mm, "end": v(-110.3, 85) * mm});
            skLineSegment(sketch, "E1356", {"start": v(-110.3, 85) * mm, "end": v(-110.5, 84.65) * mm});
            skLineSegment(sketch, "E1357", {"start": v(-110.5, 84.65) * mm, "end": v(-110.73, 84.3) * mm});
            skLineSegment(sketch, "E1358", {"start": v(-110.73, 84.3) * mm, "end": v(-110.96, 83.97) * mm});
            skLineSegment(sketch, "E1359", {"start": v(-110.96, 83.97) * mm, "end": v(-111.2, 83.64) * mm});
            skLineSegment(sketch, "E1360", {"start": v(-111.2, 83.64) * mm, "end": v(-111.45, 83.3) * mm});
            skLineSegment(sketch, "E1361", {"start": v(-111.45, 83.3) * mm, "end": v(-111.7, 82.99) * mm});
            skLineSegment(sketch, "E1362", {"start": v(-111.7, 82.99) * mm, "end": v(-111.97, 82.68) * mm});
            skLineSegment(sketch, "E1363", {"start": v(-111.97, 82.68) * mm, "end": v(-112.25, 82.37) * mm});
            skLineSegment(sketch, "E1364", {"start": v(-112.25, 82.37) * mm, "end": v(-112.53, 82.07) * mm});
            skLineSegment(sketch, "E1365", {"start": v(-112.53, 82.07) * mm, "end": v(-112.82, 81.77) * mm});
            skLineSegment(sketch, "E1366", {"start": v(-112.82, 81.77) * mm, "end": v(-113.12, 81.49) * mm});
            skLineSegment(sketch, "E1367", {"start": v(-113.12, 81.49) * mm, "end": v(-113.53, 81.12) * mm});
            skLineSegment(sketch, "E1368", {"start": v(-113.53, 81.12) * mm, "end": v(-113.94, 80.76) * mm});
            skLineSegment(sketch, "E1369", {"start": v(-113.94, 80.76) * mm, "end": v(-114.37, 80.4) * mm});
            skLineSegment(sketch, "E1370", {"start": v(-114.37, 80.4) * mm, "end": v(-114.8, 80.07) * mm});
            skLineSegment(sketch, "E1371", {"start": v(-114.8, 80.07) * mm, "end": v(-115.25, 79.75) * mm});
            skLineSegment(sketch, "E1372", {"start": v(-115.25, 79.75) * mm, "end": v(-115.7, 79.44) * mm});
            skLineSegment(sketch, "E1373", {"start": v(-115.7, 79.44) * mm, "end": v(-116.15, 79.13) * mm});
            skLineSegment(sketch, "E1374", {"start": v(-116.15, 79.13) * mm, "end": v(-116.61, 78.84) * mm});
            skLineSegment(sketch, "E1375", {"start": v(-116.61, 78.84) * mm, "end": v(-117.08, 78.57) * mm});
            skLineSegment(sketch, "E1376", {"start": v(-117.08, 78.57) * mm, "end": v(-117.56, 78.3) * mm});
            skLineSegment(sketch, "E1377", {"start": v(-117.56, 78.3) * mm, "end": v(-118.04, 78.05) * mm});
            skLineSegment(sketch, "E1378", {"start": v(-118.04, 78.05) * mm, "end": v(-118.53, 77.8) * mm});
            skLineSegment(sketch, "E1379", {"start": v(-118.53, 77.8) * mm, "end": v(-119.02, 77.57) * mm});
            skLineSegment(sketch, "E1380", {"start": v(-119.02, 77.57) * mm, "end": v(-119.52, 77.36) * mm});
            skLineSegment(sketch, "E1381", {"start": v(-119.52, 77.36) * mm, "end": v(-120.03, 77.15) * mm});
            skLineSegment(sketch, "E1382", {"start": v(-120.03, 77.15) * mm, "end": v(-120.53, 76.96) * mm});
            skLineSegment(sketch, "E1383", {"start": v(-120.53, 76.96) * mm, "end": v(-121.05, 76.78) * mm});
            skLineSegment(sketch, "E1384", {"start": v(-121.05, 76.78) * mm, "end": v(-121.57, 76.61) * mm});
            skLineSegment(sketch, "E1385", {"start": v(-121.57, 76.61) * mm, "end": v(-122.09, 76.46) * mm});
            skLineSegment(sketch, "E1386", {"start": v(-122.09, 76.46) * mm, "end": v(-122.61, 76.32) * mm});
            skLineSegment(sketch, "E1387", {"start": v(-122.61, 76.32) * mm, "end": v(-123.14, 76.19) * mm});
            skLineSegment(sketch, "E1388", {"start": v(-123.14, 76.19) * mm, "end": v(-123.67, 76.07) * mm});
            skLineSegment(sketch, "E1389", {"start": v(-123.67, 76.07) * mm, "end": v(-124.2, 75.97) * mm});
            skLineSegment(sketch, "E1390", {"start": v(-124.2, 75.97) * mm, "end": v(-124.75, 75.88) * mm});
            skLineSegment(sketch, "E1391", {"start": v(-124.75, 75.88) * mm, "end": v(-125.29, 75.8) * mm});
            skLineSegment(sketch, "E1392", {"start": v(-125.29, 75.8) * mm, "end": v(-125.83, 75.74) * mm});
            skLineSegment(sketch, "E1393", {"start": v(-125.83, 75.74) * mm, "end": v(-126.38, 75.7) * mm});
            skLineSegment(sketch, "E1394", {"start": v(-126.38, 75.7) * mm, "end": v(-126.92, 75.66) * mm});
            skLineSegment(sketch, "E1395", {"start": v(-126.92, 75.66) * mm, "end": v(-127.47, 75.63) * mm});
            skLineSegment(sketch, "E1396", {"start": v(-127.47, 75.63) * mm, "end": v(-128.02, 75.63) * mm});
            skLineSegment(sketch, "E1397", {"start": v(-128.02, 75.63) * mm, "end": v(-128.57, 75.63) * mm});
            skLineSegment(sketch, "E1398", {"start": v(-128.57, 75.63) * mm, "end": v(-129.13, 75.65) * mm});
            skLineSegment(sketch, "E1399", {"start": v(-129.13, 75.65) * mm, "end": v(-129.64, 75.64) * mm});
            skLineSegment(sketch, "E1400", {"start": v(-129.64, 75.64) * mm, "end": v(-130.15, 75.65) * mm});
            skLineSegment(sketch, "E1401", {"start": v(-130.15, 75.65) * mm, "end": v(-130.67, 75.67) * mm});
            skLineSegment(sketch, "E1402", {"start": v(-130.67, 75.67) * mm, "end": v(-131.18, 75.7) * mm});
            skLineSegment(sketch, "E1403", {"start": v(-131.18, 75.7) * mm, "end": v(-131.69, 75.74) * mm});
            skLineSegment(sketch, "E1404", {"start": v(-131.69, 75.74) * mm, "end": v(-132.2, 75.8) * mm});
            skLineSegment(sketch, "E1405", {"start": v(-132.2, 75.8) * mm, "end": v(-132.7, 75.86) * mm});
            skLineSegment(sketch, "E1406", {"start": v(-132.7, 75.86) * mm, "end": v(-133.2, 75.95) * mm});
            skLineSegment(sketch, "E1407", {"start": v(-133.2, 75.95) * mm, "end": v(-133.7, 76.04) * mm});
            skLineSegment(sketch, "E1408", {"start": v(-133.7, 76.04) * mm, "end": v(-134.2, 76.14) * mm});
            skLineSegment(sketch, "E1409", {"start": v(-134.2, 76.14) * mm, "end": v(-134.7, 76.26) * mm});
            skLineSegment(sketch, "E1410", {"start": v(-134.7, 76.26) * mm, "end": v(-135.18, 76.4) * mm});
            skLineSegment(sketch, "E1411", {"start": v(-135.18, 76.4) * mm, "end": v(-135.67, 76.54) * mm});
            skLineSegment(sketch, "E1412", {"start": v(-135.67, 76.54) * mm, "end": v(-136.16, 76.7) * mm});
            skLineSegment(sketch, "E1413", {"start": v(-136.16, 76.7) * mm, "end": v(-136.63, 76.86) * mm});
            skLineSegment(sketch, "E1414", {"start": v(-136.63, 76.86) * mm, "end": v(-137.1, 77.03) * mm});
            skLineSegment(sketch, "E1415", {"start": v(-137.1, 77.03) * mm, "end": v(-137.58, 77.22) * mm});
            skLineSegment(sketch, "E1416", {"start": v(-137.58, 77.22) * mm, "end": v(-138.05, 77.43) * mm});
            skLineSegment(sketch, "E1417", {"start": v(-138.05, 77.43) * mm, "end": v(-138.5, 77.64) * mm});
            skLineSegment(sketch, "E1418", {"start": v(-138.5, 77.64) * mm, "end": v(-138.96, 77.86) * mm});
            skLineSegment(sketch, "E1419", {"start": v(-138.96, 77.86) * mm, "end": v(-139.41, 78.1) * mm});
            skLineSegment(sketch, "E1420", {"start": v(-139.41, 78.1) * mm, "end": v(-139.86, 78.35) * mm});
            skLineSegment(sketch, "E1421", {"start": v(-139.86, 78.35) * mm, "end": v(-140.3, 78.6) * mm});
            skLineSegment(sketch, "E1422", {"start": v(-140.3, 78.6) * mm, "end": v(-140.72, 78.87) * mm});
            skLineSegment(sketch, "E1423", {"start": v(-140.72, 78.87) * mm, "end": v(-141.15, 79.15) * mm});
            skLineSegment(sketch, "E1424", {"start": v(-141.15, 79.15) * mm, "end": v(-141.57, 79.44) * mm});
            skLineSegment(sketch, "E1425", {"start": v(-141.57, 79.44) * mm, "end": v(-141.98, 79.75) * mm});
            skLineSegment(sketch, "E1426", {"start": v(-141.98, 79.75) * mm, "end": v(-142.39, 80.06) * mm});
            skLineSegment(sketch, "E1427", {"start": v(-142.39, 80.06) * mm, "end": v(-142.78, 80.38) * mm});
            skLineSegment(sketch, "E1428", {"start": v(-142.78, 80.38) * mm, "end": v(-143.17, 80.72) * mm});
            skLineSegment(sketch, "E1429", {"start": v(-143.17, 80.72) * mm, "end": v(-143.55, 81.06) * mm});
            skLineSegment(sketch, "E1430", {"start": v(-143.55, 81.06) * mm, "end": v(-143.93, 81.41) * mm});
            skLineSegment(sketch, "E1431", {"start": v(-143.93, 81.41) * mm, "end": v(-144.22, 81.7) * mm});
            skLineSegment(sketch, "E1432", {"start": v(-144.22, 81.7) * mm, "end": v(-144.5, 82) * mm});
            skLineSegment(sketch, "E1433", {"start": v(-144.5, 82) * mm, "end": v(-144.78, 82.32) * mm});
            skLineSegment(sketch, "E1434", {"start": v(-144.78, 82.32) * mm, "end": v(-145.04, 82.63) * mm});
            skLineSegment(sketch, "E1435", {"start": v(-145.04, 82.63) * mm, "end": v(-145.3, 82.95) * mm});
            skLineSegment(sketch, "E1436", {"start": v(-145.3, 82.95) * mm, "end": v(-145.55, 83.27) * mm});
            skLineSegment(sketch, "E1437", {"start": v(-145.55, 83.27) * mm, "end": v(-145.8, 83.6) * mm});
            skLineSegment(sketch, "E1438", {"start": v(-145.8, 83.6) * mm, "end": v(-146.03, 83.94) * mm});
            skLineSegment(sketch, "E1439", {"start": v(-146.03, 83.94) * mm, "end": v(-146.25, 84.28) * mm});
            skLineSegment(sketch, "E1440", {"start": v(-146.25, 84.28) * mm, "end": v(-146.46, 84.63) * mm});
            skLineSegment(sketch, "E1441", {"start": v(-146.46, 84.63) * mm, "end": v(-146.67, 84.98) * mm});
            skLineSegment(sketch, "E1442", {"start": v(-146.67, 84.98) * mm, "end": v(-146.87, 85.34) * mm});
            skLineSegment(sketch, "E1443", {"start": v(-146.87, 85.34) * mm, "end": v(-147.06, 85.7) * mm});
            skLineSegment(sketch, "E1444", {"start": v(-147.06, 85.7) * mm, "end": v(-147.24, 86.07) * mm});
            skLineSegment(sketch, "E1445", {"start": v(-147.24, 86.07) * mm, "end": v(-147.4, 86.44) * mm});
            skLineSegment(sketch, "E1446", {"start": v(-147.4, 86.44) * mm, "end": v(-147.57, 86.81) * mm});
            skLineSegment(sketch, "E1447", {"start": v(-147.57, 86.81) * mm, "end": v(-147.72, 87.2) * mm});
            skLineSegment(sketch, "E1448", {"start": v(-147.72, 87.2) * mm, "end": v(-147.86, 87.57) * mm});
            skLineSegment(sketch, "E1449", {"start": v(-147.86, 87.57) * mm, "end": v(-148, 87.96) * mm});
            skLineSegment(sketch, "E1450", {"start": v(-148, 87.96) * mm, "end": v(-148.12, 88.35) * mm});
            skLineSegment(sketch, "E1451", {"start": v(-148.12, 88.35) * mm, "end": v(-148.23, 88.74) * mm});
            skLineSegment(sketch, "E1452", {"start": v(-148.23, 88.74) * mm, "end": v(-148.34, 89.14) * mm});
            skLineSegment(sketch, "E1453", {"start": v(-148.34, 89.14) * mm, "end": v(-148.43, 89.53) * mm});
            skLineSegment(sketch, "E1454", {"start": v(-148.43, 89.53) * mm, "end": v(-148.52, 89.93) * mm});
            skLineSegment(sketch, "E1455", {"start": v(-148.52, 89.93) * mm, "end": v(-148.59, 90.34) * mm});
            skLineSegment(sketch, "E1456", {"start": v(-148.59, 90.34) * mm, "end": v(-148.65, 90.74) * mm});
            skLineSegment(sketch, "E1457", {"start": v(-148.65, 90.74) * mm, "end": v(-148.7, 91.15) * mm});
            skLineSegment(sketch, "E1458", {"start": v(-148.7, 91.15) * mm, "end": v(-148.75, 91.56) * mm});
            skLineSegment(sketch, "E1459", {"start": v(-148.75, 91.56) * mm, "end": v(-148.79, 91.97) * mm});
            skLineSegment(sketch, "E1460", {"start": v(-148.79, 91.97) * mm, "end": v(-148.81, 92.38) * mm});
            skLineSegment(sketch, "E1461", {"start": v(-148.81, 92.38) * mm, "end": v(-148.82, 92.79) * mm});
            skLineSegment(sketch, "E1462", {"start": v(-148.82, 92.79) * mm, "end": v(-148.83, 93.2) * mm});
            skLineSegment(sketch, "E1463", {"start": v(-148.3, 66.63) * mm, "end": v(-108.3, 66.63) * mm});
            skLineSegment(sketch, "E1464", {"start": v(-108.3, 66.63) * mm, "end": v(-108.3, 41.76) * mm});
            skLineSegment(sketch, "E1465", {"start": v(-127.4, 66.63) * mm, "end": v(-127.4, 43.56) * mm});
            skLineSegment(sketch, "E1466", {"start": v(-428.27, 190.25) * mm, "end": v(-388.3, 190.25) * mm});
            skLineSegment(sketch, "E1467", {"start": v(-388.3, 190.25) * mm, "end": v(-388.3, 172.7) * mm});
            skLineSegment(sketch, "E1468", {"start": v(-388.3, 172.7) * mm, "end": v(-388.3, 172.2) * mm});
            skLineSegment(sketch, "E1469", {"start": v(-388.3, 172.2) * mm, "end": v(-388.34, 171.71) * mm});
            skLineSegment(sketch, "E1470", {"start": v(-388.34, 171.71) * mm, "end": v(-388.4, 171.22) * mm});
            skLineSegment(sketch, "E1471", {"start": v(-388.4, 171.22) * mm, "end": v(-388.47, 170.74) * mm});
            skLineSegment(sketch, "E1472", {"start": v(-388.47, 170.74) * mm, "end": v(-388.57, 170.26) * mm});
            skLineSegment(sketch, "E1473", {"start": v(-388.57, 170.26) * mm, "end": v(-388.7, 169.8) * mm});
            skLineSegment(sketch, "E1474", {"start": v(-388.7, 169.8) * mm, "end": v(-388.85, 169.33) * mm});
            skLineSegment(sketch, "E1475", {"start": v(-388.85, 169.33) * mm, "end": v(-389.03, 168.87) * mm});
            skLineSegment(sketch, "E1476", {"start": v(-389.03, 168.87) * mm, "end": v(-389.22, 168.43) * mm});
            skLineSegment(sketch, "E1477", {"start": v(-389.22, 168.43) * mm, "end": v(-389.44, 168) * mm});
            skLineSegment(sketch, "E1478", {"start": v(-389.44, 168) * mm, "end": v(-389.68, 167.57) * mm});
            skLineSegment(sketch, "E1479", {"start": v(-389.68, 167.57) * mm, "end": v(-389.95, 167.16) * mm});
            skLineSegment(sketch, "E1480", {"start": v(-389.95, 167.16) * mm, "end": v(-390.23, 166.76) * mm});
            skLineSegment(sketch, "E1481", {"start": v(-390.23, 166.76) * mm, "end": v(-390.54, 166.38) * mm});
            skLineSegment(sketch, "E1482", {"start": v(-390.54, 166.38) * mm, "end": v(-390.86, 166) * mm});
            skLineSegment(sketch, "E1483", {"start": v(-390.86, 166) * mm, "end": v(-391.2, 165.65) * mm});
            skLineSegment(sketch, "E1484", {"start": v(-391.2, 165.65) * mm, "end": v(-391.56, 165.31) * mm});
            skLineSegment(sketch, "E1485", {"start": v(-391.56, 165.31) * mm, "end": v(-391.93, 165) * mm});
            skLineSegment(sketch, "E1486", {"start": v(-391.93, 165) * mm, "end": v(-392.3, 164.7) * mm});
            skLineSegment(sketch, "E1487", {"start": v(-392.3, 164.7) * mm, "end": v(-392.7, 164.41) * mm});
            skLineSegment(sketch, "E1488", {"start": v(-392.7, 164.41) * mm, "end": v(-393.11, 164.15) * mm});
            skLineSegment(sketch, "E1489", {"start": v(-393.11, 164.15) * mm, "end": v(-393.53, 163.9) * mm});
            skLineSegment(sketch, "E1490", {"start": v(-393.53, 163.9) * mm, "end": v(-393.96, 163.7) * mm});
            skLineSegment(sketch, "E1491", {"start": v(-393.96, 163.7) * mm, "end": v(-394.4, 163.5) * mm});
            skLineSegment(sketch, "E1492", {"start": v(-394.4, 163.5) * mm, "end": v(-394.85, 163.32) * mm});
            skLineSegment(sketch, "E1493", {"start": v(-394.85, 163.32) * mm, "end": v(-395.3, 163.17) * mm});
            skLineSegment(sketch, "E1494", {"start": v(-395.3, 163.17) * mm, "end": v(-395.78, 163.04) * mm});
            skLineSegment(sketch, "E1495", {"start": v(-395.78, 163.04) * mm, "end": v(-396.25, 162.93) * mm});
            skLineSegment(sketch, "E1496", {"start": v(-396.25, 162.93) * mm, "end": v(-396.73, 162.84) * mm});
            skLineSegment(sketch, "E1497", {"start": v(-396.73, 162.84) * mm, "end": v(-397.2, 162.78) * mm});
            skLineSegment(sketch, "E1498", {"start": v(-397.2, 162.78) * mm, "end": v(-397.7, 162.75) * mm});
            skLineSegment(sketch, "E1499", {"start": v(-397.7, 162.75) * mm, "end": v(-398.18, 162.74) * mm});
            skLineSegment(sketch, "E1500", {"start": v(-398.18, 162.74) * mm, "end": v(-398.69, 162.73) * mm});
            skLineSegment(sketch, "E1501", {"start": v(-398.69, 162.73) * mm, "end": v(-399.18, 162.76) * mm});
            skLineSegment(sketch, "E1502", {"start": v(-399.18, 162.76) * mm, "end": v(-399.68, 162.8) * mm});
            skLineSegment(sketch, "E1503", {"start": v(-399.68, 162.8) * mm, "end": v(-400.17, 162.88) * mm});
            skLineSegment(sketch, "E1504", {"start": v(-400.17, 162.88) * mm, "end": v(-400.66, 162.98) * mm});
            skLineSegment(sketch, "E1505", {"start": v(-400.66, 162.98) * mm, "end": v(-401.14, 163.1) * mm});
            skLineSegment(sketch, "E1506", {"start": v(-401.14, 163.1) * mm, "end": v(-401.6, 163.24) * mm});
            skLineSegment(sketch, "E1507", {"start": v(-401.6, 163.24) * mm, "end": v(-402.07, 163.41) * mm});
            skLineSegment(sketch, "E1508", {"start": v(-402.07, 163.41) * mm, "end": v(-402.53, 163.6) * mm});
            skLineSegment(sketch, "E1509", {"start": v(-402.53, 163.6) * mm, "end": v(-402.97, 163.82) * mm});
            skLineSegment(sketch, "E1510", {"start": v(-402.97, 163.82) * mm, "end": v(-403.4, 164.06) * mm});
            skLineSegment(sketch, "E1511", {"start": v(-403.4, 164.06) * mm, "end": v(-403.83, 164.32) * mm});
            skLineSegment(sketch, "E1512", {"start": v(-403.83, 164.32) * mm, "end": v(-404.24, 164.6) * mm});
            skLineSegment(sketch, "E1513", {"start": v(-404.24, 164.6) * mm, "end": v(-404.63, 164.9) * mm});
            skLineSegment(sketch, "E1514", {"start": v(-404.63, 164.9) * mm, "end": v(-405.01, 165.23) * mm});
            skLineSegment(sketch, "E1515", {"start": v(-405.01, 165.23) * mm, "end": v(-405.38, 165.57) * mm});
            skLineSegment(sketch, "E1516", {"start": v(-405.38, 165.57) * mm, "end": v(-405.72, 165.93) * mm});
            skLineSegment(sketch, "E1517", {"start": v(-405.72, 165.93) * mm, "end": v(-406.05, 166.31) * mm});
            skLineSegment(sketch, "E1518", {"start": v(-406.05, 166.31) * mm, "end": v(-406.35, 166.7) * mm});
            skLineSegment(sketch, "E1519", {"start": v(-406.35, 166.7) * mm, "end": v(-406.63, 167.1) * mm});
            skLineSegment(sketch, "E1520", {"start": v(-406.63, 167.1) * mm, "end": v(-406.9, 167.52) * mm});
            skLineSegment(sketch, "E1521", {"start": v(-406.9, 167.52) * mm, "end": v(-407.14, 167.95) * mm});
            skLineSegment(sketch, "E1522", {"start": v(-407.14, 167.95) * mm, "end": v(-407.35, 168.4) * mm});
            skLineSegment(sketch, "E1523", {"start": v(-407.35, 168.4) * mm, "end": v(-407.55, 168.84) * mm});
            skLineSegment(sketch, "E1524", {"start": v(-407.55, 168.84) * mm, "end": v(-407.72, 169.3) * mm});
            skLineSegment(sketch, "E1525", {"start": v(-407.72, 169.3) * mm, "end": v(-407.88, 169.77) * mm});
            skLineSegment(sketch, "E1526", {"start": v(-407.88, 169.77) * mm, "end": v(-408, 170.24) * mm});
            skLineSegment(sketch, "E1527", {"start": v(-408, 170.24) * mm, "end": v(-408.1, 170.73) * mm});
            skLineSegment(sketch, "E1528", {"start": v(-408.1, 170.73) * mm, "end": v(-408.19, 171.21) * mm});
            skLineSegment(sketch, "E1529", {"start": v(-408.19, 171.21) * mm, "end": v(-408.24, 171.7) * mm});
            skLineSegment(sketch, "E1530", {"start": v(-408.24, 171.7) * mm, "end": v(-408.27, 172.2) * mm});
            skLineSegment(sketch, "E1531", {"start": v(-408.27, 172.2) * mm, "end": v(-408.28, 172.7) * mm});
            skLineSegment(sketch, "E1532", {"start": v(-408.28, 172.7) * mm, "end": v(-408.28, 190.25) * mm});
            skLineSegment(sketch, "E1533", {"start": v(-408.28, 172.7) * mm, "end": v(-408.28, 172.29) * mm});
            skLineSegment(sketch, "E1534", {"start": v(-408.28, 172.29) * mm, "end": v(-408.3, 171.88) * mm});
            skLineSegment(sketch, "E1535", {"start": v(-408.3, 171.88) * mm, "end": v(-408.35, 171.48) * mm});
            skLineSegment(sketch, "E1536", {"start": v(-408.35, 171.48) * mm, "end": v(-408.4, 171.07) * mm});
            skLineSegment(sketch, "E1537", {"start": v(-408.4, 171.07) * mm, "end": v(-408.5, 170.68) * mm});
            skLineSegment(sketch, "E1538", {"start": v(-408.5, 170.68) * mm, "end": v(-408.6, 170.29) * mm});
            skLineSegment(sketch, "E1539", {"start": v(-408.6, 170.29) * mm, "end": v(-408.72, 169.9) * mm});
            skLineSegment(sketch, "E1540", {"start": v(-408.72, 169.9) * mm, "end": v(-408.86, 169.53) * mm});
            skLineSegment(sketch, "E1541", {"start": v(-408.86, 169.53) * mm, "end": v(-409.03, 169.16) * mm});
            skLineSegment(sketch, "E1542", {"start": v(-409.03, 169.16) * mm, "end": v(-409.2, 168.8) * mm});
            skLineSegment(sketch, "E1543", {"start": v(-409.2, 168.8) * mm, "end": v(-409.4, 168.44) * mm});
            skLineSegment(sketch, "E1544", {"start": v(-409.4, 168.44) * mm, "end": v(-409.62, 168.1) * mm});
            skLineSegment(sketch, "E1545", {"start": v(-409.62, 168.1) * mm, "end": v(-409.86, 167.77) * mm});
            skLineSegment(sketch, "E1546", {"start": v(-409.86, 167.77) * mm, "end": v(-410.1, 167.45) * mm});
            skLineSegment(sketch, "E1547", {"start": v(-410.1, 167.45) * mm, "end": v(-410.38, 167.14) * mm});
            skLineSegment(sketch, "E1548", {"start": v(-410.38, 167.14) * mm, "end": v(-410.66, 166.85) * mm});
            skLineSegment(sketch, "E1549", {"start": v(-410.66, 166.85) * mm, "end": v(-411.16, 166.5) * mm});
            skLineSegment(sketch, "E1550", {"start": v(-411.16, 166.5) * mm, "end": v(-411.67, 166.19) * mm});
            skLineSegment(sketch, "E1551", {"start": v(-411.67, 166.19) * mm, "end": v(-412.2, 165.9) * mm});
            skLineSegment(sketch, "E1552", {"start": v(-412.2, 165.9) * mm, "end": v(-412.74, 165.63) * mm});
            skLineSegment(sketch, "E1553", {"start": v(-412.74, 165.63) * mm, "end": v(-413.28, 165.38) * mm});
            skLineSegment(sketch, "E1554", {"start": v(-413.28, 165.38) * mm, "end": v(-413.84, 165.16) * mm});
            skLineSegment(sketch, "E1555", {"start": v(-413.84, 165.16) * mm, "end": v(-414.4, 164.97) * mm});
            skLineSegment(sketch, "E1556", {"start": v(-414.4, 164.97) * mm, "end": v(-414.98, 164.8) * mm});
            skLineSegment(sketch, "E1557", {"start": v(-414.98, 164.8) * mm, "end": v(-415.56, 164.65) * mm});
            skLineSegment(sketch, "E1558", {"start": v(-415.56, 164.65) * mm, "end": v(-416.15, 164.54) * mm});
            skLineSegment(sketch, "E1559", {"start": v(-416.15, 164.54) * mm, "end": v(-416.74, 164.44) * mm});
            skLineSegment(sketch, "E1560", {"start": v(-416.74, 164.44) * mm, "end": v(-417.34, 164.38) * mm});
            skLineSegment(sketch, "E1561", {"start": v(-417.34, 164.38) * mm, "end": v(-417.94, 164.34) * mm});
            skLineSegment(sketch, "E1562", {"start": v(-417.94, 164.34) * mm, "end": v(-418.54, 164.33) * mm});
            skLineSegment(sketch, "E1563", {"start": v(-418.54, 164.33) * mm, "end": v(-419.14, 164.34) * mm});
            skLineSegment(sketch, "E1564", {"start": v(-419.14, 164.34) * mm, "end": v(-419.75, 164.38) * mm});
            skLineSegment(sketch, "E1565", {"start": v(-419.75, 164.38) * mm, "end": v(-420.28, 164.4) * mm});
            skLineSegment(sketch, "E1566", {"start": v(-420.28, 164.4) * mm, "end": v(-420.82, 164.4) * mm});
            skLineSegment(sketch, "E1567", {"start": v(-420.82, 164.4) * mm, "end": v(-421.36, 164.38) * mm});
            skLineSegment(sketch, "E1568", {"start": v(-421.36, 164.38) * mm, "end": v(-421.9, 164.36) * mm});
            skLineSegment(sketch, "E1569", {"start": v(-421.9, 164.36) * mm, "end": v(-422.44, 164.33) * mm});
            skLineSegment(sketch, "E1570", {"start": v(-422.44, 164.33) * mm, "end": v(-422.97, 164.29) * mm});
            skLineSegment(sketch, "E1571", {"start": v(-422.97, 164.29) * mm, "end": v(-423.5, 164.24) * mm});
            skLineSegment(sketch, "E1572", {"start": v(-423.5, 164.24) * mm, "end": v(-424.04, 164.18) * mm});
            skLineSegment(sketch, "E1573", {"start": v(-424.04, 164.18) * mm, "end": v(-424.58, 164.1) * mm});
            skLineSegment(sketch, "E1574", {"start": v(-424.58, 164.1) * mm, "end": v(-425.11, 164.03) * mm});
            skLineSegment(sketch, "E1575", {"start": v(-425.11, 164.03) * mm, "end": v(-425.64, 163.94) * mm});
            skLineSegment(sketch, "E1576", {"start": v(-425.64, 163.94) * mm, "end": v(-426.17, 163.84) * mm});
            skLineSegment(sketch, "E1577", {"start": v(-426.17, 163.84) * mm, "end": v(-426.7, 163.73) * mm});
            skLineSegment(sketch, "E1578", {"start": v(-426.7, 163.73) * mm, "end": v(-427.22, 163.62) * mm});
            skLineSegment(sketch, "E1579", {"start": v(-427.22, 163.62) * mm, "end": v(-427.75, 163.49) * mm});
            skLineSegment(sketch, "E1580", {"start": v(-427.75, 163.49) * mm, "end": v(-428.27, 163.35) * mm});
            skLineSegment(sketch, "E1581", {"start": v(-428.83, 137.45) * mm, "end": v(-428.83, 137.87) * mm});
            skLineSegment(sketch, "E1582", {"start": v(-428.83, 137.87) * mm, "end": v(-428.82, 138.29) * mm});
            skLineSegment(sketch, "E1583", {"start": v(-428.82, 138.29) * mm, "end": v(-428.8, 138.7) * mm});
            skLineSegment(sketch, "E1584", {"start": v(-428.8, 138.7) * mm, "end": v(-428.78, 139.12) * mm});
            skLineSegment(sketch, "E1585", {"start": v(-428.78, 139.12) * mm, "end": v(-428.74, 139.54) * mm});
            skLineSegment(sketch, "E1586", {"start": v(-428.74, 139.54) * mm, "end": v(-428.69, 139.95) * mm});
            skLineSegment(sketch, "E1587", {"start": v(-428.69, 139.95) * mm, "end": v(-428.63, 140.36) * mm});
            skLineSegment(sketch, "E1588", {"start": v(-428.63, 140.36) * mm, "end": v(-428.56, 140.77) * mm});
            skLineSegment(sketch, "E1589", {"start": v(-428.56, 140.77) * mm, "end": v(-428.48, 141.18) * mm});
            skLineSegment(sketch, "E1590", {"start": v(-428.48, 141.18) * mm, "end": v(-428.4, 141.58) * mm});
            skLineSegment(sketch, "E1591", {"start": v(-428.4, 141.58) * mm, "end": v(-428.3, 141.99) * mm});
            skLineSegment(sketch, "E1592", {"start": v(-428.3, 141.99) * mm, "end": v(-428.18, 142.39) * mm});
            skLineSegment(sketch, "E1593", {"start": v(-428.18, 142.39) * mm, "end": v(-428.06, 142.78) * mm});
            skLineSegment(sketch, "E1594", {"start": v(-428.06, 142.78) * mm, "end": v(-427.93, 143.18) * mm});
            skLineSegment(sketch, "E1595", {"start": v(-427.93, 143.18) * mm, "end": v(-427.8, 143.57) * mm});
            skLineSegment(sketch, "E1596", {"start": v(-427.8, 143.57) * mm, "end": v(-427.65, 143.95) * mm});
            skLineSegment(sketch, "E1597", {"start": v(-427.65, 143.95) * mm, "end": v(-427.49, 144.33) * mm});
            skLineSegment(sketch, "E1598", {"start": v(-427.49, 144.33) * mm, "end": v(-427.32, 144.71) * mm});
            skLineSegment(sketch, "E1599", {"start": v(-427.32, 144.71) * mm, "end": v(-427.14, 145.09) * mm});
            skLineSegment(sketch, "E1600", {"start": v(-427.14, 145.09) * mm, "end": v(-426.96, 145.46) * mm});
            skLineSegment(sketch, "E1601", {"start": v(-426.96, 145.46) * mm, "end": v(-426.76, 145.82) * mm});
            skLineSegment(sketch, "E1602", {"start": v(-426.76, 145.82) * mm, "end": v(-426.56, 146.18) * mm});
            skLineSegment(sketch, "E1603", {"start": v(-426.56, 146.18) * mm, "end": v(-426.35, 146.54) * mm});
            skLineSegment(sketch, "E1604", {"start": v(-426.35, 146.54) * mm, "end": v(-426.12, 146.89) * mm});
            skLineSegment(sketch, "E1605", {"start": v(-426.12, 146.89) * mm, "end": v(-425.9, 147.23) * mm});
            skLineSegment(sketch, "E1606", {"start": v(-425.9, 147.23) * mm, "end": v(-425.65, 147.57) * mm});
            skLineSegment(sketch, "E1607", {"start": v(-425.65, 147.57) * mm, "end": v(-425.4, 147.9) * mm});
            skLineSegment(sketch, "E1608", {"start": v(-425.4, 147.9) * mm, "end": v(-425.15, 148.23) * mm});
            skLineSegment(sketch, "E1609", {"start": v(-425.15, 148.23) * mm, "end": v(-424.88, 148.56) * mm});
            skLineSegment(sketch, "E1610", {"start": v(-424.88, 148.56) * mm, "end": v(-424.6, 148.87) * mm});
            skLineSegment(sketch, "E1611", {"start": v(-424.6, 148.87) * mm, "end": v(-424.32, 149.18) * mm});
            skLineSegment(sketch, "E1612", {"start": v(-424.32, 149.18) * mm, "end": v(-424.03, 149.48) * mm});
            skLineSegment(sketch, "E1613", {"start": v(-424.03, 149.48) * mm, "end": v(-423.65, 149.83) * mm});
            skLineSegment(sketch, "E1614", {"start": v(-423.65, 149.83) * mm, "end": v(-423.26, 150.17) * mm});
            skLineSegment(sketch, "E1615", {"start": v(-423.26, 150.17) * mm, "end": v(-422.87, 150.5) * mm});
            skLineSegment(sketch, "E1616", {"start": v(-422.87, 150.5) * mm, "end": v(-422.46, 150.82) * mm});
            skLineSegment(sketch, "E1617", {"start": v(-422.46, 150.82) * mm, "end": v(-422.05, 151.13) * mm});
            skLineSegment(sketch, "E1618", {"start": v(-422.05, 151.13) * mm, "end": v(-421.64, 151.43) * mm});
            skLineSegment(sketch, "E1619", {"start": v(-421.64, 151.43) * mm, "end": v(-421.21, 151.71) * mm});
            skLineSegment(sketch, "E1620", {"start": v(-421.21, 151.71) * mm, "end": v(-420.78, 151.99) * mm});
            skLineSegment(sketch, "E1621", {"start": v(-420.78, 151.99) * mm, "end": v(-420.34, 152.25) * mm});
            skLineSegment(sketch, "E1622", {"start": v(-420.34, 152.25) * mm, "end": v(-419.9, 152.5) * mm});
            skLineSegment(sketch, "E1623", {"start": v(-419.9, 152.5) * mm, "end": v(-419.45, 152.75) * mm});
            skLineSegment(sketch, "E1624", {"start": v(-419.45, 152.75) * mm, "end": v(-419, 152.98) * mm});
            skLineSegment(sketch, "E1625", {"start": v(-419, 152.98) * mm, "end": v(-418.54, 153.2) * mm});
            skLineSegment(sketch, "E1626", {"start": v(-418.54, 153.2) * mm, "end": v(-418.07, 153.4) * mm});
            skLineSegment(sketch, "E1627", {"start": v(-418.07, 153.4) * mm, "end": v(-417.6, 153.6) * mm});
            skLineSegment(sketch, "E1628", {"start": v(-417.6, 153.6) * mm, "end": v(-417.13, 153.8) * mm});
            skLineSegment(sketch, "E1629", {"start": v(-417.13, 153.8) * mm, "end": v(-416.65, 153.96) * mm});
            skLineSegment(sketch, "E1630", {"start": v(-416.65, 153.96) * mm, "end": v(-416.17, 154.13) * mm});
            skLineSegment(sketch, "E1631", {"start": v(-416.17, 154.13) * mm, "end": v(-415.68, 154.28) * mm});
            skLineSegment(sketch, "E1632", {"start": v(-415.68, 154.28) * mm, "end": v(-415.2, 154.42) * mm});
            skLineSegment(sketch, "E1633", {"start": v(-415.2, 154.42) * mm, "end": v(-414.7, 154.54) * mm});
            skLineSegment(sketch, "E1634", {"start": v(-414.7, 154.54) * mm, "end": v(-414.2, 154.66) * mm});
            skLineSegment(sketch, "E1635", {"start": v(-414.2, 154.66) * mm, "end": v(-413.7, 154.76) * mm});
            skLineSegment(sketch, "E1636", {"start": v(-413.7, 154.76) * mm, "end": v(-413.2, 154.85) * mm});
            skLineSegment(sketch, "E1637", {"start": v(-413.2, 154.85) * mm, "end": v(-412.7, 154.92) * mm});
            skLineSegment(sketch, "E1638", {"start": v(-412.7, 154.92) * mm, "end": v(-412.18, 154.99) * mm});
            skLineSegment(sketch, "E1639", {"start": v(-412.18, 154.99) * mm, "end": v(-411.67, 155.04) * mm});
            skLineSegment(sketch, "E1640", {"start": v(-411.67, 155.04) * mm, "end": v(-411.16, 155.08) * mm});
            skLineSegment(sketch, "E1641", {"start": v(-411.16, 155.08) * mm, "end": v(-410.65, 155.1) * mm});
            skLineSegment(sketch, "E1642", {"start": v(-410.65, 155.1) * mm, "end": v(-410.13, 155.12) * mm});
            skLineSegment(sketch, "E1643", {"start": v(-410.13, 155.12) * mm, "end": v(-409.62, 155.12) * mm});
            skLineSegment(sketch, "E1644", {"start": v(-409.62, 155.12) * mm, "end": v(-409.1, 155.11) * mm});
            skLineSegment(sketch, "E1645", {"start": v(-409.1, 155.11) * mm, "end": v(-408.54, 155.13) * mm});
            skLineSegment(sketch, "E1646", {"start": v(-408.54, 155.13) * mm, "end": v(-407.98, 155.13) * mm});
            skLineSegment(sketch, "E1647", {"start": v(-407.98, 155.13) * mm, "end": v(-407.42, 155.12) * mm});
            skLineSegment(sketch, "E1648", {"start": v(-407.42, 155.12) * mm, "end": v(-406.86, 155.09) * mm});
            skLineSegment(sketch, "E1649", {"start": v(-406.86, 155.09) * mm, "end": v(-406.3, 155.05) * mm});
            skLineSegment(sketch, "E1650", {"start": v(-406.3, 155.05) * mm, "end": v(-405.75, 155) * mm});
            skLineSegment(sketch, "E1651", {"start": v(-405.75, 155) * mm, "end": v(-405.2, 154.93) * mm});
            skLineSegment(sketch, "E1652", {"start": v(-405.2, 154.93) * mm, "end": v(-404.65, 154.84) * mm});
            skLineSegment(sketch, "E1653", {"start": v(-404.65, 154.84) * mm, "end": v(-404.1, 154.75) * mm});
            skLineSegment(sketch, "E1654", {"start": v(-404.1, 154.75) * mm, "end": v(-403.56, 154.64) * mm});
            skLineSegment(sketch, "E1655", {"start": v(-403.56, 154.64) * mm, "end": v(-403.02, 154.52) * mm});
            skLineSegment(sketch, "E1656", {"start": v(-403.02, 154.52) * mm, "end": v(-402.49, 154.38) * mm});
            skLineSegment(sketch, "E1657", {"start": v(-402.49, 154.38) * mm, "end": v(-401.95, 154.23) * mm});
            skLineSegment(sketch, "E1658", {"start": v(-401.95, 154.23) * mm, "end": v(-401.42, 154.07) * mm});
            skLineSegment(sketch, "E1659", {"start": v(-401.42, 154.07) * mm, "end": v(-400.9, 153.9) * mm});
            skLineSegment(sketch, "E1660", {"start": v(-400.9, 153.9) * mm, "end": v(-400.38, 153.7) * mm});
            skLineSegment(sketch, "E1661", {"start": v(-400.38, 153.7) * mm, "end": v(-399.86, 153.5) * mm});
            skLineSegment(sketch, "E1662", {"start": v(-399.86, 153.5) * mm, "end": v(-399.35, 153.3) * mm});
            skLineSegment(sketch, "E1663", {"start": v(-399.35, 153.3) * mm, "end": v(-398.85, 153.07) * mm});
            skLineSegment(sketch, "E1664", {"start": v(-398.85, 153.07) * mm, "end": v(-398.35, 152.83) * mm});
            skLineSegment(sketch, "E1665", {"start": v(-398.35, 152.83) * mm, "end": v(-397.86, 152.58) * mm});
            skLineSegment(sketch, "E1666", {"start": v(-397.86, 152.58) * mm, "end": v(-397.37, 152.31) * mm});
            skLineSegment(sketch, "E1667", {"start": v(-397.37, 152.31) * mm, "end": v(-396.9, 152.04) * mm});
            skLineSegment(sketch, "E1668", {"start": v(-396.9, 152.04) * mm, "end": v(-396.42, 151.75) * mm});
            skLineSegment(sketch, "E1669", {"start": v(-396.42, 151.75) * mm, "end": v(-395.95, 151.45) * mm});
            skLineSegment(sketch, "E1670", {"start": v(-395.95, 151.45) * mm, "end": v(-395.49, 151.14) * mm});
            skLineSegment(sketch, "E1671", {"start": v(-395.49, 151.14) * mm, "end": v(-395.04, 150.81) * mm});
            skLineSegment(sketch, "E1672", {"start": v(-395.04, 150.81) * mm, "end": v(-394.6, 150.48) * mm});
            skLineSegment(sketch, "E1673", {"start": v(-394.6, 150.48) * mm, "end": v(-394.15, 150.13) * mm});
            skLineSegment(sketch, "E1674", {"start": v(-394.15, 150.13) * mm, "end": v(-393.73, 149.77) * mm});
            skLineSegment(sketch, "E1675", {"start": v(-393.73, 149.77) * mm, "end": v(-393.3, 149.4) * mm});
            skLineSegment(sketch, "E1676", {"start": v(-393.3, 149.4) * mm, "end": v(-392.9, 149.02) * mm});
            skLineSegment(sketch, "E1677", {"start": v(-392.9, 149.02) * mm, "end": v(-392.6, 148.73) * mm});
            skLineSegment(sketch, "E1678", {"start": v(-392.6, 148.73) * mm, "end": v(-392.32, 148.44) * mm});
            skLineSegment(sketch, "E1679", {"start": v(-392.32, 148.44) * mm, "end": v(-392.05, 148.14) * mm});
            skLineSegment(sketch, "E1680", {"start": v(-392.05, 148.14) * mm, "end": v(-391.78, 147.84) * mm});
            skLineSegment(sketch, "E1681", {"start": v(-391.78, 147.84) * mm, "end": v(-391.52, 147.52) * mm});
            skLineSegment(sketch, "E1682", {"start": v(-391.52, 147.52) * mm, "end": v(-391.27, 147.2) * mm});
            skLineSegment(sketch, "E1683", {"start": v(-391.27, 147.2) * mm, "end": v(-391.03, 146.88) * mm});
            skLineSegment(sketch, "E1684", {"start": v(-391.03, 146.88) * mm, "end": v(-390.8, 146.55) * mm});
            skLineSegment(sketch, "E1685", {"start": v(-390.8, 146.55) * mm, "end": v(-390.58, 146.22) * mm});
            skLineSegment(sketch, "E1686", {"start": v(-390.58, 146.22) * mm, "end": v(-390.37, 145.88) * mm});
            skLineSegment(sketch, "E1687", {"start": v(-390.37, 145.88) * mm, "end": v(-390.16, 145.53) * mm});
            skLineSegment(sketch, "E1688", {"start": v(-390.16, 145.53) * mm, "end": v(-389.96, 145.18) * mm});
            skLineSegment(sketch, "E1689", {"start": v(-389.96, 145.18) * mm, "end": v(-389.78, 144.83) * mm});
            skLineSegment(sketch, "E1690", {"start": v(-389.78, 144.83) * mm, "end": v(-389.6, 144.47) * mm});
            skLineSegment(sketch, "E1691", {"start": v(-389.6, 144.47) * mm, "end": v(-389.43, 144.1) * mm});
            skLineSegment(sketch, "E1692", {"start": v(-389.43, 144.1) * mm, "end": v(-389.27, 143.73) * mm});
            skLineSegment(sketch, "E1693", {"start": v(-389.27, 143.73) * mm, "end": v(-389.12, 143.36) * mm});
            skLineSegment(sketch, "E1694", {"start": v(-389.12, 143.36) * mm, "end": v(-388.98, 142.99) * mm});
            skLineSegment(sketch, "E1695", {"start": v(-388.98, 142.99) * mm, "end": v(-388.85, 142.6) * mm});
            skLineSegment(sketch, "E1696", {"start": v(-388.85, 142.6) * mm, "end": v(-388.73, 142.22) * mm});
            skLineSegment(sketch, "E1697", {"start": v(-388.73, 142.22) * mm, "end": v(-388.62, 141.84) * mm});
            skLineSegment(sketch, "E1698", {"start": v(-388.62, 141.84) * mm, "end": v(-388.52, 141.45) * mm});
            skLineSegment(sketch, "E1699", {"start": v(-388.52, 141.45) * mm, "end": v(-388.43, 141.06) * mm});
            skLineSegment(sketch, "E1700", {"start": v(-388.43, 141.06) * mm, "end": v(-388.35, 140.66) * mm});
            skLineSegment(sketch, "E1701", {"start": v(-388.35, 140.66) * mm, "end": v(-388.28, 140.27) * mm});
            skLineSegment(sketch, "E1702", {"start": v(-388.28, 140.27) * mm, "end": v(-388.21, 139.87) * mm});
            skLineSegment(sketch, "E1703", {"start": v(-388.21, 139.87) * mm, "end": v(-388.16, 139.47) * mm});
            skLineSegment(sketch, "E1704", {"start": v(-388.16, 139.47) * mm, "end": v(-388.12, 139.06) * mm});
            skLineSegment(sketch, "E1705", {"start": v(-388.12, 139.06) * mm, "end": v(-388.1, 138.66) * mm});
            skLineSegment(sketch, "E1706", {"start": v(-388.1, 138.66) * mm, "end": v(-388.07, 138.26) * mm});
            skLineSegment(sketch, "E1707", {"start": v(-388.07, 138.26) * mm, "end": v(-388.06, 137.85) * mm});
            skLineSegment(sketch, "E1708", {"start": v(-388.06, 137.85) * mm, "end": v(-388.07, 137.44) * mm});
            skLineSegment(sketch, "E1709", {"start": v(-388.07, 137.44) * mm, "end": v(-388.07, 137.03) * mm});
            skLineSegment(sketch, "E1710", {"start": v(-388.07, 137.03) * mm, "end": v(-388.08, 136.61) * mm});
            skLineSegment(sketch, "E1711", {"start": v(-388.08, 136.61) * mm, "end": v(-388.1, 136.2) * mm});
            skLineSegment(sketch, "E1712", {"start": v(-388.1, 136.2) * mm, "end": v(-388.15, 135.8) * mm});
            skLineSegment(sketch, "E1713", {"start": v(-388.15, 135.8) * mm, "end": v(-388.2, 135.38) * mm});
            skLineSegment(sketch, "E1714", {"start": v(-388.2, 135.38) * mm, "end": v(-388.25, 134.98) * mm});
            skLineSegment(sketch, "E1715", {"start": v(-388.25, 134.98) * mm, "end": v(-388.32, 134.57) * mm});
            skLineSegment(sketch, "E1716", {"start": v(-388.32, 134.57) * mm, "end": v(-388.4, 134.17) * mm});
            skLineSegment(sketch, "E1717", {"start": v(-388.4, 134.17) * mm, "end": v(-388.48, 133.77) * mm});
            skLineSegment(sketch, "E1718", {"start": v(-388.48, 133.77) * mm, "end": v(-388.58, 133.37) * mm});
            skLineSegment(sketch, "E1719", {"start": v(-388.58, 133.37) * mm, "end": v(-388.69, 132.98) * mm});
            skLineSegment(sketch, "E1720", {"start": v(-388.69, 132.98) * mm, "end": v(-388.8, 132.59) * mm});
            skLineSegment(sketch, "E1721", {"start": v(-388.8, 132.59) * mm, "end": v(-388.93, 132.2) * mm});
            skLineSegment(sketch, "E1722", {"start": v(-388.93, 132.2) * mm, "end": v(-389.07, 131.82) * mm});
            skLineSegment(sketch, "E1723", {"start": v(-389.07, 131.82) * mm, "end": v(-389.22, 131.44) * mm});
            skLineSegment(sketch, "E1724", {"start": v(-389.22, 131.44) * mm, "end": v(-389.37, 131.06) * mm});
            skLineSegment(sketch, "E1725", {"start": v(-389.37, 131.06) * mm, "end": v(-389.54, 130.69) * mm});
            skLineSegment(sketch, "E1726", {"start": v(-389.54, 130.69) * mm, "end": v(-389.71, 130.32) * mm});
            skLineSegment(sketch, "E1727", {"start": v(-389.71, 130.32) * mm, "end": v(-389.9, 129.96) * mm});
            skLineSegment(sketch, "E1728", {"start": v(-389.9, 129.96) * mm, "end": v(-390.1, 129.6) * mm});
            skLineSegment(sketch, "E1729", {"start": v(-390.1, 129.6) * mm, "end": v(-390.3, 129.24) * mm});
            skLineSegment(sketch, "E1730", {"start": v(-390.3, 129.24) * mm, "end": v(-390.5, 128.9) * mm});
            skLineSegment(sketch, "E1731", {"start": v(-390.5, 128.9) * mm, "end": v(-390.73, 128.55) * mm});
            skLineSegment(sketch, "E1732", {"start": v(-390.73, 128.55) * mm, "end": v(-390.96, 128.21) * mm});
            skLineSegment(sketch, "E1733", {"start": v(-390.96, 128.21) * mm, "end": v(-391.2, 127.88) * mm});
            skLineSegment(sketch, "E1734", {"start": v(-391.2, 127.88) * mm, "end": v(-391.45, 127.56) * mm});
            skLineSegment(sketch, "E1735", {"start": v(-391.45, 127.56) * mm, "end": v(-391.7, 127.23) * mm});
            skLineSegment(sketch, "E1736", {"start": v(-391.7, 127.23) * mm, "end": v(-391.97, 126.92) * mm});
            skLineSegment(sketch, "E1737", {"start": v(-391.97, 126.92) * mm, "end": v(-392.25, 126.61) * mm});
            skLineSegment(sketch, "E1738", {"start": v(-392.25, 126.61) * mm, "end": v(-392.53, 126.31) * mm});
            skLineSegment(sketch, "E1739", {"start": v(-392.53, 126.31) * mm, "end": v(-392.82, 126.02) * mm});
            skLineSegment(sketch, "E1740", {"start": v(-392.82, 126.02) * mm, "end": v(-393.12, 125.73) * mm});
            skLineSegment(sketch, "E1741", {"start": v(-393.12, 125.73) * mm, "end": v(-393.53, 125.36) * mm});
            skLineSegment(sketch, "E1742", {"start": v(-393.53, 125.36) * mm, "end": v(-393.94, 125) * mm});
            skLineSegment(sketch, "E1743", {"start": v(-393.94, 125) * mm, "end": v(-394.37, 124.65) * mm});
            skLineSegment(sketch, "E1744", {"start": v(-394.37, 124.65) * mm, "end": v(-394.8, 124.32) * mm});
            skLineSegment(sketch, "E1745", {"start": v(-394.8, 124.32) * mm, "end": v(-395.25, 124) * mm});
            skLineSegment(sketch, "E1746", {"start": v(-395.25, 124) * mm, "end": v(-395.7, 123.68) * mm});
            skLineSegment(sketch, "E1747", {"start": v(-395.7, 123.68) * mm, "end": v(-396.15, 123.38) * mm});
            skLineSegment(sketch, "E1748", {"start": v(-396.15, 123.38) * mm, "end": v(-396.61, 123.09) * mm});
            skLineSegment(sketch, "E1749", {"start": v(-396.61, 123.09) * mm, "end": v(-397.08, 122.81) * mm});
            skLineSegment(sketch, "E1750", {"start": v(-397.08, 122.81) * mm, "end": v(-397.56, 122.54) * mm});
            skLineSegment(sketch, "E1751", {"start": v(-397.56, 122.54) * mm, "end": v(-398.04, 122.3) * mm});
            skLineSegment(sketch, "E1752", {"start": v(-398.04, 122.3) * mm, "end": v(-398.53, 122.05) * mm});
            skLineSegment(sketch, "E1753", {"start": v(-398.53, 122.05) * mm, "end": v(-399.02, 121.82) * mm});
            skLineSegment(sketch, "E1754", {"start": v(-399.02, 121.82) * mm, "end": v(-399.52, 121.6) * mm});
            skLineSegment(sketch, "E1755", {"start": v(-399.52, 121.6) * mm, "end": v(-400.03, 121.4) * mm});
            skLineSegment(sketch, "E1756", {"start": v(-400.03, 121.4) * mm, "end": v(-400.53, 121.2) * mm});
            skLineSegment(sketch, "E1757", {"start": v(-400.53, 121.2) * mm, "end": v(-401.05, 121.02) * mm});
            skLineSegment(sketch, "E1758", {"start": v(-401.05, 121.02) * mm, "end": v(-401.57, 120.86) * mm});
            skLineSegment(sketch, "E1759", {"start": v(-401.57, 120.86) * mm, "end": v(-402.09, 120.7) * mm});
            skLineSegment(sketch, "E1760", {"start": v(-402.09, 120.7) * mm, "end": v(-402.61, 120.56) * mm});
            skLineSegment(sketch, "E1761", {"start": v(-402.61, 120.56) * mm, "end": v(-403.14, 120.43) * mm});
            skLineSegment(sketch, "E1762", {"start": v(-403.14, 120.43) * mm, "end": v(-403.67, 120.32) * mm});
            skLineSegment(sketch, "E1763", {"start": v(-403.67, 120.32) * mm, "end": v(-404.2, 120.21) * mm});
            skLineSegment(sketch, "E1764", {"start": v(-404.2, 120.21) * mm, "end": v(-404.75, 120.12) * mm});
            skLineSegment(sketch, "E1765", {"start": v(-404.75, 120.12) * mm, "end": v(-405.29, 120.05) * mm});
            skLineSegment(sketch, "E1766", {"start": v(-405.29, 120.05) * mm, "end": v(-405.83, 119.99) * mm});
            skLineSegment(sketch, "E1767", {"start": v(-405.83, 119.99) * mm, "end": v(-406.38, 119.94) * mm});
            skLineSegment(sketch, "E1768", {"start": v(-406.38, 119.94) * mm, "end": v(-406.92, 119.9) * mm});
            skLineSegment(sketch, "E1769", {"start": v(-406.92, 119.9) * mm, "end": v(-407.47, 119.88) * mm});
            skLineSegment(sketch, "E1770", {"start": v(-407.47, 119.88) * mm, "end": v(-408.02, 119.87) * mm});
            skLineSegment(sketch, "E1771", {"start": v(-408.02, 119.87) * mm, "end": v(-408.57, 119.88) * mm});
            skLineSegment(sketch, "E1772", {"start": v(-408.57, 119.88) * mm, "end": v(-409.13, 119.9) * mm});
            skLineSegment(sketch, "E1773", {"start": v(-409.13, 119.9) * mm, "end": v(-409.64, 119.89) * mm});
            skLineSegment(sketch, "E1774", {"start": v(-409.64, 119.89) * mm, "end": v(-410.15, 119.9) * mm});
            skLineSegment(sketch, "E1775", {"start": v(-410.15, 119.9) * mm, "end": v(-410.67, 119.91) * mm});
            skLineSegment(sketch, "E1776", {"start": v(-410.67, 119.91) * mm, "end": v(-411.18, 119.94) * mm});
            skLineSegment(sketch, "E1777", {"start": v(-411.18, 119.94) * mm, "end": v(-411.69, 119.98) * mm});
            skLineSegment(sketch, "E1778", {"start": v(-411.69, 119.98) * mm, "end": v(-412.2, 120.04) * mm});
            skLineSegment(sketch, "E1779", {"start": v(-412.2, 120.04) * mm, "end": v(-412.7, 120.1) * mm});
            skLineSegment(sketch, "E1780", {"start": v(-412.7, 120.1) * mm, "end": v(-413.2, 120.2) * mm});
            skLineSegment(sketch, "E1781", {"start": v(-413.2, 120.2) * mm, "end": v(-413.7, 120.28) * mm});
            skLineSegment(sketch, "E1782", {"start": v(-413.7, 120.28) * mm, "end": v(-414.2, 120.4) * mm});
            skLineSegment(sketch, "E1783", {"start": v(-414.2, 120.4) * mm, "end": v(-414.7, 120.5) * mm});
            skLineSegment(sketch, "E1784", {"start": v(-414.7, 120.5) * mm, "end": v(-415.18, 120.64) * mm});
            skLineSegment(sketch, "E1785", {"start": v(-415.18, 120.64) * mm, "end": v(-415.67, 120.78) * mm});
            skLineSegment(sketch, "E1786", {"start": v(-415.67, 120.78) * mm, "end": v(-416.16, 120.94) * mm});
            skLineSegment(sketch, "E1787", {"start": v(-416.16, 120.94) * mm, "end": v(-416.63, 121.1) * mm});
            skLineSegment(sketch, "E1788", {"start": v(-416.63, 121.1) * mm, "end": v(-417.1, 121.28) * mm});
            skLineSegment(sketch, "E1789", {"start": v(-417.1, 121.28) * mm, "end": v(-417.58, 121.47) * mm});
            skLineSegment(sketch, "E1790", {"start": v(-417.58, 121.47) * mm, "end": v(-418.05, 121.67) * mm});
            skLineSegment(sketch, "E1791", {"start": v(-418.05, 121.67) * mm, "end": v(-418.5, 121.88) * mm});
            skLineSegment(sketch, "E1792", {"start": v(-418.5, 121.88) * mm, "end": v(-418.96, 122.1) * mm});
            skLineSegment(sketch, "E1793", {"start": v(-418.96, 122.1) * mm, "end": v(-419.41, 122.34) * mm});
            skLineSegment(sketch, "E1794", {"start": v(-419.41, 122.34) * mm, "end": v(-419.86, 122.6) * mm});
            skLineSegment(sketch, "E1795", {"start": v(-419.86, 122.6) * mm, "end": v(-420.3, 122.85) * mm});
            skLineSegment(sketch, "E1796", {"start": v(-420.3, 122.85) * mm, "end": v(-420.72, 123.12) * mm});
            skLineSegment(sketch, "E1797", {"start": v(-420.72, 123.12) * mm, "end": v(-421.15, 123.4) * mm});
            skLineSegment(sketch, "E1798", {"start": v(-421.15, 123.4) * mm, "end": v(-421.57, 123.7) * mm});
            skLineSegment(sketch, "E1799", {"start": v(-421.57, 123.7) * mm, "end": v(-421.98, 124) * mm});
            skLineSegment(sketch, "E1800", {"start": v(-421.98, 124) * mm, "end": v(-422.39, 124.3) * mm});
            skLineSegment(sketch, "E1801", {"start": v(-422.39, 124.3) * mm, "end": v(-422.78, 124.63) * mm});
            skLineSegment(sketch, "E1802", {"start": v(-422.78, 124.63) * mm, "end": v(-423.17, 124.96) * mm});
            skLineSegment(sketch, "E1803", {"start": v(-423.17, 124.96) * mm, "end": v(-423.55, 125.3) * mm});
            skLineSegment(sketch, "E1804", {"start": v(-423.55, 125.3) * mm, "end": v(-423.93, 125.66) * mm});
            skLineSegment(sketch, "E1805", {"start": v(-423.93, 125.66) * mm, "end": v(-424.22, 125.95) * mm});
            skLineSegment(sketch, "E1806", {"start": v(-424.22, 125.95) * mm, "end": v(-424.5, 126.25) * mm});
            skLineSegment(sketch, "E1807", {"start": v(-424.5, 126.25) * mm, "end": v(-424.78, 126.56) * mm});
            skLineSegment(sketch, "E1808", {"start": v(-424.78, 126.56) * mm, "end": v(-425.04, 126.87) * mm});
            skLineSegment(sketch, "E1809", {"start": v(-425.04, 126.87) * mm, "end": v(-425.3, 127.2) * mm});
            skLineSegment(sketch, "E1810", {"start": v(-425.3, 127.2) * mm, "end": v(-425.55, 127.52) * mm});
            skLineSegment(sketch, "E1811", {"start": v(-425.55, 127.52) * mm, "end": v(-425.8, 127.85) * mm});
            skLineSegment(sketch, "E1812", {"start": v(-425.8, 127.85) * mm, "end": v(-426.03, 128.19) * mm});
            skLineSegment(sketch, "E1813", {"start": v(-426.03, 128.19) * mm, "end": v(-426.25, 128.53) * mm});
            skLineSegment(sketch, "E1814", {"start": v(-426.25, 128.53) * mm, "end": v(-426.46, 128.88) * mm});
            skLineSegment(sketch, "E1815", {"start": v(-426.46, 128.88) * mm, "end": v(-426.67, 129.23) * mm});
            skLineSegment(sketch, "E1816", {"start": v(-426.67, 129.23) * mm, "end": v(-426.87, 129.59) * mm});
            skLineSegment(sketch, "E1817", {"start": v(-426.87, 129.59) * mm, "end": v(-427.06, 129.95) * mm});
            skLineSegment(sketch, "E1818", {"start": v(-427.06, 129.95) * mm, "end": v(-427.24, 130.31) * mm});
            skLineSegment(sketch, "E1819", {"start": v(-427.24, 130.31) * mm, "end": v(-427.4, 130.68) * mm});
            skLineSegment(sketch, "E1820", {"start": v(-427.4, 130.68) * mm, "end": v(-427.57, 131.06) * mm});
            skLineSegment(sketch, "E1821", {"start": v(-427.57, 131.06) * mm, "end": v(-427.72, 131.44) * mm});
            skLineSegment(sketch, "E1822", {"start": v(-427.72, 131.44) * mm, "end": v(-427.86, 131.82) * mm});
            skLineSegment(sketch, "E1823", {"start": v(-427.86, 131.82) * mm, "end": v(-428, 132.2) * mm});
            skLineSegment(sketch, "E1824", {"start": v(-428, 132.2) * mm, "end": v(-428.12, 132.6) * mm});
            skLineSegment(sketch, "E1825", {"start": v(-428.12, 132.6) * mm, "end": v(-428.23, 132.99) * mm});
            skLineSegment(sketch, "E1826", {"start": v(-428.23, 132.99) * mm, "end": v(-428.34, 133.38) * mm});
            skLineSegment(sketch, "E1827", {"start": v(-428.34, 133.38) * mm, "end": v(-428.43, 133.78) * mm});
            skLineSegment(sketch, "E1828", {"start": v(-428.43, 133.78) * mm, "end": v(-428.52, 134.18) * mm});
            skLineSegment(sketch, "E1829", {"start": v(-428.52, 134.18) * mm, "end": v(-428.59, 134.58) * mm});
            skLineSegment(sketch, "E1830", {"start": v(-428.59, 134.58) * mm, "end": v(-428.65, 134.99) * mm});
            skLineSegment(sketch, "E1831", {"start": v(-428.65, 134.99) * mm, "end": v(-428.7, 135.4) * mm});
            skLineSegment(sketch, "E1832", {"start": v(-428.7, 135.4) * mm, "end": v(-428.75, 135.8) * mm});
            skLineSegment(sketch, "E1833", {"start": v(-428.75, 135.8) * mm, "end": v(-428.79, 136.21) * mm});
            skLineSegment(sketch, "E1834", {"start": v(-428.79, 136.21) * mm, "end": v(-428.81, 136.62) * mm});
            skLineSegment(sketch, "E1835", {"start": v(-428.81, 136.62) * mm, "end": v(-428.82, 137.04) * mm});
            skLineSegment(sketch, "E1836", {"start": v(-428.82, 137.04) * mm, "end": v(-428.83, 137.45) * mm});
            skLineSegment(sketch, "E1837", {"start": v(-428.83, 93.2) * mm, "end": v(-428.83, 93.62) * mm});
            skLineSegment(sketch, "E1838", {"start": v(-428.83, 93.62) * mm, "end": v(-428.82, 94.04) * mm});
            skLineSegment(sketch, "E1839", {"start": v(-428.82, 94.04) * mm, "end": v(-428.8, 94.46) * mm});
            skLineSegment(sketch, "E1840", {"start": v(-428.8, 94.46) * mm, "end": v(-428.78, 94.88) * mm});
            skLineSegment(sketch, "E1841", {"start": v(-428.78, 94.88) * mm, "end": v(-428.74, 95.3) * mm});
            skLineSegment(sketch, "E1842", {"start": v(-428.74, 95.3) * mm, "end": v(-428.69, 95.7) * mm});
            skLineSegment(sketch, "E1843", {"start": v(-428.69, 95.7) * mm, "end": v(-428.63, 96.12) * mm});
            skLineSegment(sketch, "E1844", {"start": v(-428.63, 96.12) * mm, "end": v(-428.56, 96.53) * mm});
            skLineSegment(sketch, "E1845", {"start": v(-428.56, 96.53) * mm, "end": v(-428.48, 96.93) * mm});
            skLineSegment(sketch, "E1846", {"start": v(-428.48, 96.93) * mm, "end": v(-428.4, 97.34) * mm});
            skLineSegment(sketch, "E1847", {"start": v(-428.4, 97.34) * mm, "end": v(-428.3, 97.74) * mm});
            skLineSegment(sketch, "E1848", {"start": v(-428.3, 97.74) * mm, "end": v(-428.18, 98.14) * mm});
            skLineSegment(sketch, "E1849", {"start": v(-428.18, 98.14) * mm, "end": v(-428.06, 98.54) * mm});
            skLineSegment(sketch, "E1850", {"start": v(-428.06, 98.54) * mm, "end": v(-427.93, 98.93) * mm});
            skLineSegment(sketch, "E1851", {"start": v(-427.93, 98.93) * mm, "end": v(-427.8, 99.32) * mm});
            skLineSegment(sketch, "E1852", {"start": v(-427.8, 99.32) * mm, "end": v(-427.65, 99.7) * mm});
            skLineSegment(sketch, "E1853", {"start": v(-427.65, 99.7) * mm, "end": v(-427.49, 100.09) * mm});
            skLineSegment(sketch, "E1854", {"start": v(-427.49, 100.09) * mm, "end": v(-427.32, 100.47) * mm});
            skLineSegment(sketch, "E1855", {"start": v(-427.32, 100.47) * mm, "end": v(-427.14, 100.84) * mm});
            skLineSegment(sketch, "E1856", {"start": v(-427.14, 100.84) * mm, "end": v(-426.96, 101.21) * mm});
            skLineSegment(sketch, "E1857", {"start": v(-426.96, 101.21) * mm, "end": v(-426.76, 101.58) * mm});
            skLineSegment(sketch, "E1858", {"start": v(-426.76, 101.58) * mm, "end": v(-426.56, 101.94) * mm});
            skLineSegment(sketch, "E1859", {"start": v(-426.56, 101.94) * mm, "end": v(-426.35, 102.3) * mm});
            skLineSegment(sketch, "E1860", {"start": v(-426.35, 102.3) * mm, "end": v(-426.12, 102.64) * mm});
            skLineSegment(sketch, "E1861", {"start": v(-426.12, 102.64) * mm, "end": v(-425.9, 102.99) * mm});
            skLineSegment(sketch, "E1862", {"start": v(-425.9, 102.99) * mm, "end": v(-425.65, 103.33) * mm});
            skLineSegment(sketch, "E1863", {"start": v(-425.65, 103.33) * mm, "end": v(-425.4, 103.66) * mm});
            skLineSegment(sketch, "E1864", {"start": v(-425.4, 103.66) * mm, "end": v(-425.15, 103.99) * mm});
            skLineSegment(sketch, "E1865", {"start": v(-425.15, 103.99) * mm, "end": v(-424.88, 104.31) * mm});
            skLineSegment(sketch, "E1866", {"start": v(-424.88, 104.31) * mm, "end": v(-424.6, 104.63) * mm});
            skLineSegment(sketch, "E1867", {"start": v(-424.6, 104.63) * mm, "end": v(-424.32, 104.94) * mm});
            skLineSegment(sketch, "E1868", {"start": v(-424.32, 104.94) * mm, "end": v(-424.03, 105.24) * mm});
            skLineSegment(sketch, "E1869", {"start": v(-424.03, 105.24) * mm, "end": v(-423.65, 105.59) * mm});
            skLineSegment(sketch, "E1870", {"start": v(-423.65, 105.59) * mm, "end": v(-423.26, 105.93) * mm});
            skLineSegment(sketch, "E1871", {"start": v(-423.26, 105.93) * mm, "end": v(-422.87, 106.26) * mm});
            skLineSegment(sketch, "E1872", {"start": v(-422.87, 106.26) * mm, "end": v(-422.46, 106.58) * mm});
            skLineSegment(sketch, "E1873", {"start": v(-422.46, 106.58) * mm, "end": v(-422.05, 106.88) * mm});
            skLineSegment(sketch, "E1874", {"start": v(-422.05, 106.88) * mm, "end": v(-421.64, 107.18) * mm});
            skLineSegment(sketch, "E1875", {"start": v(-421.64, 107.18) * mm, "end": v(-421.21, 107.47) * mm});
            skLineSegment(sketch, "E1876", {"start": v(-421.21, 107.47) * mm, "end": v(-420.78, 107.74) * mm});
            skLineSegment(sketch, "E1877", {"start": v(-420.78, 107.74) * mm, "end": v(-420.34, 108) * mm});
            skLineSegment(sketch, "E1878", {"start": v(-420.34, 108) * mm, "end": v(-419.9, 108.26) * mm});
            skLineSegment(sketch, "E1879", {"start": v(-419.9, 108.26) * mm, "end": v(-419.45, 108.5) * mm});
            skLineSegment(sketch, "E1880", {"start": v(-419.45, 108.5) * mm, "end": v(-419, 108.73) * mm});
            skLineSegment(sketch, "E1881", {"start": v(-419, 108.73) * mm, "end": v(-418.54, 108.95) * mm});
            skLineSegment(sketch, "E1882", {"start": v(-418.54, 108.95) * mm, "end": v(-418.07, 109.16) * mm});
            skLineSegment(sketch, "E1883", {"start": v(-418.07, 109.16) * mm, "end": v(-417.6, 109.36) * mm});
            skLineSegment(sketch, "E1884", {"start": v(-417.6, 109.36) * mm, "end": v(-417.13, 109.55) * mm});
            skLineSegment(sketch, "E1885", {"start": v(-417.13, 109.55) * mm, "end": v(-416.65, 109.72) * mm});
            skLineSegment(sketch, "E1886", {"start": v(-416.65, 109.72) * mm, "end": v(-416.17, 109.88) * mm});
            skLineSegment(sketch, "E1887", {"start": v(-416.17, 109.88) * mm, "end": v(-415.68, 110.03) * mm});
            skLineSegment(sketch, "E1888", {"start": v(-415.68, 110.03) * mm, "end": v(-415.2, 110.17) * mm});
            skLineSegment(sketch, "E1889", {"start": v(-415.2, 110.17) * mm, "end": v(-414.7, 110.3) * mm});
            skLineSegment(sketch, "E1890", {"start": v(-414.7, 110.3) * mm, "end": v(-414.2, 110.41) * mm});
            skLineSegment(sketch, "E1891", {"start": v(-414.2, 110.41) * mm, "end": v(-413.7, 110.51) * mm});
            skLineSegment(sketch, "E1892", {"start": v(-413.7, 110.51) * mm, "end": v(-413.2, 110.6) * mm});
            skLineSegment(sketch, "E1893", {"start": v(-413.2, 110.6) * mm, "end": v(-412.7, 110.68) * mm});
            skLineSegment(sketch, "E1894", {"start": v(-412.7, 110.68) * mm, "end": v(-412.18, 110.74) * mm});
            skLineSegment(sketch, "E1895", {"start": v(-412.18, 110.74) * mm, "end": v(-411.67, 110.8) * mm});
            skLineSegment(sketch, "E1896", {"start": v(-411.67, 110.8) * mm, "end": v(-411.16, 110.84) * mm});
            skLineSegment(sketch, "E1897", {"start": v(-411.16, 110.84) * mm, "end": v(-410.65, 110.86) * mm});
            skLineSegment(sketch, "E1898", {"start": v(-410.65, 110.86) * mm, "end": v(-410.13, 110.88) * mm});
            skLineSegment(sketch, "E1899", {"start": v(-410.13, 110.88) * mm, "end": v(-409.62, 110.88) * mm});
            skLineSegment(sketch, "E1900", {"start": v(-409.62, 110.88) * mm, "end": v(-409.1, 110.86) * mm});
            skLineSegment(sketch, "E1901", {"start": v(-409.1, 110.86) * mm, "end": v(-408.54, 110.88) * mm});
            skLineSegment(sketch, "E1902", {"start": v(-408.54, 110.88) * mm, "end": v(-407.98, 110.88) * mm});
            skLineSegment(sketch, "E1903", {"start": v(-407.98, 110.88) * mm, "end": v(-407.42, 110.87) * mm});
            skLineSegment(sketch, "E1904", {"start": v(-407.42, 110.87) * mm, "end": v(-406.86, 110.84) * mm});
            skLineSegment(sketch, "E1905", {"start": v(-406.86, 110.84) * mm, "end": v(-406.3, 110.8) * mm});
            skLineSegment(sketch, "E1906", {"start": v(-406.3, 110.8) * mm, "end": v(-405.75, 110.75) * mm});
            skLineSegment(sketch, "E1907", {"start": v(-405.75, 110.75) * mm, "end": v(-405.2, 110.68) * mm});
            skLineSegment(sketch, "E1908", {"start": v(-405.2, 110.68) * mm, "end": v(-404.65, 110.6) * mm});
            skLineSegment(sketch, "E1909", {"start": v(-404.65, 110.6) * mm, "end": v(-404.1, 110.5) * mm});
            skLineSegment(sketch, "E1910", {"start": v(-404.1, 110.5) * mm, "end": v(-403.56, 110.4) * mm});
            skLineSegment(sketch, "E1911", {"start": v(-403.56, 110.4) * mm, "end": v(-403.02, 110.27) * mm});
            skLineSegment(sketch, "E1912", {"start": v(-403.02, 110.27) * mm, "end": v(-402.49, 110.14) * mm});
            skLineSegment(sketch, "E1913", {"start": v(-402.49, 110.14) * mm, "end": v(-401.95, 109.99) * mm});
            skLineSegment(sketch, "E1914", {"start": v(-401.95, 109.99) * mm, "end": v(-401.42, 109.82) * mm});
            skLineSegment(sketch, "E1915", {"start": v(-401.42, 109.82) * mm, "end": v(-400.9, 109.65) * mm});
            skLineSegment(sketch, "E1916", {"start": v(-400.9, 109.65) * mm, "end": v(-400.38, 109.46) * mm});
            skLineSegment(sketch, "E1917", {"start": v(-400.38, 109.46) * mm, "end": v(-399.86, 109.26) * mm});
            skLineSegment(sketch, "E1918", {"start": v(-399.86, 109.26) * mm, "end": v(-399.35, 109.05) * mm});
            skLineSegment(sketch, "E1919", {"start": v(-399.35, 109.05) * mm, "end": v(-398.85, 108.82) * mm});
            skLineSegment(sketch, "E1920", {"start": v(-398.85, 108.82) * mm, "end": v(-398.35, 108.58) * mm});
            skLineSegment(sketch, "E1921", {"start": v(-398.35, 108.58) * mm, "end": v(-397.86, 108.33) * mm});
            skLineSegment(sketch, "E1922", {"start": v(-397.86, 108.33) * mm, "end": v(-397.37, 108.07) * mm});
            skLineSegment(sketch, "E1923", {"start": v(-397.37, 108.07) * mm, "end": v(-396.9, 107.8) * mm});
            skLineSegment(sketch, "E1924", {"start": v(-396.9, 107.8) * mm, "end": v(-396.42, 107.5) * mm});
            skLineSegment(sketch, "E1925", {"start": v(-396.42, 107.5) * mm, "end": v(-395.95, 107.2) * mm});
            skLineSegment(sketch, "E1926", {"start": v(-395.95, 107.2) * mm, "end": v(-395.49, 106.9) * mm});
            skLineSegment(sketch, "E1927", {"start": v(-395.49, 106.9) * mm, "end": v(-395.04, 106.57) * mm});
            skLineSegment(sketch, "E1928", {"start": v(-395.04, 106.57) * mm, "end": v(-394.6, 106.23) * mm});
            skLineSegment(sketch, "E1929", {"start": v(-394.6, 106.23) * mm, "end": v(-394.15, 105.88) * mm});
            skLineSegment(sketch, "E1930", {"start": v(-394.15, 105.88) * mm, "end": v(-393.73, 105.53) * mm});
            skLineSegment(sketch, "E1931", {"start": v(-393.73, 105.53) * mm, "end": v(-393.3, 105.16) * mm});
            skLineSegment(sketch, "E1932", {"start": v(-393.3, 105.16) * mm, "end": v(-392.9, 104.77) * mm});
            skLineSegment(sketch, "E1933", {"start": v(-392.9, 104.77) * mm, "end": v(-392.6, 104.49) * mm});
            skLineSegment(sketch, "E1934", {"start": v(-392.6, 104.49) * mm, "end": v(-392.32, 104.2) * mm});
            skLineSegment(sketch, "E1935", {"start": v(-392.32, 104.2) * mm, "end": v(-392.05, 103.9) * mm});
            skLineSegment(sketch, "E1936", {"start": v(-392.05, 103.9) * mm, "end": v(-391.78, 103.6) * mm});
            skLineSegment(sketch, "E1937", {"start": v(-391.78, 103.6) * mm, "end": v(-391.52, 103.28) * mm});
            skLineSegment(sketch, "E1938", {"start": v(-391.52, 103.28) * mm, "end": v(-391.27, 102.96) * mm});
            skLineSegment(sketch, "E1939", {"start": v(-391.27, 102.96) * mm, "end": v(-391.03, 102.64) * mm});
            skLineSegment(sketch, "E1940", {"start": v(-391.03, 102.64) * mm, "end": v(-390.8, 102.3) * mm});
            skLineSegment(sketch, "E1941", {"start": v(-390.8, 102.3) * mm, "end": v(-390.58, 101.97) * mm});
            skLineSegment(sketch, "E1942", {"start": v(-390.58, 101.97) * mm, "end": v(-390.37, 101.63) * mm});
            skLineSegment(sketch, "E1943", {"start": v(-390.37, 101.63) * mm, "end": v(-390.16, 101.29) * mm});
            skLineSegment(sketch, "E1944", {"start": v(-390.16, 101.29) * mm, "end": v(-389.96, 100.94) * mm});
            skLineSegment(sketch, "E1945", {"start": v(-389.96, 100.94) * mm, "end": v(-389.78, 100.58) * mm});
            skLineSegment(sketch, "E1946", {"start": v(-389.78, 100.58) * mm, "end": v(-389.6, 100.22) * mm});
            skLineSegment(sketch, "E1947", {"start": v(-389.6, 100.22) * mm, "end": v(-389.43, 99.86) * mm});
            skLineSegment(sketch, "E1948", {"start": v(-389.43, 99.86) * mm, "end": v(-389.27, 99.49) * mm});
            skLineSegment(sketch, "E1949", {"start": v(-389.27, 99.49) * mm, "end": v(-389.12, 99.12) * mm});
            skLineSegment(sketch, "E1950", {"start": v(-389.12, 99.12) * mm, "end": v(-388.98, 98.74) * mm});
            skLineSegment(sketch, "E1951", {"start": v(-388.98, 98.74) * mm, "end": v(-388.85, 98.36) * mm});
            skLineSegment(sketch, "E1952", {"start": v(-388.85, 98.36) * mm, "end": v(-388.73, 97.98) * mm});
            skLineSegment(sketch, "E1953", {"start": v(-388.73, 97.98) * mm, "end": v(-388.62, 97.6) * mm});
            skLineSegment(sketch, "E1954", {"start": v(-388.62, 97.6) * mm, "end": v(-388.52, 97.2) * mm});
            skLineSegment(sketch, "E1955", {"start": v(-388.52, 97.2) * mm, "end": v(-388.43, 96.81) * mm});
            skLineSegment(sketch, "E1956", {"start": v(-388.43, 96.81) * mm, "end": v(-388.35, 96.42) * mm});
            skLineSegment(sketch, "E1957", {"start": v(-388.35, 96.42) * mm, "end": v(-388.28, 96.02) * mm});
            skLineSegment(sketch, "E1958", {"start": v(-388.28, 96.02) * mm, "end": v(-388.21, 95.62) * mm});
            skLineSegment(sketch, "E1959", {"start": v(-388.21, 95.62) * mm, "end": v(-388.16, 95.22) * mm});
            skLineSegment(sketch, "E1960", {"start": v(-388.16, 95.22) * mm, "end": v(-388.12, 94.82) * mm});
            skLineSegment(sketch, "E1961", {"start": v(-388.12, 94.82) * mm, "end": v(-388.1, 94.42) * mm});
            skLineSegment(sketch, "E1962", {"start": v(-388.1, 94.42) * mm, "end": v(-388.07, 94) * mm});
            skLineSegment(sketch, "E1963", {"start": v(-388.07, 94) * mm, "end": v(-388.06, 93.6) * mm});
            skLineSegment(sketch, "E1964", {"start": v(-388.06, 93.6) * mm, "end": v(-388.07, 93.2) * mm});
            skLineSegment(sketch, "E1965", {"start": v(-388.07, 93.2) * mm, "end": v(-388.07, 92.78) * mm});
            skLineSegment(sketch, "E1966", {"start": v(-388.07, 92.78) * mm, "end": v(-388.08, 92.37) * mm});
            skLineSegment(sketch, "E1967", {"start": v(-388.08, 92.37) * mm, "end": v(-388.1, 91.96) * mm});
            skLineSegment(sketch, "E1968", {"start": v(-388.1, 91.96) * mm, "end": v(-388.15, 91.55) * mm});
            skLineSegment(sketch, "E1969", {"start": v(-388.15, 91.55) * mm, "end": v(-388.2, 91.14) * mm});
            skLineSegment(sketch, "E1970", {"start": v(-388.2, 91.14) * mm, "end": v(-388.25, 90.73) * mm});
            skLineSegment(sketch, "E1971", {"start": v(-388.25, 90.73) * mm, "end": v(-388.32, 90.33) * mm});
            skLineSegment(sketch, "E1972", {"start": v(-388.32, 90.33) * mm, "end": v(-388.4, 89.92) * mm});
            skLineSegment(sketch, "E1973", {"start": v(-388.4, 89.92) * mm, "end": v(-388.48, 89.52) * mm});
            skLineSegment(sketch, "E1974", {"start": v(-388.48, 89.52) * mm, "end": v(-388.58, 89.13) * mm});
            skLineSegment(sketch, "E1975", {"start": v(-388.58, 89.13) * mm, "end": v(-388.69, 88.73) * mm});
            skLineSegment(sketch, "E1976", {"start": v(-388.69, 88.73) * mm, "end": v(-388.8, 88.34) * mm});
            skLineSegment(sketch, "E1977", {"start": v(-388.8, 88.34) * mm, "end": v(-388.93, 87.96) * mm});
            skLineSegment(sketch, "E1978", {"start": v(-388.93, 87.96) * mm, "end": v(-389.07, 87.57) * mm});
            skLineSegment(sketch, "E1979", {"start": v(-389.07, 87.57) * mm, "end": v(-389.22, 87.2) * mm});
            skLineSegment(sketch, "E1980", {"start": v(-389.22, 87.2) * mm, "end": v(-389.37, 86.81) * mm});
            skLineSegment(sketch, "E1981", {"start": v(-389.37, 86.81) * mm, "end": v(-389.54, 86.44) * mm});
            skLineSegment(sketch, "E1982", {"start": v(-389.54, 86.44) * mm, "end": v(-389.71, 86.07) * mm});
            skLineSegment(sketch, "E1983", {"start": v(-389.71, 86.07) * mm, "end": v(-389.9, 85.71) * mm});
            skLineSegment(sketch, "E1984", {"start": v(-389.9, 85.71) * mm, "end": v(-390.1, 85.35) * mm});
            skLineSegment(sketch, "E1985", {"start": v(-390.1, 85.35) * mm, "end": v(-390.3, 85) * mm});
            skLineSegment(sketch, "E1986", {"start": v(-390.3, 85) * mm, "end": v(-390.5, 84.65) * mm});
            skLineSegment(sketch, "E1987", {"start": v(-390.5, 84.65) * mm, "end": v(-390.73, 84.3) * mm});
            skLineSegment(sketch, "E1988", {"start": v(-390.73, 84.3) * mm, "end": v(-390.96, 83.97) * mm});
            skLineSegment(sketch, "E1989", {"start": v(-390.96, 83.97) * mm, "end": v(-391.2, 83.64) * mm});
            skLineSegment(sketch, "E1990", {"start": v(-391.2, 83.64) * mm, "end": v(-391.45, 83.3) * mm});
            skLineSegment(sketch, "E1991", {"start": v(-391.45, 83.3) * mm, "end": v(-391.7, 82.99) * mm});
            skLineSegment(sketch, "E1992", {"start": v(-391.7, 82.99) * mm, "end": v(-391.97, 82.68) * mm});
            skLineSegment(sketch, "E1993", {"start": v(-391.97, 82.68) * mm, "end": v(-392.25, 82.37) * mm});
            skLineSegment(sketch, "E1994", {"start": v(-392.25, 82.37) * mm, "end": v(-392.53, 82.07) * mm});
            skLineSegment(sketch, "E1995", {"start": v(-392.53, 82.07) * mm, "end": v(-392.82, 81.77) * mm});
            skLineSegment(sketch, "E1996", {"start": v(-392.82, 81.77) * mm, "end": v(-393.12, 81.49) * mm});
            skLineSegment(sketch, "E1997", {"start": v(-393.12, 81.49) * mm, "end": v(-393.53, 81.12) * mm});
            skLineSegment(sketch, "E1998", {"start": v(-393.53, 81.12) * mm, "end": v(-393.94, 80.76) * mm});
            skLineSegment(sketch, "E1999", {"start": v(-393.94, 80.76) * mm, "end": v(-394.37, 80.4) * mm});
            skLineSegment(sketch, "E2000", {"start": v(-394.37, 80.4) * mm, "end": v(-394.8, 80.07) * mm});
            skLineSegment(sketch, "E2001", {"start": v(-394.8, 80.07) * mm, "end": v(-395.25, 79.75) * mm});
            skLineSegment(sketch, "E2002", {"start": v(-395.25, 79.75) * mm, "end": v(-395.7, 79.44) * mm});
            skLineSegment(sketch, "E2003", {"start": v(-395.7, 79.44) * mm, "end": v(-396.15, 79.13) * mm});
            skLineSegment(sketch, "E2004", {"start": v(-396.15, 79.13) * mm, "end": v(-396.61, 78.84) * mm});
            skLineSegment(sketch, "E2005", {"start": v(-396.61, 78.84) * mm, "end": v(-397.08, 78.57) * mm});
            skLineSegment(sketch, "E2006", {"start": v(-397.08, 78.57) * mm, "end": v(-397.56, 78.3) * mm});
            skLineSegment(sketch, "E2007", {"start": v(-397.56, 78.3) * mm, "end": v(-398.04, 78.05) * mm});
            skLineSegment(sketch, "E2008", {"start": v(-398.04, 78.05) * mm, "end": v(-398.53, 77.8) * mm});
            skLineSegment(sketch, "E2009", {"start": v(-398.53, 77.8) * mm, "end": v(-399.02, 77.57) * mm});
            skLineSegment(sketch, "E2010", {"start": v(-399.02, 77.57) * mm, "end": v(-399.52, 77.36) * mm});
            skLineSegment(sketch, "E2011", {"start": v(-399.52, 77.36) * mm, "end": v(-400.03, 77.15) * mm});
            skLineSegment(sketch, "E2012", {"start": v(-400.03, 77.15) * mm, "end": v(-400.53, 76.96) * mm});
            skLineSegment(sketch, "E2013", {"start": v(-400.53, 76.96) * mm, "end": v(-401.05, 76.78) * mm});
            skLineSegment(sketch, "E2014", {"start": v(-401.05, 76.78) * mm, "end": v(-401.57, 76.61) * mm});
            skLineSegment(sketch, "E2015", {"start": v(-401.57, 76.61) * mm, "end": v(-402.09, 76.46) * mm});
            skLineSegment(sketch, "E2016", {"start": v(-402.09, 76.46) * mm, "end": v(-402.61, 76.32) * mm});
            skLineSegment(sketch, "E2017", {"start": v(-402.61, 76.32) * mm, "end": v(-403.14, 76.19) * mm});
            skLineSegment(sketch, "E2018", {"start": v(-403.14, 76.19) * mm, "end": v(-403.67, 76.07) * mm});
            skLineSegment(sketch, "E2019", {"start": v(-403.67, 76.07) * mm, "end": v(-404.2, 75.97) * mm});
            skLineSegment(sketch, "E2020", {"start": v(-404.2, 75.97) * mm, "end": v(-404.75, 75.88) * mm});
            skLineSegment(sketch, "E2021", {"start": v(-404.75, 75.88) * mm, "end": v(-405.29, 75.8) * mm});
            skLineSegment(sketch, "E2022", {"start": v(-405.29, 75.8) * mm, "end": v(-405.83, 75.74) * mm});
            skLineSegment(sketch, "E2023", {"start": v(-405.83, 75.74) * mm, "end": v(-406.38, 75.7) * mm});
            skLineSegment(sketch, "E2024", {"start": v(-406.38, 75.7) * mm, "end": v(-406.92, 75.66) * mm});
            skLineSegment(sketch, "E2025", {"start": v(-406.92, 75.66) * mm, "end": v(-407.47, 75.63) * mm});
            skLineSegment(sketch, "E2026", {"start": v(-407.47, 75.63) * mm, "end": v(-408.02, 75.63) * mm});
            skLineSegment(sketch, "E2027", {"start": v(-408.02, 75.63) * mm, "end": v(-408.57, 75.63) * mm});
            skLineSegment(sketch, "E2028", {"start": v(-408.57, 75.63) * mm, "end": v(-409.13, 75.65) * mm});
            skLineSegment(sketch, "E2029", {"start": v(-409.13, 75.65) * mm, "end": v(-409.64, 75.64) * mm});
            skLineSegment(sketch, "E2030", {"start": v(-409.64, 75.64) * mm, "end": v(-410.15, 75.65) * mm});
            skLineSegment(sketch, "E2031", {"start": v(-410.15, 75.65) * mm, "end": v(-410.67, 75.67) * mm});
            skLineSegment(sketch, "E2032", {"start": v(-410.67, 75.67) * mm, "end": v(-411.18, 75.7) * mm});
            skLineSegment(sketch, "E2033", {"start": v(-411.18, 75.7) * mm, "end": v(-411.69, 75.74) * mm});
            skLineSegment(sketch, "E2034", {"start": v(-411.69, 75.74) * mm, "end": v(-412.2, 75.8) * mm});
            skLineSegment(sketch, "E2035", {"start": v(-412.2, 75.8) * mm, "end": v(-412.7, 75.86) * mm});
            skLineSegment(sketch, "E2036", {"start": v(-412.7, 75.86) * mm, "end": v(-413.2, 75.95) * mm});
            skLineSegment(sketch, "E2037", {"start": v(-413.2, 75.95) * mm, "end": v(-413.7, 76.04) * mm});
            skLineSegment(sketch, "E2038", {"start": v(-413.7, 76.04) * mm, "end": v(-414.2, 76.14) * mm});
            skLineSegment(sketch, "E2039", {"start": v(-414.2, 76.14) * mm, "end": v(-414.7, 76.26) * mm});
            skLineSegment(sketch, "E2040", {"start": v(-414.7, 76.26) * mm, "end": v(-415.18, 76.4) * mm});
            skLineSegment(sketch, "E2041", {"start": v(-415.18, 76.4) * mm, "end": v(-415.67, 76.54) * mm});
            skLineSegment(sketch, "E2042", {"start": v(-415.67, 76.54) * mm, "end": v(-416.16, 76.7) * mm});
            skLineSegment(sketch, "E2043", {"start": v(-416.16, 76.7) * mm, "end": v(-416.63, 76.86) * mm});
            skLineSegment(sketch, "E2044", {"start": v(-416.63, 76.86) * mm, "end": v(-417.1, 77.03) * mm});
            skLineSegment(sketch, "E2045", {"start": v(-417.1, 77.03) * mm, "end": v(-417.58, 77.22) * mm});
            skLineSegment(sketch, "E2046", {"start": v(-417.58, 77.22) * mm, "end": v(-418.05, 77.43) * mm});
            skLineSegment(sketch, "E2047", {"start": v(-418.05, 77.43) * mm, "end": v(-418.5, 77.64) * mm});
            skLineSegment(sketch, "E2048", {"start": v(-418.5, 77.64) * mm, "end": v(-418.96, 77.86) * mm});
            skLineSegment(sketch, "E2049", {"start": v(-418.96, 77.86) * mm, "end": v(-419.41, 78.1) * mm});
            skLineSegment(sketch, "E2050", {"start": v(-419.41, 78.1) * mm, "end": v(-419.86, 78.35) * mm});
            skLineSegment(sketch, "E2051", {"start": v(-419.86, 78.35) * mm, "end": v(-420.3, 78.6) * mm});
            skLineSegment(sketch, "E2052", {"start": v(-420.3, 78.6) * mm, "end": v(-420.72, 78.87) * mm});
            skLineSegment(sketch, "E2053", {"start": v(-420.72, 78.87) * mm, "end": v(-421.15, 79.15) * mm});
            skLineSegment(sketch, "E2054", {"start": v(-421.15, 79.15) * mm, "end": v(-421.57, 79.44) * mm});
            skLineSegment(sketch, "E2055", {"start": v(-421.57, 79.44) * mm, "end": v(-421.98, 79.75) * mm});
            skLineSegment(sketch, "E2056", {"start": v(-421.98, 79.75) * mm, "end": v(-422.39, 80.06) * mm});
            skLineSegment(sketch, "E2057", {"start": v(-422.39, 80.06) * mm, "end": v(-422.78, 80.38) * mm});
            skLineSegment(sketch, "E2058", {"start": v(-422.78, 80.38) * mm, "end": v(-423.17, 80.72) * mm});
            skLineSegment(sketch, "E2059", {"start": v(-423.17, 80.72) * mm, "end": v(-423.55, 81.06) * mm});
            skLineSegment(sketch, "E2060", {"start": v(-423.55, 81.06) * mm, "end": v(-423.93, 81.41) * mm});
            skLineSegment(sketch, "E2061", {"start": v(-423.93, 81.41) * mm, "end": v(-424.22, 81.7) * mm});
            skLineSegment(sketch, "E2062", {"start": v(-424.22, 81.7) * mm, "end": v(-424.5, 82) * mm});
            skLineSegment(sketch, "E2063", {"start": v(-424.5, 82) * mm, "end": v(-424.78, 82.32) * mm});
            skLineSegment(sketch, "E2064", {"start": v(-424.78, 82.32) * mm, "end": v(-425.04, 82.63) * mm});
            skLineSegment(sketch, "E2065", {"start": v(-425.04, 82.63) * mm, "end": v(-425.3, 82.95) * mm});
            skLineSegment(sketch, "E2066", {"start": v(-425.3, 82.95) * mm, "end": v(-425.55, 83.27) * mm});
            skLineSegment(sketch, "E2067", {"start": v(-425.55, 83.27) * mm, "end": v(-425.8, 83.6) * mm});
            skLineSegment(sketch, "E2068", {"start": v(-425.8, 83.6) * mm, "end": v(-426.03, 83.94) * mm});
            skLineSegment(sketch, "E2069", {"start": v(-426.03, 83.94) * mm, "end": v(-426.25, 84.28) * mm});
            skLineSegment(sketch, "E2070", {"start": v(-426.25, 84.28) * mm, "end": v(-426.46, 84.63) * mm});
            skLineSegment(sketch, "E2071", {"start": v(-426.46, 84.63) * mm, "end": v(-426.67, 84.98) * mm});
            skLineSegment(sketch, "E2072", {"start": v(-426.67, 84.98) * mm, "end": v(-426.87, 85.34) * mm});
            skLineSegment(sketch, "E2073", {"start": v(-426.87, 85.34) * mm, "end": v(-427.06, 85.7) * mm});
            skLineSegment(sketch, "E2074", {"start": v(-427.06, 85.7) * mm, "end": v(-427.24, 86.07) * mm});
            skLineSegment(sketch, "E2075", {"start": v(-427.24, 86.07) * mm, "end": v(-427.4, 86.44) * mm});
            skLineSegment(sketch, "E2076", {"start": v(-427.4, 86.44) * mm, "end": v(-427.57, 86.81) * mm});
            skLineSegment(sketch, "E2077", {"start": v(-427.57, 86.81) * mm, "end": v(-427.72, 87.2) * mm});
            skLineSegment(sketch, "E2078", {"start": v(-427.72, 87.2) * mm, "end": v(-427.86, 87.57) * mm});
            skLineSegment(sketch, "E2079", {"start": v(-427.86, 87.57) * mm, "end": v(-428, 87.96) * mm});
            skLineSegment(sketch, "E2080", {"start": v(-428, 87.96) * mm, "end": v(-428.12, 88.35) * mm});
            skLineSegment(sketch, "E2081", {"start": v(-428.12, 88.35) * mm, "end": v(-428.23, 88.74) * mm});
            skLineSegment(sketch, "E2082", {"start": v(-428.23, 88.74) * mm, "end": v(-428.34, 89.14) * mm});
            skLineSegment(sketch, "E2083", {"start": v(-428.34, 89.14) * mm, "end": v(-428.43, 89.53) * mm});
            skLineSegment(sketch, "E2084", {"start": v(-428.43, 89.53) * mm, "end": v(-428.52, 89.93) * mm});
            skLineSegment(sketch, "E2085", {"start": v(-428.52, 89.93) * mm, "end": v(-428.59, 90.34) * mm});
            skLineSegment(sketch, "E2086", {"start": v(-428.59, 90.34) * mm, "end": v(-428.65, 90.74) * mm});
            skLineSegment(sketch, "E2087", {"start": v(-428.65, 90.74) * mm, "end": v(-428.7, 91.15) * mm});
            skLineSegment(sketch, "E2088", {"start": v(-428.7, 91.15) * mm, "end": v(-428.75, 91.56) * mm});
            skLineSegment(sketch, "E2089", {"start": v(-428.75, 91.56) * mm, "end": v(-428.79, 91.97) * mm});
            skLineSegment(sketch, "E2090", {"start": v(-428.79, 91.97) * mm, "end": v(-428.81, 92.38) * mm});
            skLineSegment(sketch, "E2091", {"start": v(-428.81, 92.38) * mm, "end": v(-428.82, 92.79) * mm});
            skLineSegment(sketch, "E2092", {"start": v(-428.82, 92.79) * mm, "end": v(-428.83, 93.2) * mm});
            skLineSegment(sketch, "E2093", {"start": v(-428.3, 66.63) * mm, "end": v(-388.3, 66.63) * mm});
            skLineSegment(sketch, "E2094", {"start": v(-388.3, 66.63) * mm, "end": v(-388.3, 41.76) * mm});
            skLineSegment(sketch, "E2095", {"start": v(-407.4, 66.63) * mm, "end": v(-407.4, 43.56) * mm});
            skArc(sketch, "E2096", {"start": v(-580.63, 1176.72) * mm, "mid": v(-583.35, 1175.59) * mm, "end": v(-584.48, 1172.87) * mm});
            skArc(sketch, "E2097", {"start": v(-584.48, 1172.87) * mm, "mid": v(-583.35, 1170.15) * mm, "end": v(-580.63, 1169.02) * mm});
            skArc(sketch, "E2098", {"start": v(-580.63, 1169.02) * mm, "mid": v(-577.91, 1170.15) * mm, "end": v(-576.79, 1172.87) * mm});
            skArc(sketch, "E2099", {"start": v(-576.79, 1172.87) * mm, "mid": v(-577.91, 1175.59) * mm, "end": v(-580.63, 1176.72) * mm});
            skArc(sketch, "E2100", {"start": v(-246.54, 1126.24) * mm, "mid": v(-249.26, 1125.12) * mm, "end": v(-250.4, 1122.4) * mm});
            skArc(sketch, "E2101", {"start": v(-250.4, 1122.4) * mm, "mid": v(-249.26, 1119.68) * mm, "end": v(-246.54, 1118.55) * mm});
            skArc(sketch, "E2102", {"start": v(-246.54, 1118.55) * mm, "mid": v(-243.83, 1119.68) * mm, "end": v(-242.7, 1122.4) * mm});
            skArc(sketch, "E2103", {"start": v(-242.7, 1122.4) * mm, "mid": v(-243.83, 1125.12) * mm, "end": v(-246.54, 1126.24) * mm});
            skArc(sketch, "E2104", {"start": v(17.84, 1138.26) * mm, "mid": v(15.12, 1137.13) * mm, "end": v(14, 1134.41) * mm});
            skArc(sketch, "E2105", {"start": v(14, 1134.41) * mm, "mid": v(15.12, 1131.7) * mm, "end": v(17.84, 1130.57) * mm});
            skArc(sketch, "E2106", {"start": v(17.84, 1130.57) * mm, "mid": v(20.56, 1131.7) * mm, "end": v(21.69, 1134.41) * mm});
            skArc(sketch, "E2107", {"start": v(21.69, 1134.41) * mm, "mid": v(20.56, 1137.13) * mm, "end": v(17.84, 1138.26) * mm});
            skArc(sketch, "E2108", {"start": v(373.56, 1131.05) * mm, "mid": v(370.84, 1129.92) * mm, "end": v(369.71, 1127.2) * mm});
            skArc(sketch, "E2109", {"start": v(369.71, 1127.2) * mm, "mid": v(370.84, 1124.48) * mm, "end": v(373.56, 1123.36) * mm});
            skArc(sketch, "E2110", {"start": v(373.56, 1123.36) * mm, "mid": v(376.28, 1124.48) * mm, "end": v(377.4, 1127.2) * mm});
            skArc(sketch, "E2111", {"start": v(377.4, 1127.2) * mm, "mid": v(376.28, 1129.92) * mm, "end": v(373.56, 1131.05) * mm});
            skArc(sketch, "E2112", {"start": v(570.44, 866.84) * mm, "mid": v(567.72, 865.72) * mm, "end": v(566.6, 863) * mm});
            skArc(sketch, "E2113", {"start": v(566.6, 863) * mm, "mid": v(567.72, 860.28) * mm, "end": v(570.44, 859.15) * mm});
            skArc(sketch, "E2114", {"start": v(570.44, 859.15) * mm, "mid": v(573.16, 860.28) * mm, "end": v(574.28, 863) * mm});
            skArc(sketch, "E2115", {"start": v(574.28, 863) * mm, "mid": v(573.16, 865.72) * mm, "end": v(570.44, 866.84) * mm});
            skArc(sketch, "E2116", {"start": v(569.78, 287.75) * mm, "mid": v(567.06, 286.62) * mm, "end": v(565.93, 283.9) * mm});
            skArc(sketch, "E2117", {"start": v(565.93, 283.9) * mm, "mid": v(567.06, 281.18) * mm, "end": v(569.78, 280.06) * mm});
            skArc(sketch, "E2118", {"start": v(569.78, 280.06) * mm, "mid": v(572.5, 281.18) * mm, "end": v(573.62, 283.9) * mm});
            skArc(sketch, "E2119", {"start": v(573.62, 283.9) * mm, "mid": v(572.5, 286.62) * mm, "end": v(569.78, 287.75) * mm});
            skArc(sketch, "E2120", {"start": v(569.87, -537.8) * mm, "mid": v(567.15, -538.92) * mm, "end": v(566.02, -541.64) * mm});
            skArc(sketch, "E2121", {"start": v(566.02, -541.64) * mm, "mid": v(567.15, -544.36) * mm, "end": v(569.87, -545.49) * mm});
            skArc(sketch, "E2122", {"start": v(569.87, -545.49) * mm, "mid": v(572.59, -544.36) * mm, "end": v(573.71, -541.64) * mm});
            skArc(sketch, "E2123", {"start": v(573.71, -541.64) * mm, "mid": v(572.59, -538.92) * mm, "end": v(569.87, -537.8) * mm});
            skArc(sketch, "E2124", {"start": v(423.73, -1174.25) * mm, "mid": v(421.02, -1175.37) * mm, "end": v(419.89, -1178.1) * mm});
            skArc(sketch, "E2125", {"start": v(419.89, -1178.1) * mm, "mid": v(421.02, -1180.81) * mm, "end": v(423.73, -1181.94) * mm});
            skArc(sketch, "E2126", {"start": v(423.73, -1181.94) * mm, "mid": v(426.45, -1180.81) * mm, "end": v(427.58, -1178.1) * mm});
            skArc(sketch, "E2127", {"start": v(427.58, -1178.1) * mm, "mid": v(426.45, -1175.37) * mm, "end": v(423.73, -1174.25) * mm});
            skArc(sketch, "E2128", {"start": v(31.48, -1069.65) * mm, "mid": v(28.76, -1070.78) * mm, "end": v(27.64, -1073.5) * mm});
            skArc(sketch, "E2129", {"start": v(27.64, -1073.5) * mm, "mid": v(28.76, -1076.21) * mm, "end": v(31.48, -1077.34) * mm});
            skArc(sketch, "E2130", {"start": v(31.48, -1077.34) * mm, "mid": v(34.2, -1076.21) * mm, "end": v(35.33, -1073.5) * mm});
            skArc(sketch, "E2131", {"start": v(35.33, -1073.5) * mm, "mid": v(34.2, -1070.78) * mm, "end": v(31.48, -1069.65) * mm});
            skArc(sketch, "E2132", {"start": v(-528.06, -1008.12) * mm, "mid": v(-530.77, -1009.25) * mm, "end": v(-531.9, -1011.97) * mm});
            skArc(sketch, "E2133", {"start": v(-531.9, -1011.97) * mm, "mid": v(-530.77, -1014.68) * mm, "end": v(-528.06, -1015.81) * mm});
            skArc(sketch, "E2134", {"start": v(-528.06, -1015.81) * mm, "mid": v(-525.34, -1014.68) * mm, "end": v(-524.21, -1011.97) * mm});
            skArc(sketch, "E2135", {"start": v(-524.21, -1011.97) * mm, "mid": v(-525.34, -1009.25) * mm, "end": v(-528.06, -1008.12) * mm});
            skArc(sketch, "E2136", {"start": v(-570.36, -507.03) * mm, "mid": v(-573.08, -508.16) * mm, "end": v(-574.2, -510.88) * mm});
            skArc(sketch, "E2137", {"start": v(-574.2, -510.88) * mm, "mid": v(-573.08, -513.6) * mm, "end": v(-570.36, -514.72) * mm});
            skArc(sketch, "E2138", {"start": v(-570.36, -514.72) * mm, "mid": v(-567.64, -513.6) * mm, "end": v(-566.51, -510.88) * mm});
            skArc(sketch, "E2139", {"start": v(-566.51, -510.88) * mm, "mid": v(-567.64, -508.16) * mm, "end": v(-570.36, -507.03) * mm});
            skArc(sketch, "E2140", {"start": v(-581.44, 367.36) * mm, "mid": v(-584.16, 366.24) * mm, "end": v(-585.29, 363.52) * mm});
            skArc(sketch, "E2141", {"start": v(-585.29, 363.52) * mm, "mid": v(-584.16, 360.8) * mm, "end": v(-581.44, 359.67) * mm});
            skArc(sketch, "E2142", {"start": v(-581.44, 359.67) * mm, "mid": v(-578.72, 360.8) * mm, "end": v(-577.6, 363.52) * mm});
            skArc(sketch, "E2143", {"start": v(-577.6, 363.52) * mm, "mid": v(-578.72, 366.24) * mm, "end": v(-581.44, 367.36) * mm});
            skArc(sketch, "E2144", {"start": v(-277.83, 517.91) * mm, "mid": v(-280.55, 516.79) * mm, "end": v(-281.68, 514.07) * mm});
            skArc(sketch, "E2145", {"start": v(-281.68, 514.07) * mm, "mid": v(-280.55, 511.35) * mm, "end": v(-277.83, 510.22) * mm});
            skArc(sketch, "E2146", {"start": v(-277.83, 510.22) * mm, "mid": v(-275.12, 511.35) * mm, "end": v(-273.99, 514.07) * mm});
            skArc(sketch, "E2147", {"start": v(-273.99, 514.07) * mm, "mid": v(-275.12, 516.79) * mm, "end": v(-277.83, 517.91) * mm});
            skArc(sketch, "E2148", {"start": v(-278.17, -354.65) * mm, "mid": v(-280.82, -355.74) * mm, "end": v(-281.92, -358.4) * mm});
            skArc(sketch, "E2149", {"start": v(-281.92, -358.4) * mm, "mid": v(-280.82, -361.05) * mm, "end": v(-278.17, -362.15) * mm});
            skArc(sketch, "E2150", {"start": v(-278.17, -362.15) * mm, "mid": v(-275.52, -361.05) * mm, "end": v(-274.42, -358.4) * mm});
            skArc(sketch, "E2151", {"start": v(-274.42, -358.4) * mm, "mid": v(-275.52, -355.74) * mm, "end": v(-278.17, -354.65) * mm});
            skArc(sketch, "E2152", {"start": v(3, -309.5) * mm, "mid": v(0.35, -310.6) * mm, "end": v(-0.75, -313.25) * mm});
            skArc(sketch, "E2153", {"start": v(-0.75, -313.25) * mm, "mid": v(0.35, -315.9) * mm, "end": v(3, -317) * mm});
            skArc(sketch, "E2154", {"start": v(3, -317) * mm, "mid": v(5.65, -315.9) * mm, "end": v(6.75, -313.25) * mm});
            skArc(sketch, "E2155", {"start": v(6.75, -313.25) * mm, "mid": v(5.65, -310.6) * mm, "end": v(3, -309.5) * mm});
            skArc(sketch, "E2156", {"start": v(281.8, -347.3) * mm, "mid": v(279.15, -348.4) * mm, "end": v(278.05, -351.05) * mm});
            skArc(sketch, "E2157", {"start": v(278.05, -351.05) * mm, "mid": v(279.15, -353.7) * mm, "end": v(281.8, -354.8) * mm});
            skArc(sketch, "E2158", {"start": v(281.8, -354.8) * mm, "mid": v(284.45, -353.7) * mm, "end": v(285.55, -351.05) * mm});
            skArc(sketch, "E2159", {"start": v(285.55, -351.05) * mm, "mid": v(284.45, -348.4) * mm, "end": v(281.8, -347.3) * mm});
            skArc(sketch, "E2160", {"start": v(2.55, 474.39) * mm, "mid": v(-0.1, 473.3) * mm, "end": v(-1.2, 470.64) * mm});
            skArc(sketch, "E2161", {"start": v(-1.2, 470.64) * mm, "mid": v(-0.1, 467.99) * mm, "end": v(2.55, 466.89) * mm});
            skArc(sketch, "E2162", {"start": v(2.55, 466.89) * mm, "mid": v(5.2, 467.99) * mm, "end": v(6.3, 470.64) * mm});
            skArc(sketch, "E2163", {"start": v(6.3, 470.64) * mm, "mid": v(5.2, 473.3) * mm, "end": v(2.55, 474.39) * mm});
            skArc(sketch, "E2164", {"start": v(281.9, 448.55) * mm, "mid": v(279.25, 447.45) * mm, "end": v(278.15, 444.8) * mm});
            skArc(sketch, "E2165", {"start": v(278.15, 444.8) * mm, "mid": v(279.25, 442.15) * mm, "end": v(281.9, 441.05) * mm});
            skArc(sketch, "E2166", {"start": v(281.9, 441.05) * mm, "mid": v(284.55, 442.15) * mm, "end": v(285.65, 444.8) * mm});
            skArc(sketch, "E2167", {"start": v(285.65, 444.8) * mm, "mid": v(284.55, 447.45) * mm, "end": v(281.9, 448.55) * mm});
            skArc(sketch, "E2168", {"start": v(-418.36, 728.63) * mm, "mid": v(-421.02, 727.53) * mm, "end": v(-422.11, 724.88) * mm});
            skArc(sketch, "E2169", {"start": v(-422.11, 724.88) * mm, "mid": v(-421.02, 722.23) * mm, "end": v(-418.36, 721.13) * mm});
            skArc(sketch, "E2170", {"start": v(-418.36, 721.13) * mm, "mid": v(-415.71, 722.23) * mm, "end": v(-414.61, 724.88) * mm});
            skArc(sketch, "E2171", {"start": v(-414.61, 724.88) * mm, "mid": v(-415.71, 727.53) * mm, "end": v(-418.36, 728.63) * mm});
            skArc(sketch, "E2172", {"start": v(-412.5, -4.86) * mm, "mid": v(-415.15, -5.96) * mm, "end": v(-416.25, -8.61) * mm});
            skArc(sketch, "E2173", {"start": v(-416.25, -8.61) * mm, "mid": v(-415.15, -11.26) * mm, "end": v(-412.5, -12.36) * mm});
            skArc(sketch, "E2174", {"start": v(-412.5, -12.36) * mm, "mid": v(-409.84, -11.26) * mm, "end": v(-408.75, -8.61) * mm});
            skArc(sketch, "E2175", {"start": v(-408.75, -8.61) * mm, "mid": v(-409.84, -5.96) * mm, "end": v(-412.5, -4.86) * mm});
            skArc(sketch, "E2176", {"start": v(-430.1, -750.1) * mm, "mid": v(-432.75, -751.19) * mm, "end": v(-433.85, -753.84) * mm});
            skArc(sketch, "E2177", {"start": v(-433.85, -753.84) * mm, "mid": v(-432.75, -756.5) * mm, "end": v(-430.1, -757.6) * mm});
            skArc(sketch, "E2178", {"start": v(-430.1, -757.6) * mm, "mid": v(-427.45, -756.5) * mm, "end": v(-426.35, -753.84) * mm});
            skArc(sketch, "E2179", {"start": v(-426.35, -753.84) * mm, "mid": v(-427.45, -751.19) * mm, "end": v(-430.1, -750.1) * mm});
            skArc(sketch, "E2180", {"start": v(-119.1, -45.94) * mm, "mid": v(-121.75, -47.04) * mm, "end": v(-122.85, -49.69) * mm});
            skArc(sketch, "E2181", {"start": v(-122.85, -49.69) * mm, "mid": v(-121.75, -52.34) * mm, "end": v(-119.1, -53.44) * mm});
            skArc(sketch, "E2182", {"start": v(-119.1, -53.44) * mm, "mid": v(-116.45, -52.34) * mm, "end": v(-115.35, -49.69) * mm});
            skArc(sketch, "E2183", {"start": v(-115.35, -49.69) * mm, "mid": v(-116.45, -47.04) * mm, "end": v(-119.1, -45.94) * mm});
            skArc(sketch, "E2184", {"start": v(-124.97, -791.17) * mm, "mid": v(-127.62, -792.26) * mm, "end": v(-128.72, -794.92) * mm});
            skArc(sketch, "E2185", {"start": v(-128.72, -794.92) * mm, "mid": v(-127.62, -797.57) * mm, "end": v(-124.97, -798.67) * mm});
            skArc(sketch, "E2186", {"start": v(-124.97, -798.67) * mm, "mid": v(-122.31, -797.57) * mm, "end": v(-121.22, -794.92) * mm});
            skArc(sketch, "E2187", {"start": v(-121.22, -794.92) * mm, "mid": v(-122.31, -792.26) * mm, "end": v(-124.97, -791.17) * mm});
            skArc(sketch, "E2188", {"start": v(-130.83, 775.57) * mm, "mid": v(-133.49, 774.48) * mm, "end": v(-134.58, 771.82) * mm});
            skArc(sketch, "E2189", {"start": v(-134.58, 771.82) * mm, "mid": v(-133.49, 769.17) * mm, "end": v(-130.83, 768.07) * mm});
            skArc(sketch, "E2190", {"start": v(-130.83, 768.07) * mm, "mid": v(-128.18, 769.17) * mm, "end": v(-127.08, 771.82) * mm});
            skArc(sketch, "E2191", {"start": v(-127.08, 771.82) * mm, "mid": v(-128.18, 774.48) * mm, "end": v(-130.83, 775.57) * mm});
            skArc(sketch, "E2192", {"start": v(150.83, 810.78) * mm, "mid": v(148.17, 809.68) * mm, "end": v(147.08, 807.03) * mm});
            skArc(sketch, "E2193", {"start": v(147.08, 807.03) * mm, "mid": v(148.17, 804.38) * mm, "end": v(150.83, 803.28) * mm});
            skArc(sketch, "E2194", {"start": v(150.83, 803.28) * mm, "mid": v(153.48, 804.38) * mm, "end": v(154.58, 807.03) * mm});
            skArc(sketch, "E2195", {"start": v(154.58, 807.03) * mm, "mid": v(153.48, 809.68) * mm, "end": v(150.83, 810.78) * mm});
            skArc(sketch, "E2196", {"start": v(133.22, 147.7) * mm, "mid": v(130.57, 146.6) * mm, "end": v(129.47, 143.95) * mm});
            skArc(sketch, "E2197", {"start": v(129.47, 143.95) * mm, "mid": v(130.57, 141.3) * mm, "end": v(133.22, 140.2) * mm});
            skArc(sketch, "E2198", {"start": v(133.22, 140.2) * mm, "mid": v(135.87, 141.3) * mm, "end": v(136.97, 143.95) * mm});
            skArc(sketch, "E2199", {"start": v(136.97, 143.95) * mm, "mid": v(135.87, 146.6) * mm, "end": v(133.22, 147.7) * mm});
            skArc(sketch, "E2200", {"start": v(139.1, -797.03) * mm, "mid": v(136.44, -798.13) * mm, "end": v(135.34, -800.78) * mm});
            skArc(sketch, "E2201", {"start": v(135.34, -800.78) * mm, "mid": v(136.44, -803.43) * mm, "end": v(139.1, -804.53) * mm});
            skArc(sketch, "E2202", {"start": v(139.1, -804.53) * mm, "mid": v(141.74, -803.43) * mm, "end": v(142.84, -800.78) * mm});
            skArc(sketch, "E2203", {"start": v(142.84, -800.78) * mm, "mid": v(141.74, -798.13) * mm, "end": v(139.1, -797.03) * mm});
            skArc(sketch, "E2204", {"start": v(391.41, -767.7) * mm, "mid": v(388.76, -768.8) * mm, "end": v(387.66, -771.44) * mm});
            skArc(sketch, "E2205", {"start": v(387.66, -771.44) * mm, "mid": v(388.76, -774.1) * mm, "end": v(391.41, -775.2) * mm});
            skArc(sketch, "E2206", {"start": v(391.41, -775.2) * mm, "mid": v(394.06, -774.1) * mm, "end": v(395.16, -771.44) * mm});
            skArc(sketch, "E2207", {"start": v(395.16, -771.44) * mm, "mid": v(394.06, -768.8) * mm, "end": v(391.41, -767.7) * mm});
            skArc(sketch, "E2208", {"start": v(420.75, -116.35) * mm, "mid": v(418.1, -117.45) * mm, "end": v(417, -120.1) * mm});
            skArc(sketch, "E2209", {"start": v(417, -120.1) * mm, "mid": v(418.1, -122.75) * mm, "end": v(420.75, -123.85) * mm});
            skArc(sketch, "E2210", {"start": v(420.75, -123.85) * mm, "mid": v(423.4, -122.75) * mm, "end": v(424.5, -120.1) * mm});
            skArc(sketch, "E2211", {"start": v(424.5, -120.1) * mm, "mid": v(423.4, -117.45) * mm, "end": v(420.75, -116.35) * mm});
            skArc(sketch, "E2212", {"start": v(409.02, 605.4) * mm, "mid": v(406.36, 604.3) * mm, "end": v(405.27, 601.65) * mm});
            skArc(sketch, "E2213", {"start": v(405.27, 601.65) * mm, "mid": v(406.36, 599) * mm, "end": v(409.02, 597.9) * mm});
            skArc(sketch, "E2214", {"start": v(409.02, 597.9) * mm, "mid": v(411.67, 599) * mm, "end": v(412.77, 601.65) * mm});
            skArc(sketch, "E2215", {"start": v(412.77, 601.65) * mm, "mid": v(411.67, 604.3) * mm, "end": v(409.02, 605.4) * mm});
            skSolve(sketch);
        }
        {
            var Q0;
            Q0=makeQuery(id+"F0.imprint","IMPRINT",FACE,{"disambiguationData":[TD([[makeQuery(id+"F0.imprint","IMPRINT",EDGE,{"derivedFrom":sQuery(id+"F0.wireOp",EDGE,"E16")}),1.0]])]});
            var Q1;
            {var subQ0=sQuery(id+"F0.wireOp",EDGE,"E1467");Q1=makeQuery(id+"F0.imprint","IMPRINT",FACE,{"disambiguationData":[TD([[makeQuery(id+"F0.imprint","IMPRINT",EDGE,{"derivedFrom":subQ0}),-1.0]])]});}
            var Q2;
            Q2=makeQuery(id+"F0.imprint","IMPRINT",FACE,{"disambiguationData":[TD([[makeQuery(id+"F0.imprint","IMPRINT",EDGE,{"derivedFrom":sQuery(id+"F0.wireOp",EDGE,"E1581")}),-1.0]])]});
            var Q3;
            Q3=makeQuery(id+"F0.imprint","IMPRINT",FACE,{"disambiguationData":[TD([[makeQuery(id+"F0.imprint","IMPRINT",EDGE,{"derivedFrom":sQuery(id+"F0.wireOp",EDGE,"E1837")}),-1.0]])]});
            extrude(context, id + "F1", {"entities" : qUnion([Q0, Q1, Q2, Q3]), "depth" : 18 * mm});
        }
        {
            var Q0;
            {var subQ1=sQuery(id+"F0.wireOp",EDGE,"E8");Q0=makeQuery(id+"F0.imprint","IMPRINT",FACE,{"disambiguationData":[TD([[makeQuery(id+"F0.imprint","IMPRINT",EDGE,{"derivedFrom":subQ1}),1.0]])]});}
            var Q1;
            Q1=makeQuery(id+"F0.imprint","IMPRINT",FACE,{"disambiguationData":[TD([[makeQuery(id+"F0.imprint","IMPRINT",EDGE,{"derivedFrom":sQuery(id+"F0.wireOp",EDGE,"E701")}),-1.0]])]});
            extrude(context, id + "F2", {"entities" : qUnion([Q0, Q1]), "depth" : 18 * mm});
        }
    });
